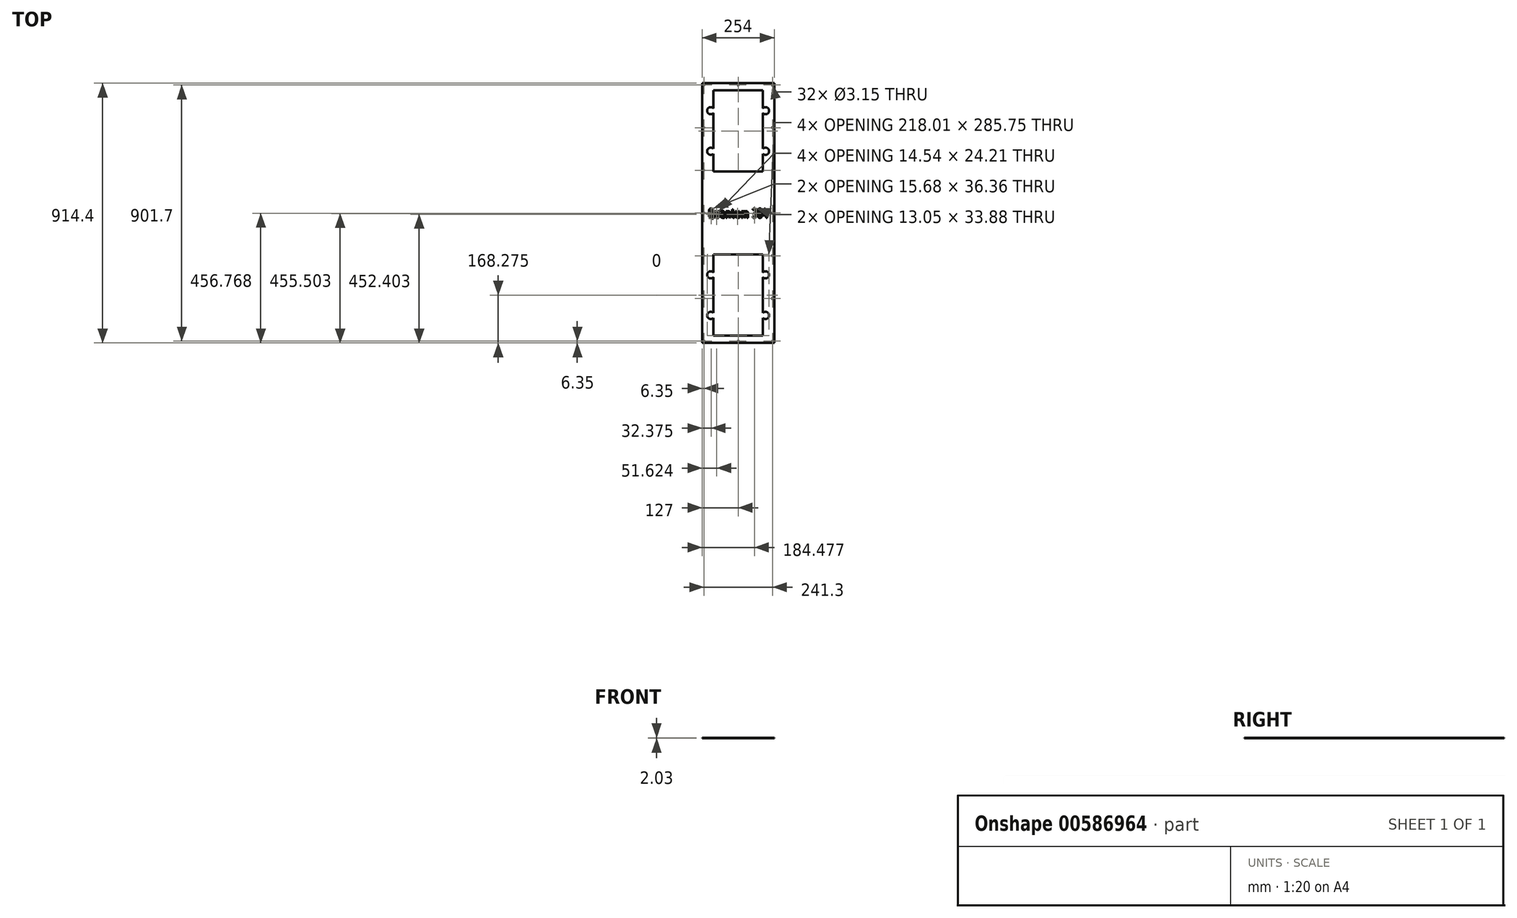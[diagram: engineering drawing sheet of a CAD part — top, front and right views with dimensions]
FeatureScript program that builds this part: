
annotation { "Feature Type Name" : "Feature", "Feature Type Description" : "" }
export const myFeature = defineFeature(function(context is Context, id is Id, definition is map)
    precondition{}
    {
        {
            var Q0;
            Q0=qCreatedBy(makeId("Top.planeOp"),FACE);
            var sketch = newSketch(context, id + "F0", { "sketchPlane" : qUnion([Q0])});
            skLineSegment(sketch, "E0", {"start": v(73.23, -10.8) * mm, "end": v(73.3, -11.12) * mm});
            skLineSegment(sketch, "E1", {"start": v(73.18, -10.45) * mm, "end": v(73.23, -10.8) * mm});
            skLineSegment(sketch, "E2", {"start": v(73.15, -10.1) * mm, "end": v(73.18, -10.45) * mm});
            skLineSegment(sketch, "E3", {"start": v(73.15, -3.36) * mm, "end": v(73.15, -10.1) * mm});
            skLineSegment(sketch, "E4", {"start": v(73.15, -3.18) * mm, "end": v(73.15, -3.36) * mm});
            skLineSegment(sketch, "E5", {"start": v(73.13, -2.99) * mm, "end": v(73.15, -3.18) * mm});
            skLineSegment(sketch, "E6", {"start": v(73.08, -2.81) * mm, "end": v(73.13, -2.99) * mm});
            skLineSegment(sketch, "E7", {"start": v(73.03, -2.64) * mm, "end": v(73.08, -2.81) * mm});
            skLineSegment(sketch, "E8", {"start": v(72.96, -2.47) * mm, "end": v(73.03, -2.64) * mm});
            skLineSegment(sketch, "E9", {"start": v(72.86, -2.3) * mm, "end": v(72.96, -2.47) * mm});
            skLineSegment(sketch, "E10", {"start": v(72.73, -2.14) * mm, "end": v(72.86, -2.3) * mm});
            skLineSegment(sketch, "E11", {"start": v(72.6, -2) * mm, "end": v(72.73, -2.14) * mm});
            skLineSegment(sketch, "E12", {"start": v(72.46, -1.87) * mm, "end": v(72.6, -2) * mm});
            skLineSegment(sketch, "E13", {"start": v(72.31, -1.75) * mm, "end": v(72.46, -1.87) * mm});
            skLineSegment(sketch, "E14", {"start": v(72.14, -1.65) * mm, "end": v(72.31, -1.75) * mm});
            skLineSegment(sketch, "E15", {"start": v(71.96, -1.57) * mm, "end": v(72.14, -1.65) * mm});
            skLineSegment(sketch, "E16", {"start": v(71.79, -1.52) * mm, "end": v(71.96, -1.57) * mm});
            skLineSegment(sketch, "E17", {"start": v(71.62, -1.47) * mm, "end": v(71.79, -1.52) * mm});
            skLineSegment(sketch, "E18", {"start": v(71.42, -1.45) * mm, "end": v(71.62, -1.47) * mm});
            skLineSegment(sketch, "E19", {"start": v(71.22, -1.42) * mm, "end": v(71.42, -1.45) * mm});
            skLineSegment(sketch, "E20", {"start": v(71.05, -1.45) * mm, "end": v(71.22, -1.42) * mm});
            skLineSegment(sketch, "E21", {"start": v(70.85, -1.47) * mm, "end": v(71.05, -1.45) * mm});
            skLineSegment(sketch, "E22", {"start": v(70.67, -1.52) * mm, "end": v(70.85, -1.47) * mm});
            skLineSegment(sketch, "E23", {"start": v(70.5, -1.57) * mm, "end": v(70.67, -1.52) * mm});
            skLineSegment(sketch, "E24", {"start": v(70.33, -1.65) * mm, "end": v(70.5, -1.57) * mm});
            skLineSegment(sketch, "E25", {"start": v(70.15, -1.75) * mm, "end": v(70.33, -1.65) * mm});
            skLineSegment(sketch, "E26", {"start": v(70, -1.87) * mm, "end": v(70.15, -1.75) * mm});
            skLineSegment(sketch, "E27", {"start": v(69.85, -2) * mm, "end": v(70, -1.87) * mm});
            skLineSegment(sketch, "E28", {"start": v(69.73, -2.14) * mm, "end": v(69.85, -2) * mm});
            skLineSegment(sketch, "E29", {"start": v(69.6, -2.3) * mm, "end": v(69.73, -2.14) * mm});
            skLineSegment(sketch, "E30", {"start": v(69.5, -2.47) * mm, "end": v(69.6, -2.3) * mm});
            skLineSegment(sketch, "E31", {"start": v(69.43, -2.64) * mm, "end": v(69.5, -2.47) * mm});
            skLineSegment(sketch, "E32", {"start": v(69.38, -2.81) * mm, "end": v(69.43, -2.64) * mm});
            skLineSegment(sketch, "E33", {"start": v(69.33, -2.99) * mm, "end": v(69.38, -2.81) * mm});
            skLineSegment(sketch, "E34", {"start": v(69.3, -3.18) * mm, "end": v(69.33, -2.99) * mm});
            skLineSegment(sketch, "E35", {"start": v(69.28, -3.36) * mm, "end": v(69.3, -3.18) * mm});
            skLineSegment(sketch, "E36", {"start": v(69.28, -10.1) * mm, "end": v(69.28, -3.36) * mm});
            skLineSegment(sketch, "E37", {"start": v(69.33, -10.85) * mm, "end": v(69.28, -10.1) * mm});
            skLineSegment(sketch, "E38", {"start": v(51, -14.17) * mm, "end": v(50.98, -13.97) * mm});
            skLineSegment(sketch, "E39", {"start": v(51.05, -14.35) * mm, "end": v(51, -14.17) * mm});
            skLineSegment(sketch, "E40", {"start": v(51.1, -14.52) * mm, "end": v(51.05, -14.35) * mm});
            skLineSegment(sketch, "E41", {"start": v(51.2, -14.7) * mm, "end": v(51.1, -14.52) * mm});
            skLineSegment(sketch, "E42", {"start": v(51.3, -14.84) * mm, "end": v(51.2, -14.7) * mm});
            skLineSegment(sketch, "E43", {"start": v(51.4, -15) * mm, "end": v(51.3, -14.84) * mm});
            skLineSegment(sketch, "E44", {"start": v(51.55, -15.14) * mm, "end": v(51.4, -15) * mm});
            skLineSegment(sketch, "E45", {"start": v(52.12, -15.66) * mm, "end": v(51.55, -15.14) * mm});
            skLineSegment(sketch, "E46", {"start": v(52.7, -16.13) * mm, "end": v(52.12, -15.66) * mm});
            skLineSegment(sketch, "E47", {"start": v(53.31, -16.5) * mm, "end": v(52.7, -16.13) * mm});
            skLineSegment(sketch, "E48", {"start": v(53.96, -16.83) * mm, "end": v(53.31, -16.5) * mm});
            skLineSegment(sketch, "E49", {"start": v(54.6, -17.05) * mm, "end": v(53.96, -16.83) * mm});
            skLineSegment(sketch, "E50", {"start": v(55.3, -17.22) * mm, "end": v(54.6, -17.05) * mm});
            skLineSegment(sketch, "E51", {"start": v(56.01, -17.35) * mm, "end": v(55.3, -17.22) * mm});
            skLineSegment(sketch, "E52", {"start": v(56.73, -17.37) * mm, "end": v(56.01, -17.35) * mm});
            skLineSegment(sketch, "E53", {"start": v(57.48, -17.35) * mm, "end": v(56.73, -17.37) * mm});
            skLineSegment(sketch, "E54", {"start": v(58.2, -17.25) * mm, "end": v(57.48, -17.35) * mm});
            skLineSegment(sketch, "E55", {"start": v(58.87, -17.08) * mm, "end": v(58.2, -17.25) * mm});
            skLineSegment(sketch, "E56", {"start": v(59.54, -16.85) * mm, "end": v(58.87, -17.08) * mm});
            skLineSegment(sketch, "E57", {"start": v(60.16, -16.53) * mm, "end": v(59.54, -16.85) * mm});
            skLineSegment(sketch, "E58", {"start": v(60.75, -16.18) * mm, "end": v(60.16, -16.53) * mm});
            skLineSegment(sketch, "E59", {"start": v(61.32, -15.74) * mm, "end": v(60.75, -16.18) * mm});
            skLineSegment(sketch, "E60", {"start": v(61.87, -15.24) * mm, "end": v(61.32, -15.74) * mm});
            skLineSegment(sketch, "E61", {"start": v(62.36, -14.7) * mm, "end": v(61.87, -15.24) * mm});
            skLineSegment(sketch, "E62", {"start": v(62.81, -14.12) * mm, "end": v(62.36, -14.7) * mm});
            skLineSegment(sketch, "E63", {"start": v(63.16, -13.53) * mm, "end": v(62.81, -14.12) * mm});
            skLineSegment(sketch, "E64", {"start": v(63.48, -12.9) * mm, "end": v(63.16, -13.53) * mm});
            skLineSegment(sketch, "E65", {"start": v(63.7, -12.24) * mm, "end": v(63.48, -12.9) * mm});
            skLineSegment(sketch, "E66", {"start": v(63.88, -11.57) * mm, "end": v(63.7, -12.24) * mm});
            skLineSegment(sketch, "E67", {"start": v(63.98, -10.85) * mm, "end": v(63.88, -11.57) * mm});
            skLineSegment(sketch, "E68", {"start": v(64, -10.1) * mm, "end": v(63.98, -10.85) * mm});
            skLineSegment(sketch, "E69", {"start": v(64, -4.77) * mm, "end": v(64, -10.1) * mm});
            skLineSegment(sketch, "E70", {"start": v(63.98, -4.13) * mm, "end": v(64, -4.77) * mm});
            skLineSegment(sketch, "E71", {"start": v(63.9, -3.53) * mm, "end": v(63.98, -4.13) * mm});
            skLineSegment(sketch, "E72", {"start": v(63.75, -2.94) * mm, "end": v(63.9, -3.53) * mm});
            skLineSegment(sketch, "E73", {"start": v(63.55, -2.4) * mm, "end": v(63.75, -2.94) * mm});
            skLineSegment(sketch, "E74", {"start": v(63.3, -1.87) * mm, "end": v(63.55, -2.4) * mm});
            skLineSegment(sketch, "E75", {"start": v(63, -1.35) * mm, "end": v(63.3, -1.87) * mm});
            skLineSegment(sketch, "E76", {"start": v(62.64, -0.88) * mm, "end": v(63, -1.35) * mm});
            skLineSegment(sketch, "E77", {"start": v(62.24, -0.43) * mm, "end": v(62.64, -0.88) * mm});
            skLineSegment(sketch, "E78", {"start": v(62.64, 0.04) * mm, "end": v(62.24, -0.43) * mm});
            skLineSegment(sketch, "E79", {"start": v(63, 0.51) * mm, "end": v(62.64, 0.04) * mm});
            skLineSegment(sketch, "E80", {"start": v(63.3, 1.03) * mm, "end": v(63, 0.51) * mm});
            skLineSegment(sketch, "E81", {"start": v(63.55, 1.55) * mm, "end": v(63.3, 1.03) * mm});
            skLineSegment(sketch, "E82", {"start": v(63.75, 2.1) * mm, "end": v(63.55, 1.55) * mm});
            skLineSegment(sketch, "E83", {"start": v(63.9, 2.7) * mm, "end": v(63.75, 2.1) * mm});
            skLineSegment(sketch, "E84", {"start": v(63.98, 3.29) * mm, "end": v(63.9, 2.7) * mm});
            skLineSegment(sketch, "E85", {"start": v(64, 3.93) * mm, "end": v(63.98, 3.29) * mm});
            skLineSegment(sketch, "E86", {"start": v(64, 9.24) * mm, "end": v(64, 3.93) * mm});
            skLineSegment(sketch, "E87", {"start": v(63.98, 9.99) * mm, "end": v(64, 9.24) * mm});
            skLineSegment(sketch, "E88", {"start": v(63.88, 10.7) * mm, "end": v(63.98, 9.99) * mm});
            skLineSegment(sketch, "E89", {"start": v(63.7, 11.38) * mm, "end": v(63.88, 10.7) * mm});
            skLineSegment(sketch, "E90", {"start": v(63.48, 12.05) * mm, "end": v(63.7, 11.38) * mm});
            skLineSegment(sketch, "E91", {"start": v(63.16, 12.67) * mm, "end": v(63.48, 12.05) * mm});
            skLineSegment(sketch, "E92", {"start": v(62.81, 13.26) * mm, "end": v(63.16, 12.67) * mm});
            skLineSegment(sketch, "E93", {"start": v(62.36, 13.83) * mm, "end": v(62.81, 13.26) * mm});
            skLineSegment(sketch, "E94", {"start": v(61.87, 14.38) * mm, "end": v(62.36, 13.83) * mm});
            skLineSegment(sketch, "E95", {"start": v(61.32, 14.87) * mm, "end": v(61.87, 14.38) * mm});
            skLineSegment(sketch, "E96", {"start": v(60.75, 15.32) * mm, "end": v(61.32, 14.87) * mm});
            skLineSegment(sketch, "E97", {"start": v(60.16, 15.67) * mm, "end": v(60.75, 15.32) * mm});
            skLineSegment(sketch, "E98", {"start": v(59.54, 15.99) * mm, "end": v(60.16, 15.67) * mm});
            skLineSegment(sketch, "E99", {"start": v(58.87, 16.21) * mm, "end": v(59.54, 15.99) * mm});
            skLineSegment(sketch, "E100", {"start": v(58.2, 16.39) * mm, "end": v(58.87, 16.21) * mm});
            skLineSegment(sketch, "E101", {"start": v(57.48, 16.49) * mm, "end": v(58.2, 16.39) * mm});
            skLineSegment(sketch, "E102", {"start": v(56.73, 16.51) * mm, "end": v(57.48, 16.49) * mm});
            skLineSegment(sketch, "E103", {"start": v(56.01, 16.49) * mm, "end": v(56.73, 16.51) * mm});
            skLineSegment(sketch, "E104", {"start": v(55.3, 16.36) * mm, "end": v(56.01, 16.49) * mm});
            skLineSegment(sketch, "E105", {"start": v(54.6, 16.19) * mm, "end": v(55.3, 16.36) * mm});
            skLineSegment(sketch, "E106", {"start": v(53.96, 15.96) * mm, "end": v(54.6, 16.19) * mm});
            skLineSegment(sketch, "E107", {"start": v(53.31, 15.64) * mm, "end": v(53.96, 15.96) * mm});
            skLineSegment(sketch, "E108", {"start": v(52.7, 15.27) * mm, "end": v(53.31, 15.64) * mm});
            skLineSegment(sketch, "E109", {"start": v(52.12, 14.8) * mm, "end": v(52.7, 15.27) * mm});
            skLineSegment(sketch, "E110", {"start": v(51.55, 14.28) * mm, "end": v(52.12, 14.8) * mm});
            skLineSegment(sketch, "E111", {"start": v(51.4, 14.13) * mm, "end": v(51.55, 14.28) * mm});
            skLineSegment(sketch, "E112", {"start": v(51.3, 13.98) * mm, "end": v(51.4, 14.13) * mm});
            skLineSegment(sketch, "E113", {"start": v(51.2, 13.83) * mm, "end": v(51.3, 13.98) * mm});
            skLineSegment(sketch, "E114", {"start": v(51.1, 13.66) * mm, "end": v(51.2, 13.83) * mm});
            skLineSegment(sketch, "E115", {"start": v(51.05, 13.48) * mm, "end": v(51.1, 13.66) * mm});
            skLineSegment(sketch, "E116", {"start": v(51, 13.31) * mm, "end": v(51.05, 13.48) * mm});
            skLineSegment(sketch, "E117", {"start": v(50.98, 13.11) * mm, "end": v(51, 13.31) * mm});
            skLineSegment(sketch, "E118", {"start": v(50.95, 12.94) * mm, "end": v(50.98, 13.11) * mm});
            skLineSegment(sketch, "E119", {"start": v(50.98, 12.74) * mm, "end": v(50.95, 12.94) * mm});
            skLineSegment(sketch, "E120", {"start": v(51, 12.54) * mm, "end": v(50.98, 12.74) * mm});
            skLineSegment(sketch, "E121", {"start": v(51.05, 12.37) * mm, "end": v(51, 12.54) * mm});
            skLineSegment(sketch, "E122", {"start": v(51.1, 12.2) * mm, "end": v(51.05, 12.37) * mm});
            skLineSegment(sketch, "E123", {"start": v(51.18, 12.02) * mm, "end": v(51.1, 12.2) * mm});
            skLineSegment(sketch, "E124", {"start": v(51.28, 11.87) * mm, "end": v(51.18, 12.02) * mm});
            skLineSegment(sketch, "E125", {"start": v(51.4, 11.7) * mm, "end": v(51.28, 11.87) * mm});
            skLineSegment(sketch, "E126", {"start": v(51.52, 11.57) * mm, "end": v(51.4, 11.7) * mm});
            skLineSegment(sketch, "E127", {"start": v(51.67, 11.43) * mm, "end": v(51.52, 11.57) * mm});
            skLineSegment(sketch, "E128", {"start": v(51.82, 11.33) * mm, "end": v(51.67, 11.43) * mm});
            skLineSegment(sketch, "E129", {"start": v(52, 11.23) * mm, "end": v(51.82, 11.33) * mm});
            skLineSegment(sketch, "E130", {"start": v(52.17, 11.13) * mm, "end": v(52, 11.23) * mm});
            skLineSegment(sketch, "E131", {"start": v(52.34, 11.08) * mm, "end": v(52.17, 11.13) * mm});
            skLineSegment(sketch, "E132", {"start": v(52.52, 11.03) * mm, "end": v(52.34, 11.08) * mm});
            skLineSegment(sketch, "E133", {"start": v(52.71, 11) * mm, "end": v(52.52, 11.03) * mm});
            skLineSegment(sketch, "E134", {"start": v(52.89, 11) * mm, "end": v(52.71, 11) * mm});
            skLineSegment(sketch, "E135", {"start": v(53.09, 11) * mm, "end": v(52.89, 11) * mm});
            skLineSegment(sketch, "E136", {"start": v(53.29, 11.03) * mm, "end": v(53.09, 11) * mm});
            skLineSegment(sketch, "E137", {"start": v(53.46, 11.08) * mm, "end": v(53.29, 11.03) * mm});
            skLineSegment(sketch, "E138", {"start": v(53.63, 11.15) * mm, "end": v(53.46, 11.08) * mm});
            skLineSegment(sketch, "E139", {"start": v(53.8, 11.23) * mm, "end": v(53.63, 11.15) * mm});
            skLineSegment(sketch, "E140", {"start": v(53.98, 11.33) * mm, "end": v(53.8, 11.23) * mm});
            skLineSegment(sketch, "E141", {"start": v(54.13, 11.45) * mm, "end": v(53.98, 11.33) * mm});
            skLineSegment(sketch, "E142", {"start": v(54.28, 11.57) * mm, "end": v(54.13, 11.45) * mm});
            skLineSegment(sketch, "E143", {"start": v(54.55, 11.82) * mm, "end": v(54.28, 11.57) * mm});
            skLineSegment(sketch, "E144", {"start": v(54.85, 12.02) * mm, "end": v(54.55, 11.82) * mm});
            skLineSegment(sketch, "E145", {"start": v(55.15, 12.22) * mm, "end": v(54.85, 12.02) * mm});
            skLineSegment(sketch, "E146", {"start": v(55.44, 12.37) * mm, "end": v(55.15, 12.22) * mm});
            skLineSegment(sketch, "E147", {"start": v(55.74, 12.47) * mm, "end": v(55.44, 12.37) * mm});
            skLineSegment(sketch, "E148", {"start": v(56.06, 12.54) * mm, "end": v(55.74, 12.47) * mm});
            skLineSegment(sketch, "E149", {"start": v(56.41, 12.6) * mm, "end": v(56.06, 12.54) * mm});
            skLineSegment(sketch, "E150", {"start": v(56.73, 12.62) * mm, "end": v(56.41, 12.6) * mm});
            skLineSegment(sketch, "E151", {"start": v(57.1, 12.6) * mm, "end": v(56.73, 12.62) * mm});
            skLineSegment(sketch, "E152", {"start": v(57.43, 12.57) * mm, "end": v(57.1, 12.6) * mm});
            skLineSegment(sketch, "E153", {"start": v(57.75, 12.47) * mm, "end": v(57.43, 12.57) * mm});
            skLineSegment(sketch, "E154", {"start": v(58.05, 12.37) * mm, "end": v(57.75, 12.47) * mm});
            skLineSegment(sketch, "E155", {"start": v(58.35, 12.22) * mm, "end": v(58.05, 12.37) * mm});
            skLineSegment(sketch, "E156", {"start": v(58.64, 12.07) * mm, "end": v(58.35, 12.22) * mm});
            skLineSegment(sketch, "E157", {"start": v(58.9, 11.85) * mm, "end": v(58.64, 12.07) * mm});
            skLineSegment(sketch, "E158", {"start": v(59.14, 11.62) * mm, "end": v(58.9, 11.85) * mm});
            skLineSegment(sketch, "E159", {"start": v(59.39, 11.38) * mm, "end": v(59.14, 11.62) * mm});
            skLineSegment(sketch, "E160", {"start": v(59.59, 11.1) * mm, "end": v(59.39, 11.38) * mm});
            skLineSegment(sketch, "E161", {"start": v(59.76, 10.83) * mm, "end": v(59.59, 11.1) * mm});
            skLineSegment(sketch, "E162", {"start": v(59.88, 10.53) * mm, "end": v(59.76, 10.83) * mm});
            skLineSegment(sketch, "E163", {"start": v(59.98, 10.23) * mm, "end": v(59.88, 10.53) * mm});
            skLineSegment(sketch, "E164", {"start": v(60.08, 9.91) * mm, "end": v(59.98, 10.23) * mm});
            skLineSegment(sketch, "E165", {"start": v(60.1, 9.59) * mm, "end": v(60.08, 9.91) * mm});
            skLineSegment(sketch, "E166", {"start": v(60.13, 9.24) * mm, "end": v(60.1, 9.59) * mm});
            skLineSegment(sketch, "E167", {"start": v(60.13, 3.93) * mm, "end": v(60.13, 9.24) * mm});
            skLineSegment(sketch, "E168", {"start": v(60.13, 3.69) * mm, "end": v(60.13, 3.93) * mm});
            skLineSegment(sketch, "E169", {"start": v(60.08, 3.44) * mm, "end": v(60.13, 3.69) * mm});
            skLineSegment(sketch, "E170", {"start": v(60.03, 3.21) * mm, "end": v(60.08, 3.44) * mm});
            skLineSegment(sketch, "E171", {"start": v(59.96, 3) * mm, "end": v(60.03, 3.21) * mm});
            skLineSegment(sketch, "E172", {"start": v(59.86, 2.8) * mm, "end": v(59.96, 3) * mm});
            skLineSegment(sketch, "E173", {"start": v(59.73, 2.6) * mm, "end": v(59.86, 2.8) * mm});
            skLineSegment(sketch, "E174", {"start": v(59.61, 2.4) * mm, "end": v(59.73, 2.6) * mm});
            skLineSegment(sketch, "E175", {"start": v(59.44, 2.22) * mm, "end": v(59.61, 2.4) * mm});
            skLineSegment(sketch, "E176", {"start": v(59.26, 2.05) * mm, "end": v(59.44, 2.22) * mm});
            skLineSegment(sketch, "E177", {"start": v(59.06, 1.9) * mm, "end": v(59.26, 2.05) * mm});
            skLineSegment(sketch, "E178", {"start": v(58.87, 1.8) * mm, "end": v(59.06, 1.9) * mm});
            skLineSegment(sketch, "E179", {"start": v(58.67, 1.7) * mm, "end": v(58.87, 1.8) * mm});
            skLineSegment(sketch, "E180", {"start": v(58.44, 1.6) * mm, "end": v(58.67, 1.7) * mm});
            skLineSegment(sketch, "E181", {"start": v(58.22, 1.55) * mm, "end": v(58.44, 1.6) * mm});
            skLineSegment(sketch, "E182", {"start": v(57.97, 1.53) * mm, "end": v(58.22, 1.55) * mm});
            skLineSegment(sketch, "E183", {"start": v(57.73, 1.5) * mm, "end": v(57.97, 1.53) * mm});
            skLineSegment(sketch, "E184", {"start": v(57.7, 1.5) * mm, "end": v(57.73, 1.5) * mm});
            skLineSegment(sketch, "E185", {"start": v(57.53, 1.5) * mm, "end": v(57.7, 1.5) * mm});
            skLineSegment(sketch, "E186", {"start": v(57.33, 1.48) * mm, "end": v(57.53, 1.5) * mm});
            skLineSegment(sketch, "E187", {"start": v(57.15, 1.43) * mm, "end": v(57.33, 1.48) * mm});
            skLineSegment(sketch, "E188", {"start": v(56.98, 1.38) * mm, "end": v(57.15, 1.43) * mm});
            skLineSegment(sketch, "E189", {"start": v(56.8, 1.3) * mm, "end": v(56.98, 1.38) * mm});
            skLineSegment(sketch, "E190", {"start": v(56.63, 1.2) * mm, "end": v(56.8, 1.3) * mm});
            skLineSegment(sketch, "E191", {"start": v(56.49, 1.08) * mm, "end": v(56.63, 1.2) * mm});
            skLineSegment(sketch, "E192", {"start": v(56.34, 0.96) * mm, "end": v(56.49, 1.08) * mm});
            skLineSegment(sketch, "E193", {"start": v(56.21, 0.8) * mm, "end": v(56.34, 0.96) * mm});
            skLineSegment(sketch, "E194", {"start": v(56.09, 0.66) * mm, "end": v(56.21, 0.8) * mm});
            skLineSegment(sketch, "E195", {"start": v(55.99, 0.49) * mm, "end": v(56.09, 0.66) * mm});
            skLineSegment(sketch, "E196", {"start": v(55.91, 0.31) * mm, "end": v(55.99, 0.49) * mm});
            skLineSegment(sketch, "E197", {"start": v(55.87, 0.14) * mm, "end": v(55.91, 0.31) * mm});
            skLineSegment(sketch, "E198", {"start": v(55.82, -0.03) * mm, "end": v(55.87, 0.14) * mm});
            skLineSegment(sketch, "E199", {"start": v(55.8, -0.23) * mm, "end": v(55.82, -0.03) * mm});
            skLineSegment(sketch, "E200", {"start": v(55.77, -0.43) * mm, "end": v(55.8, -0.23) * mm});
            skLineSegment(sketch, "E201", {"start": v(55.8, -0.6) * mm, "end": v(55.77, -0.43) * mm});
            skLineSegment(sketch, "E202", {"start": v(55.82, -0.8) * mm, "end": v(55.8, -0.6) * mm});
            skLineSegment(sketch, "E203", {"start": v(55.87, -0.98) * mm, "end": v(55.82, -0.8) * mm});
            skLineSegment(sketch, "E204", {"start": v(55.91, -1.15) * mm, "end": v(55.87, -0.98) * mm});
            skLineSegment(sketch, "E205", {"start": v(55.99, -1.3) * mm, "end": v(55.91, -1.15) * mm});
            skLineSegment(sketch, "E206", {"start": v(56.09, -1.47) * mm, "end": v(55.99, -1.3) * mm});
            skLineSegment(sketch, "E207", {"start": v(56.21, -1.62) * mm, "end": v(56.09, -1.47) * mm});
            skLineSegment(sketch, "E208", {"start": v(56.34, -1.77) * mm, "end": v(56.21, -1.62) * mm});
            skLineSegment(sketch, "E209", {"start": v(56.49, -1.92) * mm, "end": v(56.34, -1.77) * mm});
            skLineSegment(sketch, "E210", {"start": v(56.63, -2.02) * mm, "end": v(56.49, -1.92) * mm});
            skLineSegment(sketch, "E211", {"start": v(56.8, -2.12) * mm, "end": v(56.63, -2.02) * mm});
            skLineSegment(sketch, "E212", {"start": v(56.98, -2.22) * mm, "end": v(56.8, -2.12) * mm});
            skLineSegment(sketch, "E213", {"start": v(57.15, -2.27) * mm, "end": v(56.98, -2.22) * mm});
            skLineSegment(sketch, "E214", {"start": v(57.33, -2.32) * mm, "end": v(57.15, -2.27) * mm});
            skLineSegment(sketch, "E215", {"start": v(57.53, -2.34) * mm, "end": v(57.33, -2.32) * mm});
            skLineSegment(sketch, "E216", {"start": v(57.7, -2.37) * mm, "end": v(57.53, -2.34) * mm});
            skLineSegment(sketch, "E217", {"start": v(57.73, -2.37) * mm, "end": v(57.7, -2.37) * mm});
            skLineSegment(sketch, "E218", {"start": v(57.97, -2.37) * mm, "end": v(57.73, -2.37) * mm});
            skLineSegment(sketch, "E219", {"start": v(58.22, -2.4) * mm, "end": v(57.97, -2.37) * mm});
            skLineSegment(sketch, "E220", {"start": v(58.44, -2.47) * mm, "end": v(58.22, -2.4) * mm});
            skLineSegment(sketch, "E221", {"start": v(58.67, -2.54) * mm, "end": v(58.44, -2.47) * mm});
            skLineSegment(sketch, "E222", {"start": v(58.87, -2.64) * mm, "end": v(58.67, -2.54) * mm});
            skLineSegment(sketch, "E223", {"start": v(59.06, -2.74) * mm, "end": v(58.87, -2.64) * mm});
            skLineSegment(sketch, "E224", {"start": v(59.26, -2.89) * mm, "end": v(59.06, -2.74) * mm});
            skLineSegment(sketch, "E225", {"start": v(59.44, -3.06) * mm, "end": v(59.26, -2.89) * mm});
            skLineSegment(sketch, "E226", {"start": v(59.61, -3.23) * mm, "end": v(59.44, -3.06) * mm});
            skLineSegment(sketch, "E227", {"start": v(59.73, -3.43) * mm, "end": v(59.61, -3.23) * mm});
            skLineSegment(sketch, "E228", {"start": v(59.86, -3.63) * mm, "end": v(59.73, -3.43) * mm});
            skLineSegment(sketch, "E229", {"start": v(59.96, -3.83) * mm, "end": v(59.86, -3.63) * mm});
            skLineSegment(sketch, "E230", {"start": v(60.03, -4.05) * mm, "end": v(59.96, -3.83) * mm});
            skLineSegment(sketch, "E231", {"start": v(60.08, -4.28) * mm, "end": v(60.03, -4.05) * mm});
            skLineSegment(sketch, "E232", {"start": v(60.13, -4.52) * mm, "end": v(60.08, -4.28) * mm});
            skLineSegment(sketch, "E233", {"start": v(60.13, -4.77) * mm, "end": v(60.13, -4.52) * mm});
            skLineSegment(sketch, "E234", {"start": v(60.13, -10.1) * mm, "end": v(60.13, -4.77) * mm});
            skLineSegment(sketch, "E235", {"start": v(60.1, -10.45) * mm, "end": v(60.13, -10.1) * mm});
            skLineSegment(sketch, "E236", {"start": v(60.08, -10.78) * mm, "end": v(60.1, -10.45) * mm});
            skLineSegment(sketch, "E237", {"start": v(59.98, -11.1) * mm, "end": v(60.08, -10.78) * mm});
            skLineSegment(sketch, "E238", {"start": v(59.88, -11.4) * mm, "end": v(59.98, -11.1) * mm});
            skLineSegment(sketch, "E239", {"start": v(59.76, -11.7) * mm, "end": v(59.88, -11.4) * mm});
            skLineSegment(sketch, "E240", {"start": v(59.59, -11.97) * mm, "end": v(59.76, -11.7) * mm});
            skLineSegment(sketch, "E241", {"start": v(59.39, -12.24) * mm, "end": v(59.59, -11.97) * mm});
            skLineSegment(sketch, "E242", {"start": v(59.14, -12.49) * mm, "end": v(59.39, -12.24) * mm});
            skLineSegment(sketch, "E243", {"start": v(58.9, -12.7) * mm, "end": v(59.14, -12.49) * mm});
            skLineSegment(sketch, "E244", {"start": v(58.64, -12.93) * mm, "end": v(58.9, -12.7) * mm});
            skLineSegment(sketch, "E245", {"start": v(58.35, -13.08) * mm, "end": v(58.64, -12.93) * mm});
            skLineSegment(sketch, "E246", {"start": v(58.05, -13.23) * mm, "end": v(58.35, -13.08) * mm});
            skLineSegment(sketch, "E247", {"start": v(57.75, -13.33) * mm, "end": v(58.05, -13.23) * mm});
            skLineSegment(sketch, "E248", {"start": v(57.43, -13.43) * mm, "end": v(57.75, -13.33) * mm});
            skLineSegment(sketch, "E249", {"start": v(57.1, -13.45) * mm, "end": v(57.43, -13.43) * mm});
            skLineSegment(sketch, "E250", {"start": v(56.73, -13.48) * mm, "end": v(57.1, -13.45) * mm});
            skLineSegment(sketch, "E251", {"start": v(56.41, -13.45) * mm, "end": v(56.73, -13.48) * mm});
            skLineSegment(sketch, "E252", {"start": v(56.06, -13.4) * mm, "end": v(56.41, -13.45) * mm});
            skLineSegment(sketch, "E253", {"start": v(55.74, -13.33) * mm, "end": v(56.06, -13.4) * mm});
            skLineSegment(sketch, "E254", {"start": v(55.42, -13.2) * mm, "end": v(55.74, -13.33) * mm});
            skLineSegment(sketch, "E255", {"start": v(55.12, -13.06) * mm, "end": v(55.42, -13.2) * mm});
            skLineSegment(sketch, "E256", {"start": v(54.82, -12.88) * mm, "end": v(55.12, -13.06) * mm});
            skLineSegment(sketch, "E257", {"start": v(54.55, -12.66) * mm, "end": v(54.82, -12.88) * mm});
            skLineSegment(sketch, "E258", {"start": v(54.28, -12.41) * mm, "end": v(54.55, -12.66) * mm});
            skLineSegment(sketch, "E259", {"start": v(54.13, -12.29) * mm, "end": v(54.28, -12.41) * mm});
            skLineSegment(sketch, "E260", {"start": v(53.98, -12.16) * mm, "end": v(54.13, -12.29) * mm});
            skLineSegment(sketch, "E261", {"start": v(53.8, -12.07) * mm, "end": v(53.98, -12.16) * mm});
            skLineSegment(sketch, "E262", {"start": v(53.63, -12) * mm, "end": v(53.8, -12.07) * mm});
            skLineSegment(sketch, "E263", {"start": v(53.46, -11.94) * mm, "end": v(53.63, -12) * mm});
            skLineSegment(sketch, "E264", {"start": v(53.29, -11.9) * mm, "end": v(53.46, -11.94) * mm});
            skLineSegment(sketch, "E265", {"start": v(53.09, -11.87) * mm, "end": v(53.29, -11.9) * mm});
            skLineSegment(sketch, "E266", {"start": v(52.89, -11.87) * mm, "end": v(53.09, -11.87) * mm});
            skLineSegment(sketch, "E267", {"start": v(52.71, -11.87) * mm, "end": v(52.89, -11.87) * mm});
            skLineSegment(sketch, "E268", {"start": v(52.52, -11.9) * mm, "end": v(52.71, -11.87) * mm});
            skLineSegment(sketch, "E269", {"start": v(52.34, -11.94) * mm, "end": v(52.52, -11.9) * mm});
            skLineSegment(sketch, "E270", {"start": v(52.17, -12) * mm, "end": v(52.34, -11.94) * mm});
            skLineSegment(sketch, "E271", {"start": v(52, -12.09) * mm, "end": v(52.17, -12) * mm});
            skLineSegment(sketch, "E272", {"start": v(51.82, -12.19) * mm, "end": v(52, -12.09) * mm});
            skLineSegment(sketch, "E273", {"start": v(51.67, -12.29) * mm, "end": v(51.82, -12.19) * mm});
            skLineSegment(sketch, "E274", {"start": v(51.52, -12.44) * mm, "end": v(51.67, -12.29) * mm});
            skLineSegment(sketch, "E275", {"start": v(51.4, -12.56) * mm, "end": v(51.52, -12.44) * mm});
            skLineSegment(sketch, "E276", {"start": v(51.28, -12.73) * mm, "end": v(51.4, -12.56) * mm});
            skLineSegment(sketch, "E277", {"start": v(51.18, -12.88) * mm, "end": v(51.28, -12.73) * mm});
            skLineSegment(sketch, "E278", {"start": v(51.1, -13.06) * mm, "end": v(51.18, -12.88) * mm});
            skLineSegment(sketch, "E279", {"start": v(51.05, -13.23) * mm, "end": v(51.1, -13.06) * mm});
            skLineSegment(sketch, "E280", {"start": v(51, -13.4) * mm, "end": v(51.05, -13.23) * mm});
            skLineSegment(sketch, "E281", {"start": v(50.98, -13.6) * mm, "end": v(51, -13.4) * mm});
            skLineSegment(sketch, "E282", {"start": v(50.95, -13.8) * mm, "end": v(50.98, -13.6) * mm});
            skLineSegment(sketch, "E283", {"start": v(50.98, -13.97) * mm, "end": v(50.95, -13.8) * mm});
            skLineSegment(sketch, "E284", {"start": v(11.81, -15.51) * mm, "end": v(11.76, -15.34) * mm});
            skLineSegment(sketch, "E285", {"start": v(11.89, -15.69) * mm, "end": v(11.81, -15.51) * mm});
            skLineSegment(sketch, "E286", {"start": v(11.96, -15.86) * mm, "end": v(11.89, -15.69) * mm});
            skLineSegment(sketch, "E287", {"start": v(12.06, -16.03) * mm, "end": v(11.96, -15.86) * mm});
            skLineSegment(sketch, "E288", {"start": v(12.18, -16.18) * mm, "end": v(12.06, -16.03) * mm});
            skLineSegment(sketch, "E289", {"start": v(12.3, -16.33) * mm, "end": v(12.18, -16.18) * mm});
            skLineSegment(sketch, "E290", {"start": v(12.46, -16.46) * mm, "end": v(12.3, -16.33) * mm});
            skLineSegment(sketch, "E291", {"start": v(12.6, -16.58) * mm, "end": v(12.46, -16.46) * mm});
            skLineSegment(sketch, "E292", {"start": v(12.75, -16.68) * mm, "end": v(12.6, -16.58) * mm});
            skLineSegment(sketch, "E293", {"start": v(12.93, -16.75) * mm, "end": v(12.75, -16.68) * mm});
            skLineSegment(sketch, "E294", {"start": v(13.1, -16.8) * mm, "end": v(12.93, -16.75) * mm});
            skLineSegment(sketch, "E295", {"start": v(13.28, -16.85) * mm, "end": v(13.1, -16.8) * mm});
            skLineSegment(sketch, "E296", {"start": v(13.47, -16.88) * mm, "end": v(13.28, -16.85) * mm});
            skLineSegment(sketch, "E297", {"start": v(13.67, -16.9) * mm, "end": v(13.47, -16.88) * mm});
            skLineSegment(sketch, "E298", {"start": v(13.87, -16.88) * mm, "end": v(13.67, -16.9) * mm});
            skLineSegment(sketch, "E299", {"start": v(14.07, -16.85) * mm, "end": v(13.87, -16.88) * mm});
            skLineSegment(sketch, "E300", {"start": v(14.24, -16.8) * mm, "end": v(14.07, -16.85) * mm});
            skLineSegment(sketch, "E301", {"start": v(14.42, -16.75) * mm, "end": v(14.24, -16.8) * mm});
            skLineSegment(sketch, "E302", {"start": v(14.6, -16.68) * mm, "end": v(14.42, -16.75) * mm});
            skLineSegment(sketch, "E303", {"start": v(14.74, -16.58) * mm, "end": v(14.6, -16.68) * mm});
            skLineSegment(sketch, "E304", {"start": v(14.89, -16.46) * mm, "end": v(14.74, -16.58) * mm});
            skLineSegment(sketch, "E305", {"start": v(15.04, -16.33) * mm, "end": v(14.89, -16.46) * mm});
            skLineSegment(sketch, "E306", {"start": v(15.16, -16.18) * mm, "end": v(15.04, -16.33) * mm});
            skLineSegment(sketch, "E307", {"start": v(15.28, -16.03) * mm, "end": v(15.16, -16.18) * mm});
            skLineSegment(sketch, "E308", {"start": v(15.38, -15.86) * mm, "end": v(15.28, -16.03) * mm});
            skLineSegment(sketch, "E309", {"start": v(15.46, -15.69) * mm, "end": v(15.38, -15.86) * mm});
            skLineSegment(sketch, "E310", {"start": v(15.53, -15.51) * mm, "end": v(15.46, -15.69) * mm});
            skLineSegment(sketch, "E311", {"start": v(15.58, -15.34) * mm, "end": v(15.53, -15.51) * mm});
            skLineSegment(sketch, "E312", {"start": v(15.6, -15.14) * mm, "end": v(15.58, -15.34) * mm});
            skLineSegment(sketch, "E313", {"start": v(15.6, -14.97) * mm, "end": v(15.6, -15.14) * mm});
            skLineSegment(sketch, "E314", {"start": v(15.6, 3.44) * mm, "end": v(15.6, -14.97) * mm});
            skLineSegment(sketch, "E315", {"start": v(21.41, 3.44) * mm, "end": v(15.6, 3.44) * mm});
            skLineSegment(sketch, "E316", {"start": v(21.41, -14.97) * mm, "end": v(21.41, 3.44) * mm});
            skLineSegment(sketch, "E317", {"start": v(21.41, -15.14) * mm, "end": v(21.41, -14.97) * mm});
            skLineSegment(sketch, "E318", {"start": v(21.44, -15.34) * mm, "end": v(21.41, -15.14) * mm});
            skLineSegment(sketch, "E319", {"start": v(21.49, -15.51) * mm, "end": v(21.44, -15.34) * mm});
            skLineSegment(sketch, "E320", {"start": v(21.56, -15.69) * mm, "end": v(21.49, -15.51) * mm});
            skLineSegment(sketch, "E321", {"start": v(21.63, -15.86) * mm, "end": v(21.56, -15.69) * mm});
            skLineSegment(sketch, "E322", {"start": v(21.73, -16.03) * mm, "end": v(21.63, -15.86) * mm});
            skLineSegment(sketch, "E323", {"start": v(21.86, -16.18) * mm, "end": v(21.73, -16.03) * mm});
            skLineSegment(sketch, "E324", {"start": v(21.98, -16.33) * mm, "end": v(21.86, -16.18) * mm});
            skLineSegment(sketch, "E325", {"start": v(22.13, -16.46) * mm, "end": v(21.98, -16.33) * mm});
            skLineSegment(sketch, "E326", {"start": v(22.28, -16.58) * mm, "end": v(22.13, -16.46) * mm});
            skLineSegment(sketch, "E327", {"start": v(22.43, -16.68) * mm, "end": v(22.28, -16.58) * mm});
            skLineSegment(sketch, "E328", {"start": v(22.6, -16.75) * mm, "end": v(22.43, -16.68) * mm});
            skLineSegment(sketch, "E329", {"start": v(22.78, -16.8) * mm, "end": v(22.6, -16.75) * mm});
            skLineSegment(sketch, "E330", {"start": v(22.95, -16.85) * mm, "end": v(22.78, -16.8) * mm});
            skLineSegment(sketch, "E331", {"start": v(23.15, -16.88) * mm, "end": v(22.95, -16.85) * mm});
            skLineSegment(sketch, "E332", {"start": v(23.35, -16.9) * mm, "end": v(23.15, -16.88) * mm});
            skLineSegment(sketch, "E333", {"start": v(23.54, -16.88) * mm, "end": v(23.35, -16.9) * mm});
            skLineSegment(sketch, "E334", {"start": v(23.74, -16.85) * mm, "end": v(23.54, -16.88) * mm});
            skLineSegment(sketch, "E335", {"start": v(23.92, -16.8) * mm, "end": v(23.74, -16.85) * mm});
            skLineSegment(sketch, "E336", {"start": v(24.1, -16.75) * mm, "end": v(23.92, -16.8) * mm});
            skLineSegment(sketch, "E337", {"start": v(24.26, -16.68) * mm, "end": v(24.1, -16.75) * mm});
            skLineSegment(sketch, "E338", {"start": v(24.41, -16.58) * mm, "end": v(24.26, -16.68) * mm});
            skLineSegment(sketch, "E339", {"start": v(24.56, -16.46) * mm, "end": v(24.41, -16.58) * mm});
            skLineSegment(sketch, "E340", {"start": v(24.71, -16.33) * mm, "end": v(24.56, -16.46) * mm});
            skLineSegment(sketch, "E341", {"start": v(24.83, -16.18) * mm, "end": v(24.71, -16.33) * mm});
            skLineSegment(sketch, "E342", {"start": v(24.96, -16.03) * mm, "end": v(24.83, -16.18) * mm});
            skLineSegment(sketch, "E343", {"start": v(25.06, -15.86) * mm, "end": v(24.96, -16.03) * mm});
            skLineSegment(sketch, "E344", {"start": v(25.13, -15.69) * mm, "end": v(25.06, -15.86) * mm});
            skLineSegment(sketch, "E345", {"start": v(25.2, -15.51) * mm, "end": v(25.13, -15.69) * mm});
            skLineSegment(sketch, "E346", {"start": v(25.26, -15.34) * mm, "end": v(25.2, -15.51) * mm});
            skLineSegment(sketch, "E347", {"start": v(25.28, -15.14) * mm, "end": v(25.26, -15.34) * mm});
            skLineSegment(sketch, "E348", {"start": v(25.28, -14.97) * mm, "end": v(25.28, -15.14) * mm});
            skLineSegment(sketch, "E349", {"start": v(25.28, 3.44) * mm, "end": v(25.28, -14.97) * mm});
            skLineSegment(sketch, "E350", {"start": v(27.71, 3.44) * mm, "end": v(25.28, 3.44) * mm});
            skLineSegment(sketch, "E351", {"start": v(28.03, 3.41) * mm, "end": v(27.71, 3.44) * mm});
            skLineSegment(sketch, "E352", {"start": v(28.38, 3.36) * mm, "end": v(28.03, 3.41) * mm});
            skLineSegment(sketch, "E353", {"start": v(28.7, 3.29) * mm, "end": v(28.38, 3.36) * mm});
            skLineSegment(sketch, "E354", {"start": v(29, 3.19) * mm, "end": v(28.7, 3.29) * mm});
            skLineSegment(sketch, "E355", {"start": v(29.3, 3.04) * mm, "end": v(29, 3.19) * mm});
            skLineSegment(sketch, "E356", {"start": v(29.57, 2.87) * mm, "end": v(29.3, 3.04) * mm});
            skLineSegment(sketch, "E357", {"start": v(29.84, 2.67) * mm, "end": v(29.57, 2.87) * mm});
            skLineSegment(sketch, "E358", {"start": v(30.1, 2.45) * mm, "end": v(29.84, 2.67) * mm});
            skLineSegment(sketch, "E359", {"start": v(30.32, 2.17) * mm, "end": v(30.1, 2.45) * mm});
            skLineSegment(sketch, "E360", {"start": v(30.54, 1.9) * mm, "end": v(30.32, 2.17) * mm});
            skLineSegment(sketch, "E361", {"start": v(30.69, 1.63) * mm, "end": v(30.54, 1.9) * mm});
            skLineSegment(sketch, "E362", {"start": v(30.84, 1.33) * mm, "end": v(30.69, 1.63) * mm});
            skLineSegment(sketch, "E363", {"start": v(30.94, 1.03) * mm, "end": v(30.84, 1.33) * mm});
            skLineSegment(sketch, "E364", {"start": v(31.04, 0.7) * mm, "end": v(30.94, 1.03) * mm});
            skLineSegment(sketch, "E365", {"start": v(31.06, 0.39) * mm, "end": v(31.04, 0.7) * mm});
            skLineSegment(sketch, "E366", {"start": v(31.09, 0.04) * mm, "end": v(31.06, 0.39) * mm});
            skLineSegment(sketch, "E367", {"start": v(31.09, -14.97) * mm, "end": v(31.09, 0.04) * mm});
            skLineSegment(sketch, "E368", {"start": v(31.09, -15.14) * mm, "end": v(31.09, -14.97) * mm});
            skLineSegment(sketch, "E369", {"start": v(31.11, -15.34) * mm, "end": v(31.09, -15.14) * mm});
            skLineSegment(sketch, "E370", {"start": v(31.16, -15.51) * mm, "end": v(31.11, -15.34) * mm});
            skLineSegment(sketch, "E371", {"start": v(31.23, -15.69) * mm, "end": v(31.16, -15.51) * mm});
            skLineSegment(sketch, "E372", {"start": v(31.3, -15.86) * mm, "end": v(31.23, -15.69) * mm});
            skLineSegment(sketch, "E373", {"start": v(31.4, -16.03) * mm, "end": v(31.3, -15.86) * mm});
            skLineSegment(sketch, "E374", {"start": v(31.53, -16.18) * mm, "end": v(31.4, -16.03) * mm});
            skLineSegment(sketch, "E375", {"start": v(31.66, -16.33) * mm, "end": v(31.53, -16.18) * mm});
            skLineSegment(sketch, "E376", {"start": v(31.8, -16.46) * mm, "end": v(31.66, -16.33) * mm});
            skLineSegment(sketch, "E377", {"start": v(31.95, -16.58) * mm, "end": v(31.8, -16.46) * mm});
            skLineSegment(sketch, "E378", {"start": v(32.1, -16.68) * mm, "end": v(31.95, -16.58) * mm});
            skLineSegment(sketch, "E379", {"start": v(32.28, -16.75) * mm, "end": v(32.1, -16.68) * mm});
            skLineSegment(sketch, "E380", {"start": v(32.45, -16.8) * mm, "end": v(32.28, -16.75) * mm});
            skLineSegment(sketch, "E381", {"start": v(32.62, -16.85) * mm, "end": v(32.45, -16.8) * mm});
            skLineSegment(sketch, "E382", {"start": v(32.82, -16.88) * mm, "end": v(32.62, -16.85) * mm});
            skLineSegment(sketch, "E383", {"start": v(33.02, -16.9) * mm, "end": v(32.82, -16.88) * mm});
            skLineSegment(sketch, "E384", {"start": v(33.22, -16.88) * mm, "end": v(33.02, -16.9) * mm});
            skLineSegment(sketch, "E385", {"start": v(33.42, -16.85) * mm, "end": v(33.22, -16.88) * mm});
            skLineSegment(sketch, "E386", {"start": v(33.6, -16.8) * mm, "end": v(33.42, -16.85) * mm});
            skLineSegment(sketch, "E387", {"start": v(33.76, -16.75) * mm, "end": v(33.6, -16.8) * mm});
            skLineSegment(sketch, "E388", {"start": v(33.94, -16.68) * mm, "end": v(33.76, -16.75) * mm});
            skLineSegment(sketch, "E389", {"start": v(34.09, -16.58) * mm, "end": v(33.94, -16.68) * mm});
            skLineSegment(sketch, "E390", {"start": v(34.24, -16.46) * mm, "end": v(34.09, -16.58) * mm});
            skLineSegment(sketch, "E391", {"start": v(34.38, -16.33) * mm, "end": v(34.24, -16.46) * mm});
            skLineSegment(sketch, "E392", {"start": v(34.5, -16.18) * mm, "end": v(34.38, -16.33) * mm});
            skLineSegment(sketch, "E393", {"start": v(34.63, -16.03) * mm, "end": v(34.5, -16.18) * mm});
            skLineSegment(sketch, "E394", {"start": v(34.73, -15.86) * mm, "end": v(34.63, -16.03) * mm});
            skLineSegment(sketch, "E395", {"start": v(34.8, -15.69) * mm, "end": v(34.73, -15.86) * mm});
            skLineSegment(sketch, "E396", {"start": v(34.88, -15.51) * mm, "end": v(34.8, -15.69) * mm});
            skLineSegment(sketch, "E397", {"start": v(34.93, -15.34) * mm, "end": v(34.88, -15.51) * mm});
            skLineSegment(sketch, "E398", {"start": v(34.95, -15.14) * mm, "end": v(34.93, -15.34) * mm});
            skLineSegment(sketch, "E399", {"start": v(34.95, -14.97) * mm, "end": v(34.95, -15.14) * mm});
            skLineSegment(sketch, "E400", {"start": v(34.95, 0.04) * mm, "end": v(34.95, -14.97) * mm});
            skLineSegment(sketch, "E401", {"start": v(34.93, 0.78) * mm, "end": v(34.95, 0.04) * mm});
            skLineSegment(sketch, "E402", {"start": v(34.83, 1.48) * mm, "end": v(34.93, 0.78) * mm});
            skLineSegment(sketch, "E403", {"start": v(34.66, 2.17) * mm, "end": v(34.83, 1.48) * mm});
            skLineSegment(sketch, "E404", {"start": v(34.43, 2.82) * mm, "end": v(34.66, 2.17) * mm});
            skLineSegment(sketch, "E405", {"start": v(34.11, 3.44) * mm, "end": v(34.43, 2.82) * mm});
            skLineSegment(sketch, "E406", {"start": v(33.76, 4.06) * mm, "end": v(34.11, 3.44) * mm});
            skLineSegment(sketch, "E407", {"start": v(33.32, 4.63) * mm, "end": v(33.76, 4.06) * mm});
            skLineSegment(sketch, "E408", {"start": v(32.82, 5.17) * mm, "end": v(33.32, 4.63) * mm});
            skLineSegment(sketch, "E409", {"start": v(32.28, 5.67) * mm, "end": v(32.82, 5.17) * mm});
            skLineSegment(sketch, "E410", {"start": v(31.7, 6.1) * mm, "end": v(32.28, 5.67) * mm});
            skLineSegment(sketch, "E411", {"start": v(31.11, 6.46) * mm, "end": v(31.7, 6.1) * mm});
            skLineSegment(sketch, "E412", {"start": v(30.49, 6.76) * mm, "end": v(31.11, 6.46) * mm});
            skLineSegment(sketch, "E413", {"start": v(29.82, 6.99) * mm, "end": v(30.49, 6.76) * mm});
            skLineSegment(sketch, "E414", {"start": v(-22.44, 3.9) * mm, "end": v(-22.54, 4) * mm});
            skLineSegment(sketch, "E415", {"start": v(-22.54, 4) * mm, "end": v(-22.7, 4.16) * mm});
            skLineSegment(sketch, "E416", {"start": v(-22.7, 4.16) * mm, "end": v(-22.8, 4.3) * mm});
            skLineSegment(sketch, "E417", {"start": v(-22.8, 4.3) * mm, "end": v(-22.89, 4.48) * mm});
            skLineSegment(sketch, "E418", {"start": v(-22.89, 4.48) * mm, "end": v(-22.99, 4.63) * mm});
            skLineSegment(sketch, "E419", {"start": v(-22.99, 4.63) * mm, "end": v(-23.04, 4.8) * mm});
            skLineSegment(sketch, "E420", {"start": v(-23.04, 4.8) * mm, "end": v(-23.09, 4.98) * mm});
            skLineSegment(sketch, "E421", {"start": v(-9.52, -10.38) * mm, "end": v(-9.57, -9.63) * mm});
            skLineSegment(sketch, "E422", {"start": v(-9.57, -9.63) * mm, "end": v(-9.57, 5.37) * mm});
            skLineSegment(sketch, "E423", {"start": v(-9.57, 5.37) * mm, "end": v(-9.54, 5.55) * mm});
            skLineSegment(sketch, "E424", {"start": v(-9.54, 5.55) * mm, "end": v(-9.52, 5.74) * mm});
            skLineSegment(sketch, "E425", {"start": v(-9.52, 5.74) * mm, "end": v(-9.47, 5.92) * mm});
            skLineSegment(sketch, "E426", {"start": v(-9.47, 5.92) * mm, "end": v(-9.42, 6.1) * mm});
            skLineSegment(sketch, "E427", {"start": v(-9.42, 6.1) * mm, "end": v(-9.35, 6.27) * mm});
            skLineSegment(sketch, "E428", {"start": v(-9.35, 6.27) * mm, "end": v(-9.25, 6.44) * mm});
            skLineSegment(sketch, "E429", {"start": v(-9.25, 6.44) * mm, "end": v(-9.12, 6.59) * mm});
            skLineSegment(sketch, "E430", {"start": v(-9.12, 6.59) * mm, "end": v(-9, 6.74) * mm});
            skLineSegment(sketch, "E431", {"start": v(-9, 6.74) * mm, "end": v(-8.85, 6.86) * mm});
            skLineSegment(sketch, "E432", {"start": v(-8.85, 6.86) * mm, "end": v(-8.7, 6.99) * mm});
            skLineSegment(sketch, "E433", {"start": v(-8.7, 6.99) * mm, "end": v(-8.53, 7.08) * mm});
            skLineSegment(sketch, "E434", {"start": v(-8.53, 7.08) * mm, "end": v(-8.35, 7.16) * mm});
            skLineSegment(sketch, "E435", {"start": v(-8.35, 7.16) * mm, "end": v(-8.18, 7.2) * mm});
            skLineSegment(sketch, "E436", {"start": v(-8.18, 7.2) * mm, "end": v(-8, 7.26) * mm});
            skLineSegment(sketch, "E437", {"start": v(-8, 7.26) * mm, "end": v(-7.8, 7.28) * mm});
            skLineSegment(sketch, "E438", {"start": v(-7.8, 7.28) * mm, "end": v(-7.63, 7.3) * mm});
            skLineSegment(sketch, "E439", {"start": v(-7.63, 7.3) * mm, "end": v(-7.44, 7.28) * mm});
            skLineSegment(sketch, "E440", {"start": v(-7.44, 7.28) * mm, "end": v(-7.24, 7.26) * mm});
            skLineSegment(sketch, "E441", {"start": v(-7.24, 7.26) * mm, "end": v(-7.06, 7.2) * mm});
            skLineSegment(sketch, "E442", {"start": v(-7.06, 7.2) * mm, "end": v(-6.9, 7.16) * mm});
            skLineSegment(sketch, "E443", {"start": v(-6.9, 7.16) * mm, "end": v(-6.72, 7.08) * mm});
            skLineSegment(sketch, "E444", {"start": v(-6.72, 7.08) * mm, "end": v(-6.54, 6.99) * mm});
            skLineSegment(sketch, "E445", {"start": v(-6.54, 6.99) * mm, "end": v(-6.4, 6.86) * mm});
            skLineSegment(sketch, "E446", {"start": v(-6.4, 6.86) * mm, "end": v(-6.25, 6.74) * mm});
            skLineSegment(sketch, "E447", {"start": v(-6.25, 6.74) * mm, "end": v(-6.12, 6.59) * mm});
            skLineSegment(sketch, "E448", {"start": v(-6.12, 6.59) * mm, "end": v(-6, 6.44) * mm});
            skLineSegment(sketch, "E449", {"start": v(-6, 6.44) * mm, "end": v(-5.9, 6.27) * mm});
            skLineSegment(sketch, "E450", {"start": v(-5.9, 6.27) * mm, "end": v(-5.82, 6.1) * mm});
            skLineSegment(sketch, "E451", {"start": v(-5.82, 6.1) * mm, "end": v(-5.77, 5.92) * mm});
            skLineSegment(sketch, "E452", {"start": v(-5.77, 5.92) * mm, "end": v(-5.72, 5.74) * mm});
            skLineSegment(sketch, "E453", {"start": v(-5.72, 5.74) * mm, "end": v(-5.7, 5.55) * mm});
            skLineSegment(sketch, "E454", {"start": v(-5.7, 5.55) * mm, "end": v(-5.7, 5.37) * mm});
            skLineSegment(sketch, "E455", {"start": v(-5.7, 5.37) * mm, "end": v(-5.7, -9.63) * mm});
            skLineSegment(sketch, "E456", {"start": v(-5.7, -9.63) * mm, "end": v(-5.68, -9.98) * mm});
            skLineSegment(sketch, "E457", {"start": v(-5.68, -9.98) * mm, "end": v(-5.63, -10.3) * mm});
            skLineSegment(sketch, "E458", {"start": v(-5.63, -10.3) * mm, "end": v(-5.55, -10.63) * mm});
            skLineSegment(sketch, "E459", {"start": v(-5.55, -10.63) * mm, "end": v(-5.45, -10.92) * mm});
            skLineSegment(sketch, "E460", {"start": v(-5.45, -10.92) * mm, "end": v(-5.3, -11.22) * mm});
            skLineSegment(sketch, "E461", {"start": v(-5.3, -11.22) * mm, "end": v(-5.13, -11.5) * mm});
            skLineSegment(sketch, "E462", {"start": v(-5.13, -11.5) * mm, "end": v(-4.93, -11.77) * mm});
            skLineSegment(sketch, "E463", {"start": v(-4.93, -11.77) * mm, "end": v(-4.7, -12.04) * mm});
            skLineSegment(sketch, "E464", {"start": v(-4.7, -12.04) * mm, "end": v(-4.44, -12.26) * mm});
            skLineSegment(sketch, "E465", {"start": v(-4.44, -12.26) * mm, "end": v(-4.16, -12.46) * mm});
            skLineSegment(sketch, "E466", {"start": v(-4.16, -12.46) * mm, "end": v(-3.89, -12.64) * mm});
            skLineSegment(sketch, "E467", {"start": v(-3.89, -12.64) * mm, "end": v(-3.6, -12.78) * mm});
            skLineSegment(sketch, "E468", {"start": v(-3.6, -12.78) * mm, "end": v(-3.3, -12.88) * mm});
            skLineSegment(sketch, "E469", {"start": v(-3.3, -12.88) * mm, "end": v(-2.97, -12.96) * mm});
            skLineSegment(sketch, "E470", {"start": v(-2.97, -12.96) * mm, "end": v(-2.65, -13) * mm});
            skLineSegment(sketch, "E471", {"start": v(-2.65, -13) * mm, "end": v(-2.3, -13.03) * mm});
            skLineSegment(sketch, "E472", {"start": v(-2.3, -13.03) * mm, "end": v(1.1, -13.03) * mm});
            skLineSegment(sketch, "E473", {"start": v(1.1, -13.03) * mm, "end": v(1.1, 5.37) * mm});
            skLineSegment(sketch, "E474", {"start": v(1.1, 5.37) * mm, "end": v(1.1, 5.55) * mm});
            skLineSegment(sketch, "E475", {"start": v(1.1, 5.55) * mm, "end": v(1.12, 5.74) * mm});
            skLineSegment(sketch, "E476", {"start": v(1.12, 5.74) * mm, "end": v(1.17, 5.92) * mm});
            skLineSegment(sketch, "E477", {"start": v(1.17, 5.92) * mm, "end": v(1.22, 6.1) * mm});
            skLineSegment(sketch, "E478", {"start": v(1.22, 6.1) * mm, "end": v(1.3, 6.27) * mm});
            skLineSegment(sketch, "E479", {"start": v(1.3, 6.27) * mm, "end": v(1.4, 6.44) * mm});
            skLineSegment(sketch, "E480", {"start": v(1.4, 6.44) * mm, "end": v(1.52, 6.59) * mm});
            skLineSegment(sketch, "E481", {"start": v(1.52, 6.59) * mm, "end": v(1.64, 6.74) * mm});
            skLineSegment(sketch, "E482", {"start": v(1.64, 6.74) * mm, "end": v(1.8, 6.86) * mm});
            skLineSegment(sketch, "E483", {"start": v(1.8, 6.86) * mm, "end": v(1.94, 6.99) * mm});
            skLineSegment(sketch, "E484", {"start": v(1.94, 6.99) * mm, "end": v(2.11, 7.08) * mm});
            skLineSegment(sketch, "E485", {"start": v(2.11, 7.08) * mm, "end": v(2.29, 7.16) * mm});
            skLineSegment(sketch, "E486", {"start": v(2.29, 7.16) * mm, "end": v(2.46, 7.2) * mm});
            skLineSegment(sketch, "E487", {"start": v(2.46, 7.2) * mm, "end": v(2.63, 7.26) * mm});
            skLineSegment(sketch, "E488", {"start": v(2.63, 7.26) * mm, "end": v(2.83, 7.28) * mm});
            skLineSegment(sketch, "E489", {"start": v(2.83, 7.28) * mm, "end": v(3.03, 7.3) * mm});
            skLineSegment(sketch, "E490", {"start": v(3.03, 7.3) * mm, "end": v(3.2, 7.28) * mm});
            skLineSegment(sketch, "E491", {"start": v(3.2, 7.28) * mm, "end": v(3.4, 7.26) * mm});
            skLineSegment(sketch, "E492", {"start": v(3.4, 7.26) * mm, "end": v(3.58, 7.2) * mm});
            skLineSegment(sketch, "E493", {"start": v(3.58, 7.2) * mm, "end": v(3.75, 7.16) * mm});
            skLineSegment(sketch, "E494", {"start": v(3.75, 7.16) * mm, "end": v(3.92, 7.08) * mm});
            skLineSegment(sketch, "E495", {"start": v(3.92, 7.08) * mm, "end": v(4.1, 6.99) * mm});
            skLineSegment(sketch, "E496", {"start": v(4.1, 6.99) * mm, "end": v(4.25, 6.86) * mm});
            skLineSegment(sketch, "E497", {"start": v(4.25, 6.86) * mm, "end": v(4.4, 6.74) * mm});
            skLineSegment(sketch, "E498", {"start": v(4.4, 6.74) * mm, "end": v(4.52, 6.59) * mm});
            skLineSegment(sketch, "E499", {"start": v(4.52, 6.59) * mm, "end": v(4.64, 6.44) * mm});
            skLineSegment(sketch, "E500", {"start": v(4.64, 6.44) * mm, "end": v(4.74, 6.27) * mm});
            skLineSegment(sketch, "E501", {"start": v(4.74, 6.27) * mm, "end": v(4.82, 6.1) * mm});
            skLineSegment(sketch, "E502", {"start": v(4.82, 6.1) * mm, "end": v(4.87, 5.92) * mm});
            skLineSegment(sketch, "E503", {"start": v(4.87, 5.92) * mm, "end": v(4.92, 5.74) * mm});
            skLineSegment(sketch, "E504", {"start": v(4.92, 5.74) * mm, "end": v(4.94, 5.55) * mm});
            skLineSegment(sketch, "E505", {"start": v(4.94, 5.55) * mm, "end": v(4.97, 5.37) * mm});
            skLineSegment(sketch, "E506", {"start": v(4.97, 5.37) * mm, "end": v(4.97, -14.97) * mm});
            skLineSegment(sketch, "E507", {"start": v(4.97, -14.97) * mm, "end": v(4.94, -15.14) * mm});
            skLineSegment(sketch, "E508", {"start": v(4.94, -15.14) * mm, "end": v(4.92, -15.34) * mm});
            skLineSegment(sketch, "E509", {"start": v(4.92, -15.34) * mm, "end": v(4.87, -15.51) * mm});
            skLineSegment(sketch, "E510", {"start": v(4.87, -15.51) * mm, "end": v(4.82, -15.69) * mm});
            skLineSegment(sketch, "E511", {"start": v(4.82, -15.69) * mm, "end": v(4.74, -15.86) * mm});
            skLineSegment(sketch, "E512", {"start": v(4.74, -15.86) * mm, "end": v(4.64, -16.03) * mm});
            skLineSegment(sketch, "E513", {"start": v(4.64, -16.03) * mm, "end": v(4.52, -16.18) * mm});
            skLineSegment(sketch, "E514", {"start": v(4.52, -16.18) * mm, "end": v(4.4, -16.33) * mm});
            skLineSegment(sketch, "E515", {"start": v(4.4, -16.33) * mm, "end": v(4.25, -16.46) * mm});
            skLineSegment(sketch, "E516", {"start": v(4.25, -16.46) * mm, "end": v(4.1, -16.58) * mm});
            skLineSegment(sketch, "E517", {"start": v(4.1, -16.58) * mm, "end": v(3.92, -16.68) * mm});
            skLineSegment(sketch, "E518", {"start": v(3.92, -16.68) * mm, "end": v(3.75, -16.75) * mm});
            skLineSegment(sketch, "E519", {"start": v(3.75, -16.75) * mm, "end": v(3.58, -16.8) * mm});
            skLineSegment(sketch, "E520", {"start": v(3.58, -16.8) * mm, "end": v(3.4, -16.85) * mm});
            skLineSegment(sketch, "E521", {"start": v(3.4, -16.85) * mm, "end": v(3.2, -16.88) * mm});
            skLineSegment(sketch, "E522", {"start": v(3.2, -16.88) * mm, "end": v(3.03, -16.9) * mm});
            skLineSegment(sketch, "E523", {"start": v(3.03, -16.9) * mm, "end": v(-2.3, -16.9) * mm});
            skLineSegment(sketch, "E524", {"start": v(-2.3, -16.9) * mm, "end": v(-3.05, -16.85) * mm});
            skLineSegment(sketch, "E525", {"start": v(-3.05, -16.85) * mm, "end": v(-3.74, -16.75) * mm});
            skLineSegment(sketch, "E526", {"start": v(-3.74, -16.75) * mm, "end": v(-4.44, -16.58) * mm});
            skLineSegment(sketch, "E527", {"start": v(-4.44, -16.58) * mm, "end": v(-5.08, -16.36) * mm});
            skLineSegment(sketch, "E528", {"start": v(-5.08, -16.36) * mm, "end": v(-5.7, -16.06) * mm});
            skLineSegment(sketch, "E529", {"start": v(-5.7, -16.06) * mm, "end": v(-6.32, -15.69) * mm});
            skLineSegment(sketch, "E530", {"start": v(-6.32, -15.69) * mm, "end": v(-6.9, -15.26) * mm});
            skLineSegment(sketch, "E531", {"start": v(-6.9, -15.26) * mm, "end": v(-7.44, -14.77) * mm});
            skLineSegment(sketch, "E532", {"start": v(-7.44, -14.77) * mm, "end": v(-7.93, -14.22) * mm});
            skLineSegment(sketch, "E533", {"start": v(-7.93, -14.22) * mm, "end": v(-8.35, -13.65) * mm});
            skLineSegment(sketch, "E534", {"start": v(-8.35, -13.65) * mm, "end": v(-8.73, -13.03) * mm});
            skLineSegment(sketch, "E535", {"start": v(-8.73, -13.03) * mm, "end": v(-9.02, -12.41) * mm});
            skLineSegment(sketch, "E536", {"start": v(-9.02, -12.41) * mm, "end": v(-9.25, -11.77) * mm});
            skLineSegment(sketch, "E537", {"start": v(-9.25, -11.77) * mm, "end": v(-9.42, -11.07) * mm});
            skLineSegment(sketch, "E538", {"start": v(-9.42, -11.07) * mm, "end": v(-9.52, -10.38) * mm});
            skLineSegment(sketch, "E539", {"start": v(11.76, -15.34) * mm, "end": v(11.74, -15.14) * mm});
            skLineSegment(sketch, "E540", {"start": v(11.74, -15.14) * mm, "end": v(11.74, -14.97) * mm});
            skLineSegment(sketch, "E541", {"start": v(11.74, -14.97) * mm, "end": v(11.74, 5.37) * mm});
            skLineSegment(sketch, "E542", {"start": v(11.74, 5.37) * mm, "end": v(11.74, 5.55) * mm});
            skLineSegment(sketch, "E543", {"start": v(11.74, 5.55) * mm, "end": v(11.76, 5.74) * mm});
            skLineSegment(sketch, "E544", {"start": v(11.76, 5.74) * mm, "end": v(11.81, 5.92) * mm});
            skLineSegment(sketch, "E545", {"start": v(11.81, 5.92) * mm, "end": v(11.89, 6.1) * mm});
            skLineSegment(sketch, "E546", {"start": v(11.89, 6.1) * mm, "end": v(11.96, 6.27) * mm});
            skLineSegment(sketch, "E547", {"start": v(11.96, 6.27) * mm, "end": v(12.06, 6.44) * mm});
            skLineSegment(sketch, "E548", {"start": v(12.06, 6.44) * mm, "end": v(12.18, 6.59) * mm});
            skLineSegment(sketch, "E549", {"start": v(12.18, 6.59) * mm, "end": v(12.3, 6.74) * mm});
            skLineSegment(sketch, "E550", {"start": v(12.3, 6.74) * mm, "end": v(12.46, 6.86) * mm});
            skLineSegment(sketch, "E551", {"start": v(12.46, 6.86) * mm, "end": v(12.6, 6.99) * mm});
            skLineSegment(sketch, "E552", {"start": v(12.6, 6.99) * mm, "end": v(12.75, 7.08) * mm});
            skLineSegment(sketch, "E553", {"start": v(12.75, 7.08) * mm, "end": v(12.93, 7.16) * mm});
            skLineSegment(sketch, "E554", {"start": v(12.93, 7.16) * mm, "end": v(13.1, 7.2) * mm});
            skLineSegment(sketch, "E555", {"start": v(13.1, 7.2) * mm, "end": v(13.28, 7.26) * mm});
            skLineSegment(sketch, "E556", {"start": v(13.28, 7.26) * mm, "end": v(13.47, 7.28) * mm});
            skLineSegment(sketch, "E557", {"start": v(13.47, 7.28) * mm, "end": v(13.67, 7.3) * mm});
            skLineSegment(sketch, "E558", {"start": v(13.67, 7.3) * mm, "end": v(27.71, 7.3) * mm});
            skLineSegment(sketch, "E559", {"start": v(27.71, 7.3) * mm, "end": v(28.43, 7.26) * mm});
            skLineSegment(sketch, "E560", {"start": v(28.43, 7.26) * mm, "end": v(29.15, 7.16) * mm});
            skLineSegment(sketch, "E561", {"start": v(29.15, 7.16) * mm, "end": v(29.82, 6.99) * mm});
            skLineSegment(sketch, "E562", {"start": v(73.3, -11.12) * mm, "end": v(73.4, -11.42) * mm});
            skLineSegment(sketch, "E563", {"start": v(73.4, -11.42) * mm, "end": v(73.55, -11.72) * mm});
            skLineSegment(sketch, "E564", {"start": v(73.55, -11.72) * mm, "end": v(73.72, -12) * mm});
            skLineSegment(sketch, "E565", {"start": v(73.72, -12) * mm, "end": v(73.92, -12.26) * mm});
            skLineSegment(sketch, "E566", {"start": v(73.92, -12.26) * mm, "end": v(74.15, -12.51) * mm});
            skLineSegment(sketch, "E567", {"start": v(74.15, -12.51) * mm, "end": v(74.42, -12.73) * mm});
            skLineSegment(sketch, "E568", {"start": v(74.42, -12.73) * mm, "end": v(74.7, -12.96) * mm});
            skLineSegment(sketch, "E569", {"start": v(74.7, -12.96) * mm, "end": v(74.96, -13.1) * mm});
            skLineSegment(sketch, "E570", {"start": v(74.96, -13.1) * mm, "end": v(75.26, -13.26) * mm});
            skLineSegment(sketch, "E571", {"start": v(75.26, -13.26) * mm, "end": v(75.56, -13.35) * mm});
            skLineSegment(sketch, "E572", {"start": v(75.56, -13.35) * mm, "end": v(75.88, -13.45) * mm});
            skLineSegment(sketch, "E573", {"start": v(75.88, -13.45) * mm, "end": v(76.2, -13.48) * mm});
            skLineSegment(sketch, "E574", {"start": v(76.2, -13.48) * mm, "end": v(76.55, -13.5) * mm});
            skLineSegment(sketch, "E575", {"start": v(76.55, -13.5) * mm, "end": v(76.9, -13.48) * mm});
            skLineSegment(sketch, "E576", {"start": v(76.9, -13.48) * mm, "end": v(77.22, -13.45) * mm});
            skLineSegment(sketch, "E577", {"start": v(77.22, -13.45) * mm, "end": v(77.54, -13.35) * mm});
            skLineSegment(sketch, "E578", {"start": v(77.54, -13.35) * mm, "end": v(77.84, -13.26) * mm});
            skLineSegment(sketch, "E579", {"start": v(77.84, -13.26) * mm, "end": v(78.14, -13.1) * mm});
            skLineSegment(sketch, "E580", {"start": v(78.14, -13.1) * mm, "end": v(78.41, -12.96) * mm});
            skLineSegment(sketch, "E581", {"start": v(78.41, -12.96) * mm, "end": v(78.69, -12.73) * mm});
            skLineSegment(sketch, "E582", {"start": v(78.69, -12.73) * mm, "end": v(78.96, -12.51) * mm});
            skLineSegment(sketch, "E583", {"start": v(78.96, -12.51) * mm, "end": v(79.18, -12.26) * mm});
            skLineSegment(sketch, "E584", {"start": v(79.18, -12.26) * mm, "end": v(79.38, -12) * mm});
            skLineSegment(sketch, "E585", {"start": v(79.38, -12) * mm, "end": v(79.55, -11.72) * mm});
            skLineSegment(sketch, "E586", {"start": v(79.55, -11.72) * mm, "end": v(79.7, -11.42) * mm});
            skLineSegment(sketch, "E587", {"start": v(79.7, -11.42) * mm, "end": v(79.8, -11.12) * mm});
            skLineSegment(sketch, "E588", {"start": v(79.8, -11.12) * mm, "end": v(79.88, -10.8) * mm});
            skLineSegment(sketch, "E589", {"start": v(79.88, -10.8) * mm, "end": v(79.93, -10.45) * mm});
            skLineSegment(sketch, "E590", {"start": v(79.93, -10.45) * mm, "end": v(79.95, -10.1) * mm});
            skLineSegment(sketch, "E591", {"start": v(79.95, -10.1) * mm, "end": v(79.95, -3.36) * mm});
            skLineSegment(sketch, "E592", {"start": v(79.95, -3.36) * mm, "end": v(79.95, -3.18) * mm});
            skLineSegment(sketch, "E593", {"start": v(79.95, -3.18) * mm, "end": v(79.98, -2.99) * mm});
            skLineSegment(sketch, "E594", {"start": v(79.98, -2.99) * mm, "end": v(80.02, -2.81) * mm});
            skLineSegment(sketch, "E595", {"start": v(80.02, -2.81) * mm, "end": v(80.07, -2.64) * mm});
            skLineSegment(sketch, "E596", {"start": v(80.07, -2.64) * mm, "end": v(80.15, -2.47) * mm});
            skLineSegment(sketch, "E597", {"start": v(80.15, -2.47) * mm, "end": v(80.25, -2.3) * mm});
            skLineSegment(sketch, "E598", {"start": v(80.25, -2.3) * mm, "end": v(80.37, -2.14) * mm});
            skLineSegment(sketch, "E599", {"start": v(80.37, -2.14) * mm, "end": v(80.5, -2) * mm});
            skLineSegment(sketch, "E600", {"start": v(80.5, -2) * mm, "end": v(80.64, -1.87) * mm});
            skLineSegment(sketch, "E601", {"start": v(80.64, -1.87) * mm, "end": v(80.8, -1.75) * mm});
            skLineSegment(sketch, "E602", {"start": v(80.8, -1.75) * mm, "end": v(80.97, -1.65) * mm});
            skLineSegment(sketch, "E603", {"start": v(80.97, -1.65) * mm, "end": v(81.14, -1.57) * mm});
            skLineSegment(sketch, "E604", {"start": v(81.14, -1.57) * mm, "end": v(81.31, -1.52) * mm});
            skLineSegment(sketch, "E605", {"start": v(81.31, -1.52) * mm, "end": v(81.49, -1.47) * mm});
            skLineSegment(sketch, "E606", {"start": v(81.49, -1.47) * mm, "end": v(81.69, -1.45) * mm});
            skLineSegment(sketch, "E607", {"start": v(81.69, -1.45) * mm, "end": v(81.89, -1.42) * mm});
            skLineSegment(sketch, "E608", {"start": v(81.89, -1.42) * mm, "end": v(82.06, -1.45) * mm});
            skLineSegment(sketch, "E609", {"start": v(82.06, -1.45) * mm, "end": v(82.26, -1.47) * mm});
            skLineSegment(sketch, "E610", {"start": v(82.26, -1.47) * mm, "end": v(82.43, -1.52) * mm});
            skLineSegment(sketch, "E611", {"start": v(82.43, -1.52) * mm, "end": v(82.6, -1.57) * mm});
            skLineSegment(sketch, "E612", {"start": v(82.6, -1.57) * mm, "end": v(82.78, -1.65) * mm});
            skLineSegment(sketch, "E613", {"start": v(82.78, -1.65) * mm, "end": v(82.95, -1.75) * mm});
            skLineSegment(sketch, "E614", {"start": v(82.95, -1.75) * mm, "end": v(83.1, -1.87) * mm});
            skLineSegment(sketch, "E615", {"start": v(83.1, -1.87) * mm, "end": v(83.25, -2) * mm});
            skLineSegment(sketch, "E616", {"start": v(83.25, -2) * mm, "end": v(83.37, -2.14) * mm});
            skLineSegment(sketch, "E617", {"start": v(83.37, -2.14) * mm, "end": v(83.5, -2.3) * mm});
            skLineSegment(sketch, "E618", {"start": v(83.5, -2.3) * mm, "end": v(83.6, -2.47) * mm});
            skLineSegment(sketch, "E619", {"start": v(83.6, -2.47) * mm, "end": v(83.67, -2.64) * mm});
            skLineSegment(sketch, "E620", {"start": v(83.67, -2.64) * mm, "end": v(83.72, -2.81) * mm});
            skLineSegment(sketch, "E621", {"start": v(83.72, -2.81) * mm, "end": v(83.77, -2.99) * mm});
            skLineSegment(sketch, "E622", {"start": v(83.77, -2.99) * mm, "end": v(83.8, -3.18) * mm});
            skLineSegment(sketch, "E623", {"start": v(83.8, -3.18) * mm, "end": v(83.82, -3.36) * mm});
            skLineSegment(sketch, "E624", {"start": v(83.82, -3.36) * mm, "end": v(83.82, -10.1) * mm});
            skLineSegment(sketch, "E625", {"start": v(83.82, -10.1) * mm, "end": v(83.77, -10.85) * mm});
            skLineSegment(sketch, "E626", {"start": v(83.77, -10.85) * mm, "end": v(83.67, -11.57) * mm});
            skLineSegment(sketch, "E627", {"start": v(83.67, -11.57) * mm, "end": v(83.5, -12.24) * mm});
            skLineSegment(sketch, "E628", {"start": v(83.5, -12.24) * mm, "end": v(83.27, -12.9) * mm});
            skLineSegment(sketch, "E629", {"start": v(83.27, -12.9) * mm, "end": v(82.98, -13.53) * mm});
            skLineSegment(sketch, "E630", {"start": v(82.98, -13.53) * mm, "end": v(82.6, -14.12) * mm});
            skLineSegment(sketch, "E631", {"start": v(82.6, -14.12) * mm, "end": v(82.18, -14.7) * mm});
            skLineSegment(sketch, "E632", {"start": v(82.18, -14.7) * mm, "end": v(81.69, -15.24) * mm});
            skLineSegment(sketch, "E633", {"start": v(81.69, -15.24) * mm, "end": v(81.14, -15.74) * mm});
            skLineSegment(sketch, "E634", {"start": v(81.14, -15.74) * mm, "end": v(80.57, -16.18) * mm});
            skLineSegment(sketch, "E635", {"start": v(80.57, -16.18) * mm, "end": v(79.95, -16.53) * mm});
            skLineSegment(sketch, "E636", {"start": v(79.95, -16.53) * mm, "end": v(79.33, -16.85) * mm});
            skLineSegment(sketch, "E637", {"start": v(79.33, -16.85) * mm, "end": v(78.69, -17.08) * mm});
            skLineSegment(sketch, "E638", {"start": v(78.69, -17.08) * mm, "end": v(78, -17.25) * mm});
            skLineSegment(sketch, "E639", {"start": v(78, -17.25) * mm, "end": v(77.3, -17.35) * mm});
            skLineSegment(sketch, "E640", {"start": v(77.3, -17.35) * mm, "end": v(76.55, -17.37) * mm});
            skLineSegment(sketch, "E641", {"start": v(76.55, -17.37) * mm, "end": v(75.8, -17.35) * mm});
            skLineSegment(sketch, "E642", {"start": v(75.8, -17.35) * mm, "end": v(75.11, -17.25) * mm});
            skLineSegment(sketch, "E643", {"start": v(75.11, -17.25) * mm, "end": v(74.42, -17.08) * mm});
            skLineSegment(sketch, "E644", {"start": v(74.42, -17.08) * mm, "end": v(73.77, -16.85) * mm});
            skLineSegment(sketch, "E645", {"start": v(73.77, -16.85) * mm, "end": v(73.15, -16.53) * mm});
            skLineSegment(sketch, "E646", {"start": v(73.15, -16.53) * mm, "end": v(72.53, -16.18) * mm});
            skLineSegment(sketch, "E647", {"start": v(72.53, -16.18) * mm, "end": v(71.96, -15.74) * mm});
            skLineSegment(sketch, "E648", {"start": v(71.96, -15.74) * mm, "end": v(71.42, -15.24) * mm});
            skLineSegment(sketch, "E649", {"start": v(71.42, -15.24) * mm, "end": v(70.92, -14.7) * mm});
            skLineSegment(sketch, "E650", {"start": v(70.92, -14.7) * mm, "end": v(70.5, -14.12) * mm});
            skLineSegment(sketch, "E651", {"start": v(70.5, -14.12) * mm, "end": v(70.13, -13.53) * mm});
            skLineSegment(sketch, "E652", {"start": v(70.13, -13.53) * mm, "end": v(69.83, -12.9) * mm});
            skLineSegment(sketch, "E653", {"start": v(69.83, -12.9) * mm, "end": v(69.6, -12.24) * mm});
            skLineSegment(sketch, "E654", {"start": v(69.6, -12.24) * mm, "end": v(69.43, -11.57) * mm});
            skLineSegment(sketch, "E655", {"start": v(69.43, -11.57) * mm, "end": v(69.33, -10.85) * mm});
            skLineSegment(sketch, "E656", {"start": v(69.33, 9.99) * mm, "end": v(69.43, 10.7) * mm});
            skLineSegment(sketch, "E657", {"start": v(69.43, 10.7) * mm, "end": v(69.6, 11.38) * mm});
            skLineSegment(sketch, "E658", {"start": v(69.6, 11.38) * mm, "end": v(69.83, 12.05) * mm});
            skLineSegment(sketch, "E659", {"start": v(69.83, 12.05) * mm, "end": v(70.13, 12.67) * mm});
            skLineSegment(sketch, "E660", {"start": v(70.13, 12.67) * mm, "end": v(70.5, 13.26) * mm});
            skLineSegment(sketch, "E661", {"start": v(70.5, 13.26) * mm, "end": v(70.92, 13.83) * mm});
            skLineSegment(sketch, "E662", {"start": v(70.92, 13.83) * mm, "end": v(71.42, 14.38) * mm});
            skLineSegment(sketch, "E663", {"start": v(71.42, 14.38) * mm, "end": v(71.96, 14.87) * mm});
            skLineSegment(sketch, "E664", {"start": v(71.96, 14.87) * mm, "end": v(72.53, 15.32) * mm});
            skLineSegment(sketch, "E665", {"start": v(72.53, 15.32) * mm, "end": v(73.15, 15.67) * mm});
            skLineSegment(sketch, "E666", {"start": v(73.15, 15.67) * mm, "end": v(73.77, 15.99) * mm});
            skLineSegment(sketch, "E667", {"start": v(73.77, 15.99) * mm, "end": v(74.42, 16.21) * mm});
            skLineSegment(sketch, "E668", {"start": v(74.42, 16.21) * mm, "end": v(75.11, 16.39) * mm});
            skLineSegment(sketch, "E669", {"start": v(75.11, 16.39) * mm, "end": v(75.8, 16.49) * mm});
            skLineSegment(sketch, "E670", {"start": v(75.8, 16.49) * mm, "end": v(76.55, 16.51) * mm});
            skLineSegment(sketch, "E671", {"start": v(76.55, 16.51) * mm, "end": v(77.3, 16.49) * mm});
            skLineSegment(sketch, "E672", {"start": v(77.3, 16.49) * mm, "end": v(78, 16.39) * mm});
            skLineSegment(sketch, "E673", {"start": v(78, 16.39) * mm, "end": v(78.69, 16.21) * mm});
            skLineSegment(sketch, "E674", {"start": v(78.69, 16.21) * mm, "end": v(79.33, 15.99) * mm});
            skLineSegment(sketch, "E675", {"start": v(79.33, 15.99) * mm, "end": v(79.95, 15.67) * mm});
            skLineSegment(sketch, "E676", {"start": v(79.95, 15.67) * mm, "end": v(80.57, 15.32) * mm});
            skLineSegment(sketch, "E677", {"start": v(80.57, 15.32) * mm, "end": v(81.14, 14.87) * mm});
            skLineSegment(sketch, "E678", {"start": v(81.14, 14.87) * mm, "end": v(81.69, 14.38) * mm});
            skLineSegment(sketch, "E679", {"start": v(81.69, 14.38) * mm, "end": v(82.18, 13.83) * mm});
            skLineSegment(sketch, "E680", {"start": v(82.18, 13.83) * mm, "end": v(82.6, 13.26) * mm});
            skLineSegment(sketch, "E681", {"start": v(82.6, 13.26) * mm, "end": v(82.98, 12.67) * mm});
            skLineSegment(sketch, "E682", {"start": v(82.98, 12.67) * mm, "end": v(83.27, 12.05) * mm});
            skLineSegment(sketch, "E683", {"start": v(83.27, 12.05) * mm, "end": v(83.5, 11.38) * mm});
            skLineSegment(sketch, "E684", {"start": v(83.5, 11.38) * mm, "end": v(83.67, 10.7) * mm});
            skLineSegment(sketch, "E685", {"start": v(83.67, 10.7) * mm, "end": v(83.77, 9.99) * mm});
            skLineSegment(sketch, "E686", {"start": v(83.77, 9.99) * mm, "end": v(83.82, 9.24) * mm});
            skLineSegment(sketch, "E687", {"start": v(83.82, 9.24) * mm, "end": v(83.82, 2.5) * mm});
            skLineSegment(sketch, "E688", {"start": v(83.82, 2.5) * mm, "end": v(83.8, 2.32) * mm});
            skLineSegment(sketch, "E689", {"start": v(83.8, 2.32) * mm, "end": v(83.77, 2.12) * mm});
            skLineSegment(sketch, "E690", {"start": v(83.77, 2.12) * mm, "end": v(83.72, 1.95) * mm});
            skLineSegment(sketch, "E691", {"start": v(83.72, 1.95) * mm, "end": v(83.67, 1.78) * mm});
            skLineSegment(sketch, "E692", {"start": v(83.67, 1.78) * mm, "end": v(83.6, 1.6) * mm});
            skLineSegment(sketch, "E693", {"start": v(83.6, 1.6) * mm, "end": v(83.5, 1.43) * mm});
            skLineSegment(sketch, "E694", {"start": v(83.5, 1.43) * mm, "end": v(83.37, 1.28) * mm});
            skLineSegment(sketch, "E695", {"start": v(83.37, 1.28) * mm, "end": v(83.25, 1.13) * mm});
            skLineSegment(sketch, "E696", {"start": v(83.25, 1.13) * mm, "end": v(83.1, 1) * mm});
            skLineSegment(sketch, "E697", {"start": v(83.1, 1) * mm, "end": v(82.95, 0.88) * mm});
            skLineSegment(sketch, "E698", {"start": v(82.95, 0.88) * mm, "end": v(82.78, 0.78) * mm});
            skLineSegment(sketch, "E699", {"start": v(82.78, 0.78) * mm, "end": v(82.6, 0.7) * mm});
            skLineSegment(sketch, "E700", {"start": v(82.6, 0.7) * mm, "end": v(82.43, 0.66) * mm});
            skLineSegment(sketch, "E701", {"start": v(82.43, 0.66) * mm, "end": v(82.26, 0.61) * mm});
            skLineSegment(sketch, "E702", {"start": v(82.26, 0.61) * mm, "end": v(82.06, 0.59) * mm});
            skLineSegment(sketch, "E703", {"start": v(82.06, 0.59) * mm, "end": v(81.89, 0.56) * mm});
            skLineSegment(sketch, "E704", {"start": v(81.89, 0.56) * mm, "end": v(81.69, 0.59) * mm});
            skLineSegment(sketch, "E705", {"start": v(81.69, 0.59) * mm, "end": v(81.49, 0.61) * mm});
            skLineSegment(sketch, "E706", {"start": v(81.49, 0.61) * mm, "end": v(81.31, 0.66) * mm});
            skLineSegment(sketch, "E707", {"start": v(81.31, 0.66) * mm, "end": v(81.14, 0.7) * mm});
            skLineSegment(sketch, "E708", {"start": v(81.14, 0.7) * mm, "end": v(80.97, 0.78) * mm});
            skLineSegment(sketch, "E709", {"start": v(80.97, 0.78) * mm, "end": v(80.8, 0.88) * mm});
            skLineSegment(sketch, "E710", {"start": v(80.8, 0.88) * mm, "end": v(80.64, 1) * mm});
            skLineSegment(sketch, "E711", {"start": v(80.64, 1) * mm, "end": v(80.5, 1.13) * mm});
            skLineSegment(sketch, "E712", {"start": v(80.5, 1.13) * mm, "end": v(80.37, 1.28) * mm});
            skLineSegment(sketch, "E713", {"start": v(80.37, 1.28) * mm, "end": v(80.25, 1.43) * mm});
            skLineSegment(sketch, "E714", {"start": v(80.25, 1.43) * mm, "end": v(80.15, 1.6) * mm});
            skLineSegment(sketch, "E715", {"start": v(80.15, 1.6) * mm, "end": v(80.07, 1.78) * mm});
            skLineSegment(sketch, "E716", {"start": v(80.07, 1.78) * mm, "end": v(80.02, 1.95) * mm});
            skLineSegment(sketch, "E717", {"start": v(80.02, 1.95) * mm, "end": v(79.98, 2.12) * mm});
            skLineSegment(sketch, "E718", {"start": v(79.98, 2.12) * mm, "end": v(79.95, 2.32) * mm});
            skLineSegment(sketch, "E719", {"start": v(79.95, 2.32) * mm, "end": v(79.95, 2.5) * mm});
            skLineSegment(sketch, "E720", {"start": v(79.95, 2.5) * mm, "end": v(79.95, 9.24) * mm});
            skLineSegment(sketch, "E721", {"start": v(79.95, 9.24) * mm, "end": v(79.93, 9.59) * mm});
            skLineSegment(sketch, "E722", {"start": v(79.93, 9.59) * mm, "end": v(79.88, 9.94) * mm});
            skLineSegment(sketch, "E723", {"start": v(79.88, 9.94) * mm, "end": v(79.8, 10.26) * mm});
            skLineSegment(sketch, "E724", {"start": v(79.8, 10.26) * mm, "end": v(79.7, 10.56) * mm});
            skLineSegment(sketch, "E725", {"start": v(79.7, 10.56) * mm, "end": v(79.55, 10.85) * mm});
            skLineSegment(sketch, "E726", {"start": v(79.55, 10.85) * mm, "end": v(79.38, 11.13) * mm});
            skLineSegment(sketch, "E727", {"start": v(79.38, 11.13) * mm, "end": v(79.18, 11.4) * mm});
            skLineSegment(sketch, "E728", {"start": v(79.18, 11.4) * mm, "end": v(78.96, 11.65) * mm});
            skLineSegment(sketch, "E729", {"start": v(78.96, 11.65) * mm, "end": v(78.69, 11.87) * mm});
            skLineSegment(sketch, "E730", {"start": v(78.69, 11.87) * mm, "end": v(78.41, 12.07) * mm});
            skLineSegment(sketch, "E731", {"start": v(78.41, 12.07) * mm, "end": v(78.14, 12.24) * mm});
            skLineSegment(sketch, "E732", {"start": v(78.14, 12.24) * mm, "end": v(77.84, 12.4) * mm});
            skLineSegment(sketch, "E733", {"start": v(77.84, 12.4) * mm, "end": v(77.54, 12.5) * mm});
            skLineSegment(sketch, "E734", {"start": v(77.54, 12.5) * mm, "end": v(77.22, 12.57) * mm});
            skLineSegment(sketch, "E735", {"start": v(77.22, 12.57) * mm, "end": v(76.9, 12.62) * mm});
            skLineSegment(sketch, "E736", {"start": v(76.9, 12.62) * mm, "end": v(76.55, 12.64) * mm});
            skLineSegment(sketch, "E737", {"start": v(76.55, 12.64) * mm, "end": v(76.2, 12.62) * mm});
            skLineSegment(sketch, "E738", {"start": v(76.2, 12.62) * mm, "end": v(75.88, 12.57) * mm});
            skLineSegment(sketch, "E739", {"start": v(75.88, 12.57) * mm, "end": v(75.56, 12.5) * mm});
            skLineSegment(sketch, "E740", {"start": v(75.56, 12.5) * mm, "end": v(75.26, 12.4) * mm});
            skLineSegment(sketch, "E741", {"start": v(75.26, 12.4) * mm, "end": v(74.96, 12.24) * mm});
            skLineSegment(sketch, "E742", {"start": v(74.96, 12.24) * mm, "end": v(74.7, 12.07) * mm});
            skLineSegment(sketch, "E743", {"start": v(74.7, 12.07) * mm, "end": v(74.42, 11.87) * mm});
            skLineSegment(sketch, "E744", {"start": v(74.42, 11.87) * mm, "end": v(74.15, 11.65) * mm});
            skLineSegment(sketch, "E745", {"start": v(74.15, 11.65) * mm, "end": v(73.92, 11.4) * mm});
            skLineSegment(sketch, "E746", {"start": v(73.92, 11.4) * mm, "end": v(73.72, 11.13) * mm});
            skLineSegment(sketch, "E747", {"start": v(73.72, 11.13) * mm, "end": v(73.55, 10.85) * mm});
            skLineSegment(sketch, "E748", {"start": v(73.55, 10.85) * mm, "end": v(73.4, 10.56) * mm});
            skLineSegment(sketch, "E749", {"start": v(73.4, 10.56) * mm, "end": v(73.3, 10.26) * mm});
            skLineSegment(sketch, "E750", {"start": v(73.3, 10.26) * mm, "end": v(73.23, 9.94) * mm});
            skLineSegment(sketch, "E751", {"start": v(73.23, 9.94) * mm, "end": v(73.18, 9.59) * mm});
            skLineSegment(sketch, "E752", {"start": v(73.18, 9.59) * mm, "end": v(73.15, 9.24) * mm});
            skLineSegment(sketch, "E753", {"start": v(73.15, 9.24) * mm, "end": v(73.15, 2.5) * mm});
            skLineSegment(sketch, "E754", {"start": v(73.15, 2.5) * mm, "end": v(73.15, 2.32) * mm});
            skLineSegment(sketch, "E755", {"start": v(73.15, 2.32) * mm, "end": v(73.13, 2.12) * mm});
            skLineSegment(sketch, "E756", {"start": v(73.13, 2.12) * mm, "end": v(73.08, 1.95) * mm});
            skLineSegment(sketch, "E757", {"start": v(73.08, 1.95) * mm, "end": v(73.03, 1.78) * mm});
            skLineSegment(sketch, "E758", {"start": v(73.03, 1.78) * mm, "end": v(72.96, 1.6) * mm});
            skLineSegment(sketch, "E759", {"start": v(72.96, 1.6) * mm, "end": v(72.86, 1.43) * mm});
            skLineSegment(sketch, "E760", {"start": v(72.86, 1.43) * mm, "end": v(72.73, 1.28) * mm});
            skLineSegment(sketch, "E761", {"start": v(72.73, 1.28) * mm, "end": v(72.6, 1.13) * mm});
            skLineSegment(sketch, "E762", {"start": v(72.6, 1.13) * mm, "end": v(72.46, 1) * mm});
            skLineSegment(sketch, "E763", {"start": v(72.46, 1) * mm, "end": v(72.31, 0.88) * mm});
            skLineSegment(sketch, "E764", {"start": v(72.31, 0.88) * mm, "end": v(72.14, 0.78) * mm});
            skLineSegment(sketch, "E765", {"start": v(72.14, 0.78) * mm, "end": v(71.96, 0.7) * mm});
            skLineSegment(sketch, "E766", {"start": v(71.96, 0.7) * mm, "end": v(71.79, 0.66) * mm});
            skLineSegment(sketch, "E767", {"start": v(71.79, 0.66) * mm, "end": v(71.62, 0.61) * mm});
            skLineSegment(sketch, "E768", {"start": v(71.62, 0.61) * mm, "end": v(71.42, 0.59) * mm});
            skLineSegment(sketch, "E769", {"start": v(71.42, 0.59) * mm, "end": v(71.22, 0.56) * mm});
            skLineSegment(sketch, "E770", {"start": v(71.22, 0.56) * mm, "end": v(71.05, 0.59) * mm});
            skLineSegment(sketch, "E771", {"start": v(71.05, 0.59) * mm, "end": v(70.85, 0.61) * mm});
            skLineSegment(sketch, "E772", {"start": v(70.85, 0.61) * mm, "end": v(70.67, 0.66) * mm});
            skLineSegment(sketch, "E773", {"start": v(70.67, 0.66) * mm, "end": v(70.5, 0.7) * mm});
            skLineSegment(sketch, "E774", {"start": v(70.5, 0.7) * mm, "end": v(70.33, 0.78) * mm});
            skLineSegment(sketch, "E775", {"start": v(70.33, 0.78) * mm, "end": v(70.15, 0.88) * mm});
            skLineSegment(sketch, "E776", {"start": v(70.15, 0.88) * mm, "end": v(70, 1) * mm});
            skLineSegment(sketch, "E777", {"start": v(70, 1) * mm, "end": v(69.85, 1.13) * mm});
            skLineSegment(sketch, "E778", {"start": v(69.85, 1.13) * mm, "end": v(69.73, 1.28) * mm});
            skLineSegment(sketch, "E779", {"start": v(69.73, 1.28) * mm, "end": v(69.6, 1.43) * mm});
            skLineSegment(sketch, "E780", {"start": v(69.6, 1.43) * mm, "end": v(69.5, 1.6) * mm});
            skLineSegment(sketch, "E781", {"start": v(69.5, 1.6) * mm, "end": v(69.43, 1.78) * mm});
            skLineSegment(sketch, "E782", {"start": v(69.43, 1.78) * mm, "end": v(69.38, 1.95) * mm});
            skLineSegment(sketch, "E783", {"start": v(69.38, 1.95) * mm, "end": v(69.33, 2.12) * mm});
            skLineSegment(sketch, "E784", {"start": v(69.33, 2.12) * mm, "end": v(69.3, 2.32) * mm});
            skLineSegment(sketch, "E785", {"start": v(69.3, 2.32) * mm, "end": v(69.28, 2.5) * mm});
            skLineSegment(sketch, "E786", {"start": v(69.28, 2.5) * mm, "end": v(69.28, 9.24) * mm});
            skLineSegment(sketch, "E787", {"start": v(69.28, 9.24) * mm, "end": v(69.33, 9.99) * mm});
            skLineSegment(sketch, "E788", {"start": v(87.71, -6.66) * mm, "end": v(87.69, -6.46) * mm});
            skLineSegment(sketch, "E789", {"start": v(87.69, -6.46) * mm, "end": v(87.69, -6.26) * mm});
            skLineSegment(sketch, "E790", {"start": v(87.69, -6.26) * mm, "end": v(87.69, -6.19) * mm});
            skLineSegment(sketch, "E791", {"start": v(87.69, -6.19) * mm, "end": v(87.69, -6.11) * mm});
            skLineSegment(sketch, "E792", {"start": v(87.69, -6.11) * mm, "end": v(87.69, -6.04) * mm});
            skLineSegment(sketch, "E793", {"start": v(87.69, -6.04) * mm, "end": v(87.69, -5.96) * mm});
            skLineSegment(sketch, "E794", {"start": v(87.69, -5.96) * mm, "end": v(87.71, -5.89) * mm});
            skLineSegment(sketch, "E795", {"start": v(87.71, -5.89) * mm, "end": v(87.74, -5.84) * mm});
            skLineSegment(sketch, "E796", {"start": v(87.74, -5.84) * mm, "end": v(87.74, -5.76) * mm});
            skLineSegment(sketch, "E797", {"start": v(87.74, -5.76) * mm, "end": v(87.76, -5.71) * mm});
            skLineSegment(sketch, "E798", {"start": v(87.76, -5.71) * mm, "end": v(91.56, 14.08) * mm});
            skLineSegment(sketch, "E799", {"start": v(91.56, 14.08) * mm, "end": v(91.58, 14.28) * mm});
            skLineSegment(sketch, "E800", {"start": v(91.58, 14.28) * mm, "end": v(91.63, 14.48) * mm});
            skLineSegment(sketch, "E801", {"start": v(91.63, 14.48) * mm, "end": v(91.68, 14.65) * mm});
            skLineSegment(sketch, "E802", {"start": v(91.68, 14.65) * mm, "end": v(91.76, 14.82) * mm});
            skLineSegment(sketch, "E803", {"start": v(91.76, 14.82) * mm, "end": v(91.83, 15) * mm});
            skLineSegment(sketch, "E804", {"start": v(91.83, 15) * mm, "end": v(91.93, 15.15) * mm});
            skLineSegment(sketch, "E805", {"start": v(91.93, 15.15) * mm, "end": v(92.03, 15.3) * mm});
            skLineSegment(sketch, "E806", {"start": v(92.03, 15.3) * mm, "end": v(92.15, 15.44) * mm});
            skLineSegment(sketch, "E807", {"start": v(92.15, 15.44) * mm, "end": v(92.3, 15.57) * mm});
            skLineSegment(sketch, "E808", {"start": v(92.3, 15.57) * mm, "end": v(92.45, 15.7) * mm});
            skLineSegment(sketch, "E809", {"start": v(92.45, 15.7) * mm, "end": v(92.6, 15.8) * mm});
            skLineSegment(sketch, "E810", {"start": v(92.6, 15.8) * mm, "end": v(92.75, 15.87) * mm});
            skLineSegment(sketch, "E811", {"start": v(92.75, 15.87) * mm, "end": v(92.92, 15.91) * mm});
            skLineSegment(sketch, "E812", {"start": v(92.92, 15.91) * mm, "end": v(93.1, 15.96) * mm});
            skLineSegment(sketch, "E813", {"start": v(93.1, 15.96) * mm, "end": v(93.3, 15.99) * mm});
            skLineSegment(sketch, "E814", {"start": v(93.3, 15.99) * mm, "end": v(93.5, 15.99) * mm});
            skLineSegment(sketch, "E815", {"start": v(93.5, 15.99) * mm, "end": v(93.67, 15.99) * mm});
            skLineSegment(sketch, "E816", {"start": v(93.67, 15.99) * mm, "end": v(93.87, 15.96) * mm});
            skLineSegment(sketch, "E817", {"start": v(93.87, 15.96) * mm, "end": v(94.04, 15.91) * mm});
            skLineSegment(sketch, "E818", {"start": v(94.04, 15.91) * mm, "end": v(94.21, 15.87) * mm});
            skLineSegment(sketch, "E819", {"start": v(94.21, 15.87) * mm, "end": v(94.39, 15.8) * mm});
            skLineSegment(sketch, "E820", {"start": v(94.39, 15.8) * mm, "end": v(94.56, 15.7) * mm});
            skLineSegment(sketch, "E821", {"start": v(94.56, 15.7) * mm, "end": v(94.7, 15.57) * mm});
            skLineSegment(sketch, "E822", {"start": v(94.7, 15.57) * mm, "end": v(94.86, 15.44) * mm});
            skLineSegment(sketch, "E823", {"start": v(94.86, 15.44) * mm, "end": v(94.98, 15.3) * mm});
            skLineSegment(sketch, "E824", {"start": v(94.98, 15.3) * mm, "end": v(95.1, 15.15) * mm});
            skLineSegment(sketch, "E825", {"start": v(95.1, 15.15) * mm, "end": v(95.2, 14.97) * mm});
            skLineSegment(sketch, "E826", {"start": v(95.2, 14.97) * mm, "end": v(95.28, 14.8) * mm});
            skLineSegment(sketch, "E827", {"start": v(95.28, 14.8) * mm, "end": v(95.33, 14.62) * mm});
            skLineSegment(sketch, "E828", {"start": v(95.33, 14.62) * mm, "end": v(95.38, 14.45) * mm});
            skLineSegment(sketch, "E829", {"start": v(95.38, 14.45) * mm, "end": v(95.4, 14.25) * mm});
            skLineSegment(sketch, "E830", {"start": v(95.4, 14.25) * mm, "end": v(95.43, 14.05) * mm});
            skLineSegment(sketch, "E831", {"start": v(95.43, 14.05) * mm, "end": v(95.4, 14) * mm});
            skLineSegment(sketch, "E832", {"start": v(95.4, 14) * mm, "end": v(95.4, 13.93) * mm});
            skLineSegment(sketch, "E833", {"start": v(95.4, 13.93) * mm, "end": v(95.4, 13.86) * mm});
            skLineSegment(sketch, "E834", {"start": v(95.4, 13.86) * mm, "end": v(95.4, 13.78) * mm});
            skLineSegment(sketch, "E835", {"start": v(95.4, 13.78) * mm, "end": v(95.4, 13.7) * mm});
            skLineSegment(sketch, "E836", {"start": v(95.4, 13.7) * mm, "end": v(95.38, 13.63) * mm});
            skLineSegment(sketch, "E837", {"start": v(95.38, 13.63) * mm, "end": v(95.38, 13.58) * mm});
            skLineSegment(sketch, "E838", {"start": v(95.38, 13.58) * mm, "end": v(95.38, 13.5) * mm});
            skLineSegment(sketch, "E839", {"start": v(95.38, 13.5) * mm, "end": v(91.96, -4.33) * mm});
            skLineSegment(sketch, "E840", {"start": v(91.96, -4.33) * mm, "end": v(98.8, -4.33) * mm});
            skLineSegment(sketch, "E841", {"start": v(98.8, -4.33) * mm, "end": v(98.8, 8.25) * mm});
            skLineSegment(sketch, "E842", {"start": v(98.8, 8.25) * mm, "end": v(98.8, 8.42) * mm});
            skLineSegment(sketch, "E843", {"start": v(98.8, 8.42) * mm, "end": v(98.83, 8.62) * mm});
            skLineSegment(sketch, "E844", {"start": v(98.83, 8.62) * mm, "end": v(98.88, 8.8) * mm});
            skLineSegment(sketch, "E845", {"start": v(98.88, 8.8) * mm, "end": v(98.95, 8.97) * mm});
            skLineSegment(sketch, "E846", {"start": v(98.95, 8.97) * mm, "end": v(99.03, 9.14) * mm});
            skLineSegment(sketch, "E847", {"start": v(99.03, 9.14) * mm, "end": v(99.12, 9.32) * mm});
            skLineSegment(sketch, "E848", {"start": v(99.12, 9.32) * mm, "end": v(99.25, 9.47) * mm});
            skLineSegment(sketch, "E849", {"start": v(99.25, 9.47) * mm, "end": v(99.37, 9.61) * mm});
            skLineSegment(sketch, "E850", {"start": v(99.37, 9.61) * mm, "end": v(99.52, 9.74) * mm});
            skLineSegment(sketch, "E851", {"start": v(99.52, 9.74) * mm, "end": v(99.67, 9.86) * mm});
            skLineSegment(sketch, "E852", {"start": v(99.67, 9.86) * mm, "end": v(99.82, 9.96) * mm});
            skLineSegment(sketch, "E853", {"start": v(99.82, 9.96) * mm, "end": v(100, 10.04) * mm});
            skLineSegment(sketch, "E854", {"start": v(100, 10.04) * mm, "end": v(100.17, 10.09) * mm});
            skLineSegment(sketch, "E855", {"start": v(100.17, 10.09) * mm, "end": v(100.34, 10.14) * mm});
            skLineSegment(sketch, "E856", {"start": v(100.34, 10.14) * mm, "end": v(100.54, 10.16) * mm});
            skLineSegment(sketch, "E857", {"start": v(100.54, 10.16) * mm, "end": v(100.74, 10.18) * mm});
            skLineSegment(sketch, "E858", {"start": v(100.74, 10.18) * mm, "end": v(100.94, 10.16) * mm});
            skLineSegment(sketch, "E859", {"start": v(100.94, 10.16) * mm, "end": v(101.13, 10.14) * mm});
            skLineSegment(sketch, "E860", {"start": v(101.13, 10.14) * mm, "end": v(101.3, 10.09) * mm});
            skLineSegment(sketch, "E861", {"start": v(101.3, 10.09) * mm, "end": v(101.48, 10.04) * mm});
            skLineSegment(sketch, "E862", {"start": v(101.48, 10.04) * mm, "end": v(101.65, 9.96) * mm});
            skLineSegment(sketch, "E863", {"start": v(101.65, 9.96) * mm, "end": v(101.8, 9.86) * mm});
            skLineSegment(sketch, "E864", {"start": v(101.8, 9.86) * mm, "end": v(101.95, 9.74) * mm});
            skLineSegment(sketch, "E865", {"start": v(101.95, 9.74) * mm, "end": v(102.1, 9.61) * mm});
            skLineSegment(sketch, "E866", {"start": v(102.1, 9.61) * mm, "end": v(102.23, 9.47) * mm});
            skLineSegment(sketch, "E867", {"start": v(102.23, 9.47) * mm, "end": v(102.35, 9.32) * mm});
            skLineSegment(sketch, "E868", {"start": v(102.35, 9.32) * mm, "end": v(102.45, 9.14) * mm});
            skLineSegment(sketch, "E869", {"start": v(102.45, 9.14) * mm, "end": v(102.52, 8.97) * mm});
            skLineSegment(sketch, "E870", {"start": v(102.52, 8.97) * mm, "end": v(102.6, 8.8) * mm});
            skLineSegment(sketch, "E871", {"start": v(102.6, 8.8) * mm, "end": v(102.65, 8.62) * mm});
            skLineSegment(sketch, "E872", {"start": v(102.65, 8.62) * mm, "end": v(102.67, 8.42) * mm});
            skLineSegment(sketch, "E873", {"start": v(102.67, 8.42) * mm, "end": v(102.67, 8.25) * mm});
            skLineSegment(sketch, "E874", {"start": v(102.67, 8.25) * mm, "end": v(102.67, -14.97) * mm});
            skLineSegment(sketch, "E875", {"start": v(102.67, -14.97) * mm, "end": v(102.67, -15.17) * mm});
            skLineSegment(sketch, "E876", {"start": v(102.67, -15.17) * mm, "end": v(102.65, -15.36) * mm});
            skLineSegment(sketch, "E877", {"start": v(102.65, -15.36) * mm, "end": v(102.6, -15.54) * mm});
            skLineSegment(sketch, "E878", {"start": v(102.6, -15.54) * mm, "end": v(102.52, -15.71) * mm});
            skLineSegment(sketch, "E879", {"start": v(102.52, -15.71) * mm, "end": v(102.45, -15.88) * mm});
            skLineSegment(sketch, "E880", {"start": v(102.45, -15.88) * mm, "end": v(102.35, -16.06) * mm});
            skLineSegment(sketch, "E881", {"start": v(102.35, -16.06) * mm, "end": v(102.23, -16.2) * mm});
            skLineSegment(sketch, "E882", {"start": v(102.23, -16.2) * mm, "end": v(102.1, -16.36) * mm});
            skLineSegment(sketch, "E883", {"start": v(102.1, -16.36) * mm, "end": v(101.95, -16.48) * mm});
            skLineSegment(sketch, "E884", {"start": v(101.95, -16.48) * mm, "end": v(101.8, -16.6) * mm});
            skLineSegment(sketch, "E885", {"start": v(101.8, -16.6) * mm, "end": v(101.65, -16.7) * mm});
            skLineSegment(sketch, "E886", {"start": v(101.65, -16.7) * mm, "end": v(101.48, -16.78) * mm});
            skLineSegment(sketch, "E887", {"start": v(101.48, -16.78) * mm, "end": v(101.3, -16.83) * mm});
            skLineSegment(sketch, "E888", {"start": v(101.3, -16.83) * mm, "end": v(101.13, -16.88) * mm});
            skLineSegment(sketch, "E889", {"start": v(101.13, -16.88) * mm, "end": v(100.94, -16.9) * mm});
            skLineSegment(sketch, "E890", {"start": v(100.94, -16.9) * mm, "end": v(100.74, -16.9) * mm});
            skLineSegment(sketch, "E891", {"start": v(100.74, -16.9) * mm, "end": v(100.54, -16.9) * mm});
            skLineSegment(sketch, "E892", {"start": v(100.54, -16.9) * mm, "end": v(100.34, -16.88) * mm});
            skLineSegment(sketch, "E893", {"start": v(100.34, -16.88) * mm, "end": v(100.17, -16.83) * mm});
            skLineSegment(sketch, "E894", {"start": v(100.17, -16.83) * mm, "end": v(100, -16.78) * mm});
            skLineSegment(sketch, "E895", {"start": v(100, -16.78) * mm, "end": v(99.82, -16.7) * mm});
            skLineSegment(sketch, "E896", {"start": v(99.82, -16.7) * mm, "end": v(99.67, -16.6) * mm});
            skLineSegment(sketch, "E897", {"start": v(99.67, -16.6) * mm, "end": v(99.52, -16.48) * mm});
            skLineSegment(sketch, "E898", {"start": v(99.52, -16.48) * mm, "end": v(99.37, -16.36) * mm});
            skLineSegment(sketch, "E899", {"start": v(99.37, -16.36) * mm, "end": v(99.25, -16.2) * mm});
            skLineSegment(sketch, "E900", {"start": v(99.25, -16.2) * mm, "end": v(99.12, -16.06) * mm});
            skLineSegment(sketch, "E901", {"start": v(99.12, -16.06) * mm, "end": v(99.03, -15.88) * mm});
            skLineSegment(sketch, "E902", {"start": v(99.03, -15.88) * mm, "end": v(98.95, -15.71) * mm});
            skLineSegment(sketch, "E903", {"start": v(98.95, -15.71) * mm, "end": v(98.88, -15.54) * mm});
            skLineSegment(sketch, "E904", {"start": v(98.88, -15.54) * mm, "end": v(98.83, -15.36) * mm});
            skLineSegment(sketch, "E905", {"start": v(98.83, -15.36) * mm, "end": v(98.8, -15.17) * mm});
            skLineSegment(sketch, "E906", {"start": v(98.8, -15.17) * mm, "end": v(98.8, -14.97) * mm});
            skLineSegment(sketch, "E907", {"start": v(98.8, -14.97) * mm, "end": v(98.8, -8.2) * mm});
            skLineSegment(sketch, "E908", {"start": v(98.8, -8.2) * mm, "end": v(89.62, -8.2) * mm});
            skLineSegment(sketch, "E909", {"start": v(89.62, -8.2) * mm, "end": v(89.43, -8.2) * mm});
            skLineSegment(sketch, "E910", {"start": v(89.43, -8.2) * mm, "end": v(89.23, -8.17) * mm});
            skLineSegment(sketch, "E911", {"start": v(89.23, -8.17) * mm, "end": v(89.05, -8.12) * mm});
            skLineSegment(sketch, "E912", {"start": v(89.05, -8.12) * mm, "end": v(88.88, -8.07) * mm});
            skLineSegment(sketch, "E913", {"start": v(88.88, -8.07) * mm, "end": v(88.7, -7.97) * mm});
            skLineSegment(sketch, "E914", {"start": v(88.7, -7.97) * mm, "end": v(88.53, -7.87) * mm});
            skLineSegment(sketch, "E915", {"start": v(88.53, -7.87) * mm, "end": v(88.38, -7.77) * mm});
            skLineSegment(sketch, "E916", {"start": v(88.38, -7.77) * mm, "end": v(88.24, -7.62) * mm});
            skLineSegment(sketch, "E917", {"start": v(88.24, -7.62) * mm, "end": v(88.11, -7.48) * mm});
            skLineSegment(sketch, "E918", {"start": v(88.11, -7.48) * mm, "end": v(87.99, -7.33) * mm});
            skLineSegment(sketch, "E919", {"start": v(87.99, -7.33) * mm, "end": v(87.89, -7.15) * mm});
            skLineSegment(sketch, "E920", {"start": v(87.89, -7.15) * mm, "end": v(87.81, -7) * mm});
            skLineSegment(sketch, "E921", {"start": v(87.81, -7) * mm, "end": v(87.76, -6.83) * mm});
            skLineSegment(sketch, "E922", {"start": v(87.76, -6.83) * mm, "end": v(87.71, -6.66) * mm});
            skLineSegment(sketch, "E923", {"start": v(-88.3, -19.83) * mm, "end": v(-88.42, -19.85) * mm});
            skLineSegment(sketch, "E924", {"start": v(-88.42, -19.85) * mm, "end": v(-88.52, -19.88) * mm});
            skLineSegment(sketch, "E925", {"start": v(-88.52, -19.88) * mm, "end": v(-88.62, -19.88) * mm});
            skLineSegment(sketch, "E926", {"start": v(-88.62, -19.88) * mm, "end": v(-88.72, -19.88) * mm});
            skLineSegment(sketch, "E927", {"start": v(-88.72, -19.88) * mm, "end": v(-88.8, -19.88) * mm});
            skLineSegment(sketch, "E928", {"start": v(-88.8, -19.88) * mm, "end": v(-88.9, -19.88) * mm});
            skLineSegment(sketch, "E929", {"start": v(-88.9, -19.88) * mm, "end": v(-88.97, -19.88) * mm});
            skLineSegment(sketch, "E930", {"start": v(-88.97, -19.88) * mm, "end": v(-89.04, -19.85) * mm});
            skLineSegment(sketch, "E931", {"start": v(-89.04, -19.85) * mm, "end": v(-89.12, -19.85) * mm});
            skLineSegment(sketch, "E932", {"start": v(-89.12, -19.85) * mm, "end": v(-89.2, -19.83) * mm});
            skLineSegment(sketch, "E933", {"start": v(-89.2, -19.83) * mm, "end": v(-89.27, -19.8) * mm});
            skLineSegment(sketch, "E934", {"start": v(-89.27, -19.8) * mm, "end": v(-89.37, -19.78) * mm});
            skLineSegment(sketch, "E935", {"start": v(-89.37, -19.78) * mm, "end": v(-97.13, -17.13) * mm});
            skLineSegment(sketch, "E936", {"start": v(-97.13, -17.13) * mm, "end": v(-97.63, -16.95) * mm});
            skLineSegment(sketch, "E937", {"start": v(-97.63, -16.95) * mm, "end": v(-98.07, -16.75) * mm});
            skLineSegment(sketch, "E938", {"start": v(-98.07, -16.75) * mm, "end": v(-98.52, -16.53) * mm});
            skLineSegment(sketch, "E939", {"start": v(-98.52, -16.53) * mm, "end": v(-98.92, -16.3) * mm});
            skLineSegment(sketch, "E940", {"start": v(-98.92, -16.3) * mm, "end": v(-99.31, -16.06) * mm});
            skLineSegment(sketch, "E941", {"start": v(-99.31, -16.06) * mm, "end": v(-99.69, -15.81) * mm});
            skLineSegment(sketch, "E942", {"start": v(-99.69, -15.81) * mm, "end": v(-100, -15.54) * mm});
            skLineSegment(sketch, "E943", {"start": v(-100, -15.54) * mm, "end": v(-100.33, -15.24) * mm});
            skLineSegment(sketch, "E944", {"start": v(-100.33, -15.24) * mm, "end": v(-100.83, -14.7) * mm});
            skLineSegment(sketch, "E945", {"start": v(-100.83, -14.7) * mm, "end": v(-101.27, -14.12) * mm});
            skLineSegment(sketch, "E946", {"start": v(-101.27, -14.12) * mm, "end": v(-101.62, -13.53) * mm});
            skLineSegment(sketch, "E947", {"start": v(-101.62, -13.53) * mm, "end": v(-101.94, -12.9) * mm});
            skLineSegment(sketch, "E948", {"start": v(-101.94, -12.9) * mm, "end": v(-102.17, -12.24) * mm});
            skLineSegment(sketch, "E949", {"start": v(-102.17, -12.24) * mm, "end": v(-102.34, -11.57) * mm});
            skLineSegment(sketch, "E950", {"start": v(-102.34, -11.57) * mm, "end": v(-102.44, -10.85) * mm});
            skLineSegment(sketch, "E951", {"start": v(-102.44, -10.85) * mm, "end": v(-102.46, -10.1) * mm});
            skLineSegment(sketch, "E952", {"start": v(-102.46, -10.1) * mm, "end": v(-102.46, 9.24) * mm});
            skLineSegment(sketch, "E953", {"start": v(-102.46, 9.24) * mm, "end": v(-102.44, 9.96) * mm});
            skLineSegment(sketch, "E954", {"start": v(-82.6, -10.38) * mm, "end": v(-82.64, -9.63) * mm});
            skLineSegment(sketch, "E955", {"start": v(-82.64, -9.63) * mm, "end": v(-82.64, 5.37) * mm});
            skLineSegment(sketch, "E956", {"start": v(-82.64, 5.37) * mm, "end": v(-82.62, 5.55) * mm});
            skLineSegment(sketch, "E957", {"start": v(-82.62, 5.55) * mm, "end": v(-82.6, 5.74) * mm});
            skLineSegment(sketch, "E958", {"start": v(-82.6, 5.74) * mm, "end": v(-82.55, 5.92) * mm});
            skLineSegment(sketch, "E959", {"start": v(-82.55, 5.92) * mm, "end": v(-82.5, 6.1) * mm});
            skLineSegment(sketch, "E960", {"start": v(-82.5, 6.1) * mm, "end": v(-82.42, 6.27) * mm});
            skLineSegment(sketch, "E961", {"start": v(-82.42, 6.27) * mm, "end": v(-82.32, 6.44) * mm});
            skLineSegment(sketch, "E962", {"start": v(-82.32, 6.44) * mm, "end": v(-82.2, 6.59) * mm});
            skLineSegment(sketch, "E963", {"start": v(-82.2, 6.59) * mm, "end": v(-82.07, 6.74) * mm});
            skLineSegment(sketch, "E964", {"start": v(-82.07, 6.74) * mm, "end": v(-81.92, 6.86) * mm});
            skLineSegment(sketch, "E965", {"start": v(-81.92, 6.86) * mm, "end": v(-81.78, 6.99) * mm});
            skLineSegment(sketch, "E966", {"start": v(-81.78, 6.99) * mm, "end": v(-81.6, 7.08) * mm});
            skLineSegment(sketch, "E967", {"start": v(-81.6, 7.08) * mm, "end": v(-81.43, 7.16) * mm});
            skLineSegment(sketch, "E968", {"start": v(-81.43, 7.16) * mm, "end": v(-81.26, 7.2) * mm});
            skLineSegment(sketch, "E969", {"start": v(-81.26, 7.2) * mm, "end": v(-81.08, 7.26) * mm});
            skLineSegment(sketch, "E970", {"start": v(-81.08, 7.26) * mm, "end": v(-80.88, 7.28) * mm});
            skLineSegment(sketch, "E971", {"start": v(-80.88, 7.28) * mm, "end": v(-80.7, 7.3) * mm});
            skLineSegment(sketch, "E972", {"start": v(-80.7, 7.3) * mm, "end": v(-80.51, 7.28) * mm});
            skLineSegment(sketch, "E973", {"start": v(-80.51, 7.28) * mm, "end": v(-80.31, 7.26) * mm});
            skLineSegment(sketch, "E974", {"start": v(-80.31, 7.26) * mm, "end": v(-80.14, 7.2) * mm});
            skLineSegment(sketch, "E975", {"start": v(-80.14, 7.2) * mm, "end": v(-79.97, 7.16) * mm});
            skLineSegment(sketch, "E976", {"start": v(-79.97, 7.16) * mm, "end": v(-79.8, 7.08) * mm});
            skLineSegment(sketch, "E977", {"start": v(-79.8, 7.08) * mm, "end": v(-79.62, 6.99) * mm});
            skLineSegment(sketch, "E978", {"start": v(-79.62, 6.99) * mm, "end": v(-79.47, 6.86) * mm});
            skLineSegment(sketch, "E979", {"start": v(-79.47, 6.86) * mm, "end": v(-79.32, 6.74) * mm});
            skLineSegment(sketch, "E980", {"start": v(-79.32, 6.74) * mm, "end": v(-79.2, 6.59) * mm});
            skLineSegment(sketch, "E981", {"start": v(-79.2, 6.59) * mm, "end": v(-79.07, 6.44) * mm});
            skLineSegment(sketch, "E982", {"start": v(-79.07, 6.44) * mm, "end": v(-78.97, 6.27) * mm});
            skLineSegment(sketch, "E983", {"start": v(-78.97, 6.27) * mm, "end": v(-78.9, 6.1) * mm});
            skLineSegment(sketch, "E984", {"start": v(-78.9, 6.1) * mm, "end": v(-78.85, 5.92) * mm});
            skLineSegment(sketch, "E985", {"start": v(-78.85, 5.92) * mm, "end": v(-78.8, 5.74) * mm});
            skLineSegment(sketch, "E986", {"start": v(-78.8, 5.74) * mm, "end": v(-78.77, 5.55) * mm});
            skLineSegment(sketch, "E987", {"start": v(-78.77, 5.55) * mm, "end": v(-78.77, 5.37) * mm});
            skLineSegment(sketch, "E988", {"start": v(-78.77, 5.37) * mm, "end": v(-78.77, -9.63) * mm});
            skLineSegment(sketch, "E989", {"start": v(-78.77, -9.63) * mm, "end": v(-78.75, -9.98) * mm});
            skLineSegment(sketch, "E990", {"start": v(-78.75, -9.98) * mm, "end": v(-78.7, -10.3) * mm});
            skLineSegment(sketch, "E991", {"start": v(-78.7, -10.3) * mm, "end": v(-78.63, -10.63) * mm});
            skLineSegment(sketch, "E992", {"start": v(-78.63, -10.63) * mm, "end": v(-78.53, -10.92) * mm});
            skLineSegment(sketch, "E993", {"start": v(-78.53, -10.92) * mm, "end": v(-78.38, -11.22) * mm});
            skLineSegment(sketch, "E994", {"start": v(-78.38, -11.22) * mm, "end": v(-78.2, -11.5) * mm});
            skLineSegment(sketch, "E995", {"start": v(-78.2, -11.5) * mm, "end": v(-78, -11.77) * mm});
            skLineSegment(sketch, "E996", {"start": v(-78, -11.77) * mm, "end": v(-77.78, -12.04) * mm});
            skLineSegment(sketch, "E997", {"start": v(-77.78, -12.04) * mm, "end": v(-77.5, -12.26) * mm});
            skLineSegment(sketch, "E998", {"start": v(-77.5, -12.26) * mm, "end": v(-77.24, -12.46) * mm});
            skLineSegment(sketch, "E999", {"start": v(-77.24, -12.46) * mm, "end": v(-76.96, -12.64) * mm});
            skLineSegment(sketch, "E1000", {"start": v(-76.96, -12.64) * mm, "end": v(-76.67, -12.78) * mm});
            skLineSegment(sketch, "E1001", {"start": v(-76.67, -12.78) * mm, "end": v(-76.37, -12.88) * mm});
            skLineSegment(sketch, "E1002", {"start": v(-76.37, -12.88) * mm, "end": v(-76.05, -12.96) * mm});
            skLineSegment(sketch, "E1003", {"start": v(-76.05, -12.96) * mm, "end": v(-75.72, -13) * mm});
            skLineSegment(sketch, "E1004", {"start": v(-75.72, -13) * mm, "end": v(-75.38, -13.03) * mm});
            skLineSegment(sketch, "E1005", {"start": v(-75.38, -13.03) * mm, "end": v(-71.98, -13.03) * mm});
            skLineSegment(sketch, "E1006", {"start": v(-71.98, -13.03) * mm, "end": v(-71.98, 5.37) * mm});
            skLineSegment(sketch, "E1007", {"start": v(-71.98, 5.37) * mm, "end": v(-71.98, 5.55) * mm});
            skLineSegment(sketch, "E1008", {"start": v(-71.98, 5.55) * mm, "end": v(-71.95, 5.74) * mm});
            skLineSegment(sketch, "E1009", {"start": v(-71.95, 5.74) * mm, "end": v(-71.9, 5.92) * mm});
            skLineSegment(sketch, "E1010", {"start": v(-71.9, 5.92) * mm, "end": v(-71.85, 6.1) * mm});
            skLineSegment(sketch, "E1011", {"start": v(-71.85, 6.1) * mm, "end": v(-71.78, 6.27) * mm});
            skLineSegment(sketch, "E1012", {"start": v(-71.78, 6.27) * mm, "end": v(-71.68, 6.44) * mm});
            skLineSegment(sketch, "E1013", {"start": v(-71.68, 6.44) * mm, "end": v(-71.56, 6.59) * mm});
            skLineSegment(sketch, "E1014", {"start": v(-71.56, 6.59) * mm, "end": v(-71.43, 6.74) * mm});
            skLineSegment(sketch, "E1015", {"start": v(-71.43, 6.74) * mm, "end": v(-71.28, 6.86) * mm});
            skLineSegment(sketch, "E1016", {"start": v(-71.28, 6.86) * mm, "end": v(-71.13, 6.99) * mm});
            skLineSegment(sketch, "E1017", {"start": v(-71.13, 6.99) * mm, "end": v(-70.96, 7.08) * mm});
            skLineSegment(sketch, "E1018", {"start": v(-70.96, 7.08) * mm, "end": v(-70.79, 7.16) * mm});
            skLineSegment(sketch, "E1019", {"start": v(-70.79, 7.16) * mm, "end": v(-70.61, 7.2) * mm});
            skLineSegment(sketch, "E1020", {"start": v(-70.61, 7.2) * mm, "end": v(-70.44, 7.26) * mm});
            skLineSegment(sketch, "E1021", {"start": v(-70.44, 7.26) * mm, "end": v(-70.24, 7.28) * mm});
            skLineSegment(sketch, "E1022", {"start": v(-70.24, 7.28) * mm, "end": v(-70.04, 7.3) * mm});
            skLineSegment(sketch, "E1023", {"start": v(-70.04, 7.3) * mm, "end": v(-69.87, 7.28) * mm});
            skLineSegment(sketch, "E1024", {"start": v(-69.87, 7.28) * mm, "end": v(-69.67, 7.26) * mm});
            skLineSegment(sketch, "E1025", {"start": v(-69.67, 7.26) * mm, "end": v(-69.5, 7.2) * mm});
            skLineSegment(sketch, "E1026", {"start": v(-69.5, 7.2) * mm, "end": v(-69.32, 7.16) * mm});
            skLineSegment(sketch, "E1027", {"start": v(-69.32, 7.16) * mm, "end": v(-69.15, 7.08) * mm});
            skLineSegment(sketch, "E1028", {"start": v(-69.15, 7.08) * mm, "end": v(-68.98, 6.99) * mm});
            skLineSegment(sketch, "E1029", {"start": v(-68.98, 6.99) * mm, "end": v(-68.83, 6.86) * mm});
            skLineSegment(sketch, "E1030", {"start": v(-68.83, 6.86) * mm, "end": v(-68.68, 6.74) * mm});
            skLineSegment(sketch, "E1031", {"start": v(-68.68, 6.74) * mm, "end": v(-68.56, 6.59) * mm});
            skLineSegment(sketch, "E1032", {"start": v(-68.56, 6.59) * mm, "end": v(-68.43, 6.44) * mm});
            skLineSegment(sketch, "E1033", {"start": v(-68.43, 6.44) * mm, "end": v(-68.33, 6.27) * mm});
            skLineSegment(sketch, "E1034", {"start": v(-68.33, 6.27) * mm, "end": v(-68.26, 6.1) * mm});
            skLineSegment(sketch, "E1035", {"start": v(-68.26, 6.1) * mm, "end": v(-68.2, 5.92) * mm});
            skLineSegment(sketch, "E1036", {"start": v(-68.2, 5.92) * mm, "end": v(-68.16, 5.74) * mm});
            skLineSegment(sketch, "E1037", {"start": v(-68.16, 5.74) * mm, "end": v(-68.13, 5.55) * mm});
            skLineSegment(sketch, "E1038", {"start": v(-68.13, 5.55) * mm, "end": v(-68.1, 5.37) * mm});
            skLineSegment(sketch, "E1039", {"start": v(-68.1, 5.37) * mm, "end": v(-68.1, -14.97) * mm});
            skLineSegment(sketch, "E1040", {"start": v(-68.1, -14.97) * mm, "end": v(-68.13, -15.14) * mm});
            skLineSegment(sketch, "E1041", {"start": v(-68.13, -15.14) * mm, "end": v(-68.16, -15.34) * mm});
            skLineSegment(sketch, "E1042", {"start": v(-68.16, -15.34) * mm, "end": v(-68.2, -15.51) * mm});
            skLineSegment(sketch, "E1043", {"start": v(-68.2, -15.51) * mm, "end": v(-68.26, -15.69) * mm});
            skLineSegment(sketch, "E1044", {"start": v(-68.26, -15.69) * mm, "end": v(-68.33, -15.86) * mm});
            skLineSegment(sketch, "E1045", {"start": v(-68.33, -15.86) * mm, "end": v(-68.43, -16.03) * mm});
            skLineSegment(sketch, "E1046", {"start": v(-68.43, -16.03) * mm, "end": v(-68.56, -16.18) * mm});
            skLineSegment(sketch, "E1047", {"start": v(-68.56, -16.18) * mm, "end": v(-68.68, -16.33) * mm});
            skLineSegment(sketch, "E1048", {"start": v(-68.68, -16.33) * mm, "end": v(-68.83, -16.46) * mm});
            skLineSegment(sketch, "E1049", {"start": v(-68.83, -16.46) * mm, "end": v(-68.98, -16.58) * mm});
            skLineSegment(sketch, "E1050", {"start": v(-68.98, -16.58) * mm, "end": v(-69.15, -16.68) * mm});
            skLineSegment(sketch, "E1051", {"start": v(-69.15, -16.68) * mm, "end": v(-69.32, -16.75) * mm});
            skLineSegment(sketch, "E1052", {"start": v(-69.32, -16.75) * mm, "end": v(-69.5, -16.8) * mm});
            skLineSegment(sketch, "E1053", {"start": v(-69.5, -16.8) * mm, "end": v(-69.67, -16.85) * mm});
            skLineSegment(sketch, "E1054", {"start": v(-69.67, -16.85) * mm, "end": v(-69.87, -16.88) * mm});
            skLineSegment(sketch, "E1055", {"start": v(-69.87, -16.88) * mm, "end": v(-70.04, -16.9) * mm});
            skLineSegment(sketch, "E1056", {"start": v(-70.04, -16.9) * mm, "end": v(-75.38, -16.9) * mm});
            skLineSegment(sketch, "E1057", {"start": v(-75.38, -16.9) * mm, "end": v(-76.12, -16.85) * mm});
            skLineSegment(sketch, "E1058", {"start": v(-76.12, -16.85) * mm, "end": v(-76.82, -16.75) * mm});
            skLineSegment(sketch, "E1059", {"start": v(-76.82, -16.75) * mm, "end": v(-77.5, -16.58) * mm});
            skLineSegment(sketch, "E1060", {"start": v(-77.5, -16.58) * mm, "end": v(-78.15, -16.36) * mm});
            skLineSegment(sketch, "E1061", {"start": v(-78.15, -16.36) * mm, "end": v(-78.77, -16.06) * mm});
            skLineSegment(sketch, "E1062", {"start": v(-78.77, -16.06) * mm, "end": v(-79.4, -15.69) * mm});
            skLineSegment(sketch, "E1063", {"start": v(-79.4, -15.69) * mm, "end": v(-79.97, -15.26) * mm});
            skLineSegment(sketch, "E1064", {"start": v(-79.97, -15.26) * mm, "end": v(-80.51, -14.77) * mm});
            skLineSegment(sketch, "E1065", {"start": v(-80.51, -14.77) * mm, "end": v(-81, -14.22) * mm});
            skLineSegment(sketch, "E1066", {"start": v(-81, -14.22) * mm, "end": v(-81.43, -13.65) * mm});
            skLineSegment(sketch, "E1067", {"start": v(-81.43, -13.65) * mm, "end": v(-81.8, -13.03) * mm});
            skLineSegment(sketch, "E1068", {"start": v(-81.8, -13.03) * mm, "end": v(-82.1, -12.41) * mm});
            skLineSegment(sketch, "E1069", {"start": v(-82.1, -12.41) * mm, "end": v(-82.32, -11.77) * mm});
            skLineSegment(sketch, "E1070", {"start": v(-82.32, -11.77) * mm, "end": v(-82.5, -11.07) * mm});
            skLineSegment(sketch, "E1071", {"start": v(-82.5, -11.07) * mm, "end": v(-82.6, -10.38) * mm});
            skLineSegment(sketch, "E1072", {"start": v(-62.28, -6.93) * mm, "end": v(-62.18, -6.24) * mm});
            skLineSegment(sketch, "E1073", {"start": v(-62.18, -6.24) * mm, "end": v(-62, -5.54) * mm});
            skLineSegment(sketch, "E1074", {"start": v(-62, -5.54) * mm, "end": v(-61.78, -4.9) * mm});
            skLineSegment(sketch, "E1075", {"start": v(-61.78, -4.9) * mm, "end": v(-61.46, -4.28) * mm});
            skLineSegment(sketch, "E1076", {"start": v(-61.46, -4.28) * mm, "end": v(-61.11, -3.66) * mm});
            skLineSegment(sketch, "E1077", {"start": v(-61.11, -3.66) * mm, "end": v(-60.67, -3.09) * mm});
            skLineSegment(sketch, "E1078", {"start": v(-60.67, -3.09) * mm, "end": v(-60.17, -2.54) * mm});
            skLineSegment(sketch, "E1079", {"start": v(-60.17, -2.54) * mm, "end": v(-59.7, -2.1) * mm});
            skLineSegment(sketch, "E1080", {"start": v(-59.7, -2.1) * mm, "end": v(-59.18, -1.72) * mm});
            skLineSegment(sketch, "E1081", {"start": v(-59.18, -1.72) * mm, "end": v(-58.66, -1.37) * mm});
            skLineSegment(sketch, "E1082", {"start": v(-58.66, -1.37) * mm, "end": v(-58.11, -1.08) * mm});
            skLineSegment(sketch, "E1083", {"start": v(-58.11, -1.08) * mm, "end": v(-57.54, -0.85) * mm});
            skLineSegment(sketch, "E1084", {"start": v(-57.54, -0.85) * mm, "end": v(-56.95, -0.65) * mm});
            skLineSegment(sketch, "E1085", {"start": v(-56.95, -0.65) * mm, "end": v(-56.33, -0.53) * mm});
            skLineSegment(sketch, "E1086", {"start": v(-56.33, -0.53) * mm, "end": v(-55.7, -0.43) * mm});
            skLineSegment(sketch, "E1087", {"start": v(-55.7, -0.43) * mm, "end": v(-55.46, -0.46) * mm});
            skLineSegment(sketch, "E1088", {"start": v(-55.46, -0.46) * mm, "end": v(-55.24, -0.48) * mm});
            skLineSegment(sketch, "E1089", {"start": v(-55.24, -0.48) * mm, "end": v(-55.04, -0.53) * mm});
            skLineSegment(sketch, "E1090", {"start": v(-55.04, -0.53) * mm, "end": v(-54.84, -0.58) * mm});
            skLineSegment(sketch, "E1091", {"start": v(-54.84, -0.58) * mm, "end": v(-54.64, -0.68) * mm});
            skLineSegment(sketch, "E1092", {"start": v(-54.64, -0.68) * mm, "end": v(-54.47, -0.78) * mm});
            skLineSegment(sketch, "E1093", {"start": v(-54.47, -0.78) * mm, "end": v(-54.32, -0.88) * mm});
            skLineSegment(sketch, "E1094", {"start": v(-54.32, -0.88) * mm, "end": v(-54.17, -1.03) * mm});
            skLineSegment(sketch, "E1095", {"start": v(-54.17, -1.03) * mm, "end": v(-54.04, -1.18) * mm});
            skLineSegment(sketch, "E1096", {"start": v(-54.04, -1.18) * mm, "end": v(-53.92, -1.32) * mm});
            skLineSegment(sketch, "E1097", {"start": v(-53.92, -1.32) * mm, "end": v(-53.82, -1.5) * mm});
            skLineSegment(sketch, "E1098", {"start": v(-53.82, -1.5) * mm, "end": v(-53.75, -1.65) * mm});
            skLineSegment(sketch, "E1099", {"start": v(-53.75, -1.65) * mm, "end": v(-53.67, -1.82) * mm});
            skLineSegment(sketch, "E1100", {"start": v(-53.67, -1.82) * mm, "end": v(-53.62, -2) * mm});
            skLineSegment(sketch, "E1101", {"start": v(-53.62, -2) * mm, "end": v(-53.6, -2.2) * mm});
            skLineSegment(sketch, "E1102", {"start": v(-53.6, -2.2) * mm, "end": v(-53.6, -2.37) * mm});
            skLineSegment(sketch, "E1103", {"start": v(-53.6, -2.37) * mm, "end": v(-53.6, -2.56) * mm});
            skLineSegment(sketch, "E1104", {"start": v(-53.6, -2.56) * mm, "end": v(-53.62, -2.76) * mm});
            skLineSegment(sketch, "E1105", {"start": v(-53.62, -2.76) * mm, "end": v(-53.67, -2.94) * mm});
            skLineSegment(sketch, "E1106", {"start": v(-53.67, -2.94) * mm, "end": v(-53.75, -3.11) * mm});
            skLineSegment(sketch, "E1107", {"start": v(-53.75, -3.11) * mm, "end": v(-53.82, -3.28) * mm});
            skLineSegment(sketch, "E1108", {"start": v(-53.82, -3.28) * mm, "end": v(-53.92, -3.43) * mm});
            skLineSegment(sketch, "E1109", {"start": v(-53.92, -3.43) * mm, "end": v(-54.02, -3.58) * mm});
            skLineSegment(sketch, "E1110", {"start": v(-54.02, -3.58) * mm, "end": v(-54.14, -3.73) * mm});
            skLineSegment(sketch, "E1111", {"start": v(-54.14, -3.73) * mm, "end": v(-54.3, -3.85) * mm});
            skLineSegment(sketch, "E1112", {"start": v(-54.3, -3.85) * mm, "end": v(-54.42, -3.95) * mm});
            skLineSegment(sketch, "E1113", {"start": v(-54.42, -3.95) * mm, "end": v(-54.57, -4.05) * mm});
            skLineSegment(sketch, "E1114", {"start": v(-54.57, -4.05) * mm, "end": v(-54.71, -4.13) * mm});
            skLineSegment(sketch, "E1115", {"start": v(-54.71, -4.13) * mm, "end": v(-54.86, -4.2) * mm});
            skLineSegment(sketch, "E1116", {"start": v(-54.86, -4.2) * mm, "end": v(-55.01, -4.25) * mm});
            skLineSegment(sketch, "E1117", {"start": v(-55.01, -4.25) * mm, "end": v(-55.16, -4.28) * mm});
            skLineSegment(sketch, "E1118", {"start": v(-55.16, -4.28) * mm, "end": v(-55.33, -4.3) * mm});
            skLineSegment(sketch, "E1119", {"start": v(-55.33, -4.3) * mm, "end": v(-55.63, -4.35) * mm});
            skLineSegment(sketch, "E1120", {"start": v(-55.63, -4.35) * mm, "end": v(-55.93, -4.4) * mm});
            skLineSegment(sketch, "E1121", {"start": v(-55.93, -4.4) * mm, "end": v(-56.2, -4.47) * mm});
            skLineSegment(sketch, "E1122", {"start": v(-56.2, -4.47) * mm, "end": v(-56.48, -4.6) * mm});
            skLineSegment(sketch, "E1123", {"start": v(-56.48, -4.6) * mm, "end": v(-56.72, -4.72) * mm});
            skLineSegment(sketch, "E1124", {"start": v(-56.72, -4.72) * mm, "end": v(-56.97, -4.9) * mm});
            skLineSegment(sketch, "E1125", {"start": v(-56.97, -4.9) * mm, "end": v(-57.22, -5.07) * mm});
            skLineSegment(sketch, "E1126", {"start": v(-57.22, -5.07) * mm, "end": v(-57.44, -5.3) * mm});
            skLineSegment(sketch, "E1127", {"start": v(-57.44, -5.3) * mm, "end": v(-57.67, -5.54) * mm});
            skLineSegment(sketch, "E1128", {"start": v(-57.67, -5.54) * mm, "end": v(-57.89, -5.81) * mm});
            skLineSegment(sketch, "E1129", {"start": v(-57.89, -5.81) * mm, "end": v(-58.04, -6.09) * mm});
            skLineSegment(sketch, "E1130", {"start": v(-58.04, -6.09) * mm, "end": v(-58.19, -6.38) * mm});
            skLineSegment(sketch, "E1131", {"start": v(-58.19, -6.38) * mm, "end": v(-58.29, -6.68) * mm});
            skLineSegment(sketch, "E1132", {"start": v(-58.29, -6.68) * mm, "end": v(-58.39, -7) * mm});
            skLineSegment(sketch, "E1133", {"start": v(-58.39, -7) * mm, "end": v(-58.41, -7.33) * mm});
            skLineSegment(sketch, "E1134", {"start": v(-58.41, -7.33) * mm, "end": v(-58.43, -7.67) * mm});
            skLineSegment(sketch, "E1135", {"start": v(-58.43, -7.67) * mm, "end": v(-58.43, -9.63) * mm});
            skLineSegment(sketch, "E1136", {"start": v(-58.43, -9.63) * mm, "end": v(-58.41, -9.98) * mm});
            skLineSegment(sketch, "E1137", {"start": v(-42.31, 6.1) * mm, "end": v(-42.24, 6.27) * mm});
            skLineSegment(sketch, "E1138", {"start": v(-42.24, 6.27) * mm, "end": v(-42.14, 6.44) * mm});
            skLineSegment(sketch, "E1139", {"start": v(-42.14, 6.44) * mm, "end": v(-42.01, 6.59) * mm});
            skLineSegment(sketch, "E1140", {"start": v(-42.01, 6.59) * mm, "end": v(-41.9, 6.74) * mm});
            skLineSegment(sketch, "E1141", {"start": v(-41.9, 6.74) * mm, "end": v(-41.74, 6.86) * mm});
            skLineSegment(sketch, "E1142", {"start": v(-41.74, 6.86) * mm, "end": v(-41.6, 6.99) * mm});
            skLineSegment(sketch, "E1143", {"start": v(-41.6, 6.99) * mm, "end": v(-41.44, 7.08) * mm});
            skLineSegment(sketch, "E1144", {"start": v(-41.44, 7.08) * mm, "end": v(-41.27, 7.16) * mm});
            skLineSegment(sketch, "E1145", {"start": v(-41.27, 7.16) * mm, "end": v(-41.1, 7.2) * mm});
            skLineSegment(sketch, "E1146", {"start": v(-41.1, 7.2) * mm, "end": v(-40.92, 7.26) * mm});
            skLineSegment(sketch, "E1147", {"start": v(-40.92, 7.26) * mm, "end": v(-40.72, 7.28) * mm});
            skLineSegment(sketch, "E1148", {"start": v(-40.72, 7.28) * mm, "end": v(-40.53, 7.3) * mm});
            skLineSegment(sketch, "E1149", {"start": v(-40.53, 7.3) * mm, "end": v(-35.22, 7.3) * mm});
            skLineSegment(sketch, "E1150", {"start": v(-35.22, 7.3) * mm, "end": v(-34.47, 7.26) * mm});
            skLineSegment(sketch, "E1151", {"start": v(-34.47, 7.26) * mm, "end": v(-33.75, 7.16) * mm});
            skLineSegment(sketch, "E1152", {"start": v(-33.75, 7.16) * mm, "end": v(-33.08, 6.99) * mm});
            skLineSegment(sketch, "E1153", {"start": v(-33.08, 6.99) * mm, "end": v(-32.41, 6.76) * mm});
            skLineSegment(sketch, "E1154", {"start": v(-32.41, 6.76) * mm, "end": v(-31.8, 6.46) * mm});
            skLineSegment(sketch, "E1155", {"start": v(-31.8, 6.46) * mm, "end": v(-31.2, 6.1) * mm});
            skLineSegment(sketch, "E1156", {"start": v(-31.2, 6.1) * mm, "end": v(-30.63, 5.67) * mm});
            skLineSegment(sketch, "E1157", {"start": v(-30.63, 5.67) * mm, "end": v(-30.08, 5.17) * mm});
            skLineSegment(sketch, "E1158", {"start": v(-30.08, 5.17) * mm, "end": v(-29.59, 4.63) * mm});
            skLineSegment(sketch, "E1159", {"start": v(-29.59, 4.63) * mm, "end": v(-29.14, 4.06) * mm});
            skLineSegment(sketch, "E1160", {"start": v(-29.14, 4.06) * mm, "end": v(-28.8, 3.44) * mm});
            skLineSegment(sketch, "E1161", {"start": v(-28.8, 3.44) * mm, "end": v(-28.47, 2.82) * mm});
            skLineSegment(sketch, "E1162", {"start": v(-28.47, 2.82) * mm, "end": v(-28.25, 2.17) * mm});
            skLineSegment(sketch, "E1163", {"start": v(-28.25, 2.17) * mm, "end": v(-28.07, 1.48) * mm});
            skLineSegment(sketch, "E1164", {"start": v(-28.07, 1.48) * mm, "end": v(-27.97, 0.78) * mm});
            skLineSegment(sketch, "E1165", {"start": v(-27.97, 0.78) * mm, "end": v(-27.95, 0.04) * mm});
            skLineSegment(sketch, "E1166", {"start": v(-27.95, 0.04) * mm, "end": v(-27.95, -14.97) * mm});
            skLineSegment(sketch, "E1167", {"start": v(-27.95, -14.97) * mm, "end": v(-27.95, -15.14) * mm});
            skLineSegment(sketch, "E1168", {"start": v(-27.95, -15.14) * mm, "end": v(-27.97, -15.34) * mm});
            skLineSegment(sketch, "E1169", {"start": v(-27.97, -15.34) * mm, "end": v(-28.02, -15.51) * mm});
            skLineSegment(sketch, "E1170", {"start": v(-28.02, -15.51) * mm, "end": v(-28.1, -15.69) * mm});
            skLineSegment(sketch, "E1171", {"start": v(-28.1, -15.69) * mm, "end": v(-28.17, -15.86) * mm});
            skLineSegment(sketch, "E1172", {"start": v(-28.17, -15.86) * mm, "end": v(-28.27, -16.03) * mm});
            skLineSegment(sketch, "E1173", {"start": v(-28.27, -16.03) * mm, "end": v(-28.4, -16.18) * mm});
            skLineSegment(sketch, "E1174", {"start": v(-28.4, -16.18) * mm, "end": v(-28.52, -16.33) * mm});
            skLineSegment(sketch, "E1175", {"start": v(-28.52, -16.33) * mm, "end": v(-28.67, -16.46) * mm});
            skLineSegment(sketch, "E1176", {"start": v(-28.67, -16.46) * mm, "end": v(-28.82, -16.58) * mm});
            skLineSegment(sketch, "E1177", {"start": v(-28.82, -16.58) * mm, "end": v(-28.97, -16.68) * mm});
            skLineSegment(sketch, "E1178", {"start": v(-28.97, -16.68) * mm, "end": v(-29.14, -16.75) * mm});
            skLineSegment(sketch, "E1179", {"start": v(-29.14, -16.75) * mm, "end": v(-29.31, -16.8) * mm});
            skLineSegment(sketch, "E1180", {"start": v(-29.31, -16.8) * mm, "end": v(-29.49, -16.85) * mm});
            skLineSegment(sketch, "E1181", {"start": v(-29.49, -16.85) * mm, "end": v(-29.69, -16.88) * mm});
            skLineSegment(sketch, "E1182", {"start": v(-29.69, -16.88) * mm, "end": v(-29.88, -16.9) * mm});
            skLineSegment(sketch, "E1183", {"start": v(-29.88, -16.9) * mm, "end": v(-30.08, -16.88) * mm});
            skLineSegment(sketch, "E1184", {"start": v(-30.08, -16.88) * mm, "end": v(-30.28, -16.85) * mm});
            skLineSegment(sketch, "E1185", {"start": v(-30.28, -16.85) * mm, "end": v(-30.46, -16.8) * mm});
            skLineSegment(sketch, "E1186", {"start": v(-30.46, -16.8) * mm, "end": v(-30.63, -16.75) * mm});
            skLineSegment(sketch, "E1187", {"start": v(-30.63, -16.75) * mm, "end": v(-30.8, -16.68) * mm});
            skLineSegment(sketch, "E1188", {"start": v(-30.8, -16.68) * mm, "end": v(-30.95, -16.58) * mm});
            skLineSegment(sketch, "E1189", {"start": v(-30.95, -16.58) * mm, "end": v(-31.1, -16.46) * mm});
            skLineSegment(sketch, "E1190", {"start": v(-31.1, -16.46) * mm, "end": v(-31.25, -16.33) * mm});
            skLineSegment(sketch, "E1191", {"start": v(-31.25, -16.33) * mm, "end": v(-31.37, -16.18) * mm});
            skLineSegment(sketch, "E1192", {"start": v(-31.37, -16.18) * mm, "end": v(-31.5, -16.03) * mm});
            skLineSegment(sketch, "E1193", {"start": v(-31.5, -16.03) * mm, "end": v(-31.6, -15.86) * mm});
            skLineSegment(sketch, "E1194", {"start": v(-31.6, -15.86) * mm, "end": v(-31.67, -15.69) * mm});
            skLineSegment(sketch, "E1195", {"start": v(-31.67, -15.69) * mm, "end": v(-31.75, -15.51) * mm});
            skLineSegment(sketch, "E1196", {"start": v(-31.75, -15.51) * mm, "end": v(-31.8, -15.34) * mm});
            skLineSegment(sketch, "E1197", {"start": v(-31.8, -15.34) * mm, "end": v(-31.82, -15.14) * mm});
            skLineSegment(sketch, "E1198", {"start": v(-31.82, -15.14) * mm, "end": v(-31.82, -14.97) * mm});
            skLineSegment(sketch, "E1199", {"start": v(-31.82, -14.97) * mm, "end": v(-31.82, 0.04) * mm});
            skLineSegment(sketch, "E1200", {"start": v(-31.82, 0.04) * mm, "end": v(-31.84, 0.39) * mm});
            skLineSegment(sketch, "E1201", {"start": v(-31.84, 0.39) * mm, "end": v(-31.87, 0.7) * mm});
            skLineSegment(sketch, "E1202", {"start": v(-31.87, 0.7) * mm, "end": v(-31.97, 1.03) * mm});
            skLineSegment(sketch, "E1203", {"start": v(-31.97, 1.03) * mm, "end": v(-32.07, 1.33) * mm});
            skLineSegment(sketch, "E1204", {"start": v(-32.07, 1.33) * mm, "end": v(-32.22, 1.63) * mm});
            skLineSegment(sketch, "E1205", {"start": v(-32.22, 1.63) * mm, "end": v(-32.37, 1.9) * mm});
            skLineSegment(sketch, "E1206", {"start": v(-32.37, 1.9) * mm, "end": v(-32.59, 2.17) * mm});
            skLineSegment(sketch, "E1207", {"start": v(-32.59, 2.17) * mm, "end": v(-32.81, 2.45) * mm});
            skLineSegment(sketch, "E1208", {"start": v(-32.81, 2.45) * mm, "end": v(-33.06, 2.67) * mm});
            skLineSegment(sketch, "E1209", {"start": v(-33.06, 2.67) * mm, "end": v(-33.33, 2.87) * mm});
            skLineSegment(sketch, "E1210", {"start": v(-33.33, 2.87) * mm, "end": v(-33.6, 3.04) * mm});
            skLineSegment(sketch, "E1211", {"start": v(-33.6, 3.04) * mm, "end": v(-33.9, 3.19) * mm});
            skLineSegment(sketch, "E1212", {"start": v(-33.9, 3.19) * mm, "end": v(-34.2, 3.29) * mm});
            skLineSegment(sketch, "E1213", {"start": v(-34.2, 3.29) * mm, "end": v(-34.52, 3.36) * mm});
            skLineSegment(sketch, "E1214", {"start": v(-34.52, 3.36) * mm, "end": v(-34.87, 3.41) * mm});
            skLineSegment(sketch, "E1215", {"start": v(-34.87, 3.41) * mm, "end": v(-35.22, 3.44) * mm});
            skLineSegment(sketch, "E1216", {"start": v(-35.22, 3.44) * mm, "end": v(-38.6, 3.44) * mm});
            skLineSegment(sketch, "E1217", {"start": v(-38.6, 3.44) * mm, "end": v(-38.6, -14.97) * mm});
            skLineSegment(sketch, "E1218", {"start": v(-38.6, -14.97) * mm, "end": v(-38.6, -15.14) * mm});
            skLineSegment(sketch, "E1219", {"start": v(-38.6, -15.14) * mm, "end": v(-38.62, -15.34) * mm});
            skLineSegment(sketch, "E1220", {"start": v(-38.62, -15.34) * mm, "end": v(-38.67, -15.51) * mm});
            skLineSegment(sketch, "E1221", {"start": v(-38.67, -15.51) * mm, "end": v(-38.74, -15.69) * mm});
            skLineSegment(sketch, "E1222", {"start": v(-38.74, -15.69) * mm, "end": v(-38.81, -15.86) * mm});
            skLineSegment(sketch, "E1223", {"start": v(-38.81, -15.86) * mm, "end": v(-38.91, -16.03) * mm});
            skLineSegment(sketch, "E1224", {"start": v(-38.91, -16.03) * mm, "end": v(-39.04, -16.18) * mm});
            skLineSegment(sketch, "E1225", {"start": v(-39.04, -16.18) * mm, "end": v(-39.16, -16.33) * mm});
            skLineSegment(sketch, "E1226", {"start": v(-39.16, -16.33) * mm, "end": v(-39.31, -16.46) * mm});
            skLineSegment(sketch, "E1227", {"start": v(-39.31, -16.46) * mm, "end": v(-39.46, -16.58) * mm});
            skLineSegment(sketch, "E1228", {"start": v(-39.46, -16.58) * mm, "end": v(-39.6, -16.68) * mm});
            skLineSegment(sketch, "E1229", {"start": v(-39.6, -16.68) * mm, "end": v(-39.78, -16.75) * mm});
            skLineSegment(sketch, "E1230", {"start": v(-39.78, -16.75) * mm, "end": v(-39.96, -16.8) * mm});
            skLineSegment(sketch, "E1231", {"start": v(-39.96, -16.8) * mm, "end": v(-40.13, -16.85) * mm});
            skLineSegment(sketch, "E1232", {"start": v(-40.13, -16.85) * mm, "end": v(-40.33, -16.88) * mm});
            skLineSegment(sketch, "E1233", {"start": v(-40.33, -16.88) * mm, "end": v(-40.53, -16.9) * mm});
            skLineSegment(sketch, "E1234", {"start": v(-40.53, -16.9) * mm, "end": v(-40.72, -16.88) * mm});
            skLineSegment(sketch, "E1235", {"start": v(-40.72, -16.88) * mm, "end": v(-40.92, -16.85) * mm});
            skLineSegment(sketch, "E1236", {"start": v(-40.92, -16.85) * mm, "end": v(-41.1, -16.8) * mm});
            skLineSegment(sketch, "E1237", {"start": v(-41.1, -16.8) * mm, "end": v(-41.27, -16.75) * mm});
            skLineSegment(sketch, "E1238", {"start": v(-41.27, -16.75) * mm, "end": v(-41.44, -16.68) * mm});
            skLineSegment(sketch, "E1239", {"start": v(-41.44, -16.68) * mm, "end": v(-41.6, -16.58) * mm});
            skLineSegment(sketch, "E1240", {"start": v(-41.6, -16.58) * mm, "end": v(-41.74, -16.46) * mm});
            skLineSegment(sketch, "E1241", {"start": v(-41.74, -16.46) * mm, "end": v(-41.9, -16.33) * mm});
            skLineSegment(sketch, "E1242", {"start": v(-41.9, -16.33) * mm, "end": v(-42.01, -16.18) * mm});
            skLineSegment(sketch, "E1243", {"start": v(-42.01, -16.18) * mm, "end": v(-42.14, -16.03) * mm});
            skLineSegment(sketch, "E1244", {"start": v(-42.14, -16.03) * mm, "end": v(-42.24, -15.86) * mm});
            skLineSegment(sketch, "E1245", {"start": v(-42.24, -15.86) * mm, "end": v(-42.31, -15.69) * mm});
            skLineSegment(sketch, "E1246", {"start": v(-42.31, -15.69) * mm, "end": v(-42.39, -15.51) * mm});
            skLineSegment(sketch, "E1247", {"start": v(-42.39, -15.51) * mm, "end": v(-42.44, -15.34) * mm});
            skLineSegment(sketch, "E1248", {"start": v(-23.09, 4.98) * mm, "end": v(-23.11, 5.17) * mm});
            skLineSegment(sketch, "E1249", {"start": v(-23.11, 5.17) * mm, "end": v(-23.11, 5.37) * mm});
            skLineSegment(sketch, "E1250", {"start": v(-23.11, 5.37) * mm, "end": v(-23.11, 5.55) * mm});
            skLineSegment(sketch, "E1251", {"start": v(-23.11, 5.55) * mm, "end": v(-23.09, 5.74) * mm});
            skLineSegment(sketch, "E1252", {"start": v(-23.09, 5.74) * mm, "end": v(-23.04, 5.92) * mm});
            skLineSegment(sketch, "E1253", {"start": v(-23.04, 5.92) * mm, "end": v(-22.99, 6.1) * mm});
            skLineSegment(sketch, "E1254", {"start": v(-22.99, 6.1) * mm, "end": v(-22.89, 6.27) * mm});
            skLineSegment(sketch, "E1255", {"start": v(-22.89, 6.27) * mm, "end": v(-22.8, 6.44) * mm});
            skLineSegment(sketch, "E1256", {"start": v(-22.8, 6.44) * mm, "end": v(-22.7, 6.59) * mm});
            skLineSegment(sketch, "E1257", {"start": v(-22.7, 6.59) * mm, "end": v(-22.54, 6.74) * mm});
            skLineSegment(sketch, "E1258", {"start": v(-22.54, 6.74) * mm, "end": v(-22.44, 6.84) * mm});
            skLineSegment(sketch, "E1259", {"start": v(-22.44, 6.84) * mm, "end": v(-22.34, 6.91) * mm});
            skLineSegment(sketch, "E1260", {"start": v(-22.34, 6.91) * mm, "end": v(-22.24, 6.99) * mm});
            skLineSegment(sketch, "E1261", {"start": v(-22.24, 6.99) * mm, "end": v(-22.12, 7.06) * mm});
            skLineSegment(sketch, "E1262", {"start": v(-22.12, 7.06) * mm, "end": v(-22.02, 7.1) * mm});
            skLineSegment(sketch, "E1263", {"start": v(-22.02, 7.1) * mm, "end": v(-21.9, 7.16) * mm});
            skLineSegment(sketch, "E1264", {"start": v(-21.9, 7.16) * mm, "end": v(-21.77, 7.2) * mm});
            skLineSegment(sketch, "E1265", {"start": v(-21.77, 7.2) * mm, "end": v(-21.65, 7.26) * mm});
            skLineSegment(sketch, "E1266", {"start": v(-21.65, 7.26) * mm, "end": v(-21.65, 11.15) * mm});
            skLineSegment(sketch, "E1267", {"start": v(-21.65, 11.15) * mm, "end": v(-21.65, 11.33) * mm});
            skLineSegment(sketch, "E1268", {"start": v(-21.65, 11.33) * mm, "end": v(-21.62, 11.52) * mm});
            skLineSegment(sketch, "E1269", {"start": v(-21.62, 11.52) * mm, "end": v(-21.58, 11.7) * mm});
            skLineSegment(sketch, "E1270", {"start": v(-21.58, 11.7) * mm, "end": v(-21.5, 11.87) * mm});
            skLineSegment(sketch, "E1271", {"start": v(-21.5, 11.87) * mm, "end": v(-21.43, 12.05) * mm});
            skLineSegment(sketch, "E1272", {"start": v(-21.43, 12.05) * mm, "end": v(-21.33, 12.22) * mm});
            skLineSegment(sketch, "E1273", {"start": v(-21.33, 12.22) * mm, "end": v(-21.2, 12.37) * mm});
            skLineSegment(sketch, "E1274", {"start": v(-21.2, 12.37) * mm, "end": v(-21.08, 12.52) * mm});
            skLineSegment(sketch, "E1275", {"start": v(-21.08, 12.52) * mm, "end": v(-20.93, 12.64) * mm});
            skLineSegment(sketch, "E1276", {"start": v(-20.93, 12.64) * mm, "end": v(-20.76, 12.76) * mm});
            skLineSegment(sketch, "E1277", {"start": v(-20.76, 12.76) * mm, "end": v(-20.6, 12.86) * mm});
            skLineSegment(sketch, "E1278", {"start": v(-20.6, 12.86) * mm, "end": v(-20.43, 12.94) * mm});
            skLineSegment(sketch, "E1279", {"start": v(-20.43, 12.94) * mm, "end": v(-20.26, 12.99) * mm});
            skLineSegment(sketch, "E1280", {"start": v(-20.26, 12.99) * mm, "end": v(-20.09, 13.04) * mm});
            skLineSegment(sketch, "E1281", {"start": v(-20.09, 13.04) * mm, "end": v(-19.91, 13.06) * mm});
            skLineSegment(sketch, "E1282", {"start": v(-19.91, 13.06) * mm, "end": v(-19.71, 13.09) * mm});
            skLineSegment(sketch, "E1283", {"start": v(-19.71, 13.09) * mm, "end": v(-19.52, 13.06) * mm});
            skLineSegment(sketch, "E1284", {"start": v(-19.52, 13.06) * mm, "end": v(-19.32, 13.04) * mm});
            skLineSegment(sketch, "E1285", {"start": v(-19.32, 13.04) * mm, "end": v(-19.14, 12.99) * mm});
            skLineSegment(sketch, "E1286", {"start": v(-19.14, 12.99) * mm, "end": v(-18.97, 12.94) * mm});
            skLineSegment(sketch, "E1287", {"start": v(-18.97, 12.94) * mm, "end": v(-18.8, 12.86) * mm});
            skLineSegment(sketch, "E1288", {"start": v(-18.8, 12.86) * mm, "end": v(-18.65, 12.76) * mm});
            skLineSegment(sketch, "E1289", {"start": v(-18.65, 12.76) * mm, "end": v(-18.5, 12.64) * mm});
            skLineSegment(sketch, "E1290", {"start": v(-18.5, 12.64) * mm, "end": v(-18.35, 12.52) * mm});
            skLineSegment(sketch, "E1291", {"start": v(-18.35, 12.52) * mm, "end": v(-18.23, 12.37) * mm});
            skLineSegment(sketch, "E1292", {"start": v(-18.23, 12.37) * mm, "end": v(-18.1, 12.22) * mm});
            skLineSegment(sketch, "E1293", {"start": v(-18.1, 12.22) * mm, "end": v(-18, 12.05) * mm});
            skLineSegment(sketch, "E1294", {"start": v(-18, 12.05) * mm, "end": v(-17.93, 11.87) * mm});
            skLineSegment(sketch, "E1295", {"start": v(-17.93, 11.87) * mm, "end": v(-17.85, 11.7) * mm});
            skLineSegment(sketch, "E1296", {"start": v(-17.85, 11.7) * mm, "end": v(-17.8, 11.52) * mm});
            skLineSegment(sketch, "E1297", {"start": v(-17.8, 11.52) * mm, "end": v(-17.78, 11.33) * mm});
            skLineSegment(sketch, "E1298", {"start": v(-17.78, 11.33) * mm, "end": v(-17.78, 11.15) * mm});
            skLineSegment(sketch, "E1299", {"start": v(-17.78, 11.15) * mm, "end": v(-17.78, 7.3) * mm});
            skLineSegment(sketch, "E1300", {"start": v(-17.78, 7.3) * mm, "end": v(-15.35, 7.3) * mm});
            skLineSegment(sketch, "E1301", {"start": v(-15.35, 7.3) * mm, "end": v(-15.18, 7.28) * mm});
            skLineSegment(sketch, "E1302", {"start": v(-15.18, 7.28) * mm, "end": v(-14.98, 7.26) * mm});
            skLineSegment(sketch, "E1303", {"start": v(-14.98, 7.26) * mm, "end": v(-14.8, 7.2) * mm});
            skLineSegment(sketch, "E1304", {"start": v(-14.8, 7.2) * mm, "end": v(-14.63, 7.16) * mm});
            skLineSegment(sketch, "E1305", {"start": v(-14.63, 7.16) * mm, "end": v(-14.46, 7.08) * mm});
            skLineSegment(sketch, "E1306", {"start": v(-14.46, 7.08) * mm, "end": v(-14.28, 6.99) * mm});
            skLineSegment(sketch, "E1307", {"start": v(-14.28, 6.99) * mm, "end": v(-14.13, 6.86) * mm});
            skLineSegment(sketch, "E1308", {"start": v(-14.13, 6.86) * mm, "end": v(-13.98, 6.74) * mm});
            skLineSegment(sketch, "E1309", {"start": v(-13.98, 6.74) * mm, "end": v(-13.86, 6.59) * mm});
            skLineSegment(sketch, "E1310", {"start": v(-13.86, 6.59) * mm, "end": v(-13.74, 6.44) * mm});
            skLineSegment(sketch, "E1311", {"start": v(-13.74, 6.44) * mm, "end": v(-13.64, 6.27) * mm});
            skLineSegment(sketch, "E1312", {"start": v(-13.64, 6.27) * mm, "end": v(-13.56, 6.1) * mm});
            skLineSegment(sketch, "E1313", {"start": v(-13.56, 6.1) * mm, "end": v(-13.51, 5.92) * mm});
            skLineSegment(sketch, "E1314", {"start": v(-13.51, 5.92) * mm, "end": v(-13.46, 5.74) * mm});
            skLineSegment(sketch, "E1315", {"start": v(-13.46, 5.74) * mm, "end": v(-13.44, 5.55) * mm});
            skLineSegment(sketch, "E1316", {"start": v(-13.44, 5.55) * mm, "end": v(-13.41, 5.37) * mm});
            skLineSegment(sketch, "E1317", {"start": v(-13.41, 5.37) * mm, "end": v(-13.44, 5.17) * mm});
            skLineSegment(sketch, "E1318", {"start": v(-13.44, 5.17) * mm, "end": v(-13.46, 4.98) * mm});
            skLineSegment(sketch, "E1319", {"start": v(-13.46, 4.98) * mm, "end": v(-13.51, 4.8) * mm});
            skLineSegment(sketch, "E1320", {"start": v(-13.51, 4.8) * mm, "end": v(-13.56, 4.63) * mm});
            skLineSegment(sketch, "E1321", {"start": v(-13.56, 4.63) * mm, "end": v(-13.64, 4.45) * mm});
            skLineSegment(sketch, "E1322", {"start": v(-13.64, 4.45) * mm, "end": v(-13.74, 4.28) * mm});
            skLineSegment(sketch, "E1323", {"start": v(-13.74, 4.28) * mm, "end": v(-13.86, 4.13) * mm});
            skLineSegment(sketch, "E1324", {"start": v(-13.86, 4.13) * mm, "end": v(-13.98, 3.98) * mm});
            skLineSegment(sketch, "E1325", {"start": v(-13.98, 3.98) * mm, "end": v(-14.13, 3.86) * mm});
            skLineSegment(sketch, "E1326", {"start": v(-14.13, 3.86) * mm, "end": v(-14.28, 3.74) * mm});
            skLineSegment(sketch, "E1327", {"start": v(-14.28, 3.74) * mm, "end": v(-14.46, 3.64) * mm});
            skLineSegment(sketch, "E1328", {"start": v(-14.46, 3.64) * mm, "end": v(-14.63, 3.56) * mm});
            skLineSegment(sketch, "E1329", {"start": v(-14.63, 3.56) * mm, "end": v(-14.8, 3.51) * mm});
            skLineSegment(sketch, "E1330", {"start": v(-14.8, 3.51) * mm, "end": v(-14.98, 3.46) * mm});
            skLineSegment(sketch, "E1331", {"start": v(-14.98, 3.46) * mm, "end": v(-15.18, 3.44) * mm});
            skLineSegment(sketch, "E1332", {"start": v(-15.18, 3.44) * mm, "end": v(-15.35, 3.44) * mm});
            skLineSegment(sketch, "E1333", {"start": v(-15.35, 3.44) * mm, "end": v(-17.78, 3.44) * mm});
            skLineSegment(sketch, "E1334", {"start": v(-17.78, 3.44) * mm, "end": v(-17.78, -10.6) * mm});
            skLineSegment(sketch, "E1335", {"start": v(-17.78, -10.6) * mm, "end": v(-17.78, -10.85) * mm});
            skLineSegment(sketch, "E1336", {"start": v(-17.78, -10.85) * mm, "end": v(-17.73, -11.1) * mm});
            skLineSegment(sketch, "E1337", {"start": v(-17.73, -11.1) * mm, "end": v(-17.68, -11.32) * mm});
            skLineSegment(sketch, "E1338", {"start": v(-17.68, -11.32) * mm, "end": v(-17.6, -11.54) * mm});
            skLineSegment(sketch, "E1339", {"start": v(-17.6, -11.54) * mm, "end": v(-17.5, -11.74) * mm});
            skLineSegment(sketch, "E1340", {"start": v(-17.5, -11.74) * mm, "end": v(-17.38, -11.94) * mm});
            skLineSegment(sketch, "E1341", {"start": v(-17.38, -11.94) * mm, "end": v(-17.23, -12.14) * mm});
            skLineSegment(sketch, "E1342", {"start": v(-17.23, -12.14) * mm, "end": v(-17.09, -12.31) * mm});
            skLineSegment(sketch, "E1343", {"start": v(-17.09, -12.31) * mm, "end": v(-16.89, -12.49) * mm});
            skLineSegment(sketch, "E1344", {"start": v(-16.89, -12.49) * mm, "end": v(-16.71, -12.64) * mm});
            skLineSegment(sketch, "E1345", {"start": v(-16.71, -12.64) * mm, "end": v(-16.51, -12.73) * mm});
            skLineSegment(sketch, "E1346", {"start": v(-16.51, -12.73) * mm, "end": v(-16.3, -12.83) * mm});
            skLineSegment(sketch, "E1347", {"start": v(-16.3, -12.83) * mm, "end": v(-16.07, -12.93) * mm});
            skLineSegment(sketch, "E1348", {"start": v(-16.07, -12.93) * mm, "end": v(-15.85, -12.98) * mm});
            skLineSegment(sketch, "E1349", {"start": v(-15.85, -12.98) * mm, "end": v(-15.62, -13) * mm});
            skLineSegment(sketch, "E1350", {"start": v(-15.62, -13) * mm, "end": v(-15.35, -13.03) * mm});
            skLineSegment(sketch, "E1351", {"start": v(-15.35, -13.03) * mm, "end": v(-15.15, -13.03) * mm});
            skLineSegment(sketch, "E1352", {"start": v(-15.15, -13.03) * mm, "end": v(-14.98, -13.06) * mm});
            skLineSegment(sketch, "E1353", {"start": v(-14.98, -13.06) * mm, "end": v(-14.78, -13.1) * mm});
            skLineSegment(sketch, "E1354", {"start": v(-14.78, -13.1) * mm, "end": v(-14.6, -13.16) * mm});
            skLineSegment(sketch, "E1355", {"start": v(-14.6, -13.16) * mm, "end": v(-14.43, -13.26) * mm});
            skLineSegment(sketch, "E1356", {"start": v(-14.43, -13.26) * mm, "end": v(-14.28, -13.35) * mm});
            skLineSegment(sketch, "E1357", {"start": v(-14.28, -13.35) * mm, "end": v(-14.1, -13.45) * mm});
            skLineSegment(sketch, "E1358", {"start": v(-14.1, -13.45) * mm, "end": v(-13.96, -13.6) * mm});
            skLineSegment(sketch, "E1359", {"start": v(-13.96, -13.6) * mm, "end": v(-13.84, -13.75) * mm});
            skLineSegment(sketch, "E1360", {"start": v(-13.84, -13.75) * mm, "end": v(-13.71, -13.9) * mm});
            skLineSegment(sketch, "E1361", {"start": v(-13.71, -13.9) * mm, "end": v(-13.61, -14.07) * mm});
            skLineSegment(sketch, "E1362", {"start": v(-13.61, -14.07) * mm, "end": v(-13.54, -14.22) * mm});
            skLineSegment(sketch, "E1363", {"start": v(-13.54, -14.22) * mm, "end": v(-13.49, -14.4) * mm});
            skLineSegment(sketch, "E1364", {"start": v(-13.49, -14.4) * mm, "end": v(-13.44, -14.57) * mm});
            skLineSegment(sketch, "E1365", {"start": v(-13.44, -14.57) * mm, "end": v(-13.41, -14.77) * mm});
            skLineSegment(sketch, "E1366", {"start": v(-13.41, -14.77) * mm, "end": v(-13.41, -14.97) * mm});
            skLineSegment(sketch, "E1367", {"start": v(-13.41, -14.97) * mm, "end": v(-13.41, -15.14) * mm});
            skLineSegment(sketch, "E1368", {"start": v(-13.41, -15.14) * mm, "end": v(-13.44, -15.34) * mm});
            skLineSegment(sketch, "E1369", {"start": v(-13.44, -15.34) * mm, "end": v(-13.49, -15.51) * mm});
            skLineSegment(sketch, "E1370", {"start": v(-13.49, -15.51) * mm, "end": v(-13.54, -15.69) * mm});
            skLineSegment(sketch, "E1371", {"start": v(-13.54, -15.69) * mm, "end": v(-13.61, -15.86) * mm});
            skLineSegment(sketch, "E1372", {"start": v(-13.61, -15.86) * mm, "end": v(-13.71, -16.03) * mm});
            skLineSegment(sketch, "E1373", {"start": v(-13.71, -16.03) * mm, "end": v(-13.84, -16.18) * mm});
            skLineSegment(sketch, "E1374", {"start": v(-13.84, -16.18) * mm, "end": v(-13.96, -16.33) * mm});
            skLineSegment(sketch, "E1375", {"start": v(-13.96, -16.33) * mm, "end": v(-14.1, -16.46) * mm});
            skLineSegment(sketch, "E1376", {"start": v(-14.1, -16.46) * mm, "end": v(-14.28, -16.58) * mm});
            skLineSegment(sketch, "E1377", {"start": v(-14.28, -16.58) * mm, "end": v(-14.43, -16.68) * mm});
            skLineSegment(sketch, "E1378", {"start": v(-14.43, -16.68) * mm, "end": v(-14.6, -16.75) * mm});
            skLineSegment(sketch, "E1379", {"start": v(-14.6, -16.75) * mm, "end": v(-14.78, -16.8) * mm});
            skLineSegment(sketch, "E1380", {"start": v(-14.78, -16.8) * mm, "end": v(-14.98, -16.85) * mm});
            skLineSegment(sketch, "E1381", {"start": v(-14.98, -16.85) * mm, "end": v(-15.15, -16.88) * mm});
            skLineSegment(sketch, "E1382", {"start": v(-15.15, -16.88) * mm, "end": v(-15.35, -16.9) * mm});
            skLineSegment(sketch, "E1383", {"start": v(-15.35, -16.9) * mm, "end": v(-16, -16.85) * mm});
            skLineSegment(sketch, "E1384", {"start": v(-16, -16.85) * mm, "end": v(-16.61, -16.78) * mm});
            skLineSegment(sketch, "E1385", {"start": v(-16.61, -16.78) * mm, "end": v(-17.2, -16.63) * mm});
            skLineSegment(sketch, "E1386", {"start": v(-17.2, -16.63) * mm, "end": v(-17.76, -16.43) * mm});
            skLineSegment(sketch, "E1387", {"start": v(-17.76, -16.43) * mm, "end": v(-18.3, -16.16) * mm});
            skLineSegment(sketch, "E1388", {"start": v(-18.3, -16.16) * mm, "end": v(-18.82, -15.86) * mm});
            skLineSegment(sketch, "E1389", {"start": v(-18.82, -15.86) * mm, "end": v(-19.32, -15.46) * mm});
            skLineSegment(sketch, "E1390", {"start": v(-19.32, -15.46) * mm, "end": v(-19.79, -15.04) * mm});
            skLineSegment(sketch, "E1391", {"start": v(-19.79, -15.04) * mm, "end": v(-20.24, -14.57) * mm});
            skLineSegment(sketch, "E1392", {"start": v(-20.24, -14.57) * mm, "end": v(-20.6, -14.07) * mm});
            skLineSegment(sketch, "E1393", {"start": v(-20.6, -14.07) * mm, "end": v(-20.93, -13.55) * mm});
            skLineSegment(sketch, "E1394", {"start": v(-20.93, -13.55) * mm, "end": v(-21.18, -13) * mm});
            skLineSegment(sketch, "E1395", {"start": v(-21.18, -13) * mm, "end": v(-21.4, -12.44) * mm});
            skLineSegment(sketch, "E1396", {"start": v(-21.4, -12.44) * mm, "end": v(-21.53, -11.84) * mm});
            skLineSegment(sketch, "E1397", {"start": v(-21.53, -11.84) * mm, "end": v(-21.62, -11.25) * mm});
            skLineSegment(sketch, "E1398", {"start": v(-21.62, -11.25) * mm, "end": v(-21.65, -10.6) * mm});
            skLineSegment(sketch, "E1399", {"start": v(-21.65, -10.6) * mm, "end": v(-21.65, 3.46) * mm});
            skLineSegment(sketch, "E1400", {"start": v(-21.65, 3.46) * mm, "end": v(-21.77, 3.51) * mm});
            skLineSegment(sketch, "E1401", {"start": v(-21.77, 3.51) * mm, "end": v(-21.9, 3.56) * mm});
            skLineSegment(sketch, "E1402", {"start": v(-21.9, 3.56) * mm, "end": v(-22.02, 3.61) * mm});
            skLineSegment(sketch, "E1403", {"start": v(-22.02, 3.61) * mm, "end": v(-22.12, 3.66) * mm});
            skLineSegment(sketch, "E1404", {"start": v(-22.12, 3.66) * mm, "end": v(-22.24, 3.74) * mm});
            skLineSegment(sketch, "E1405", {"start": v(-22.24, 3.74) * mm, "end": v(-22.34, 3.81) * mm});
            skLineSegment(sketch, "E1406", {"start": v(-22.34, 3.81) * mm, "end": v(-22.44, 3.9) * mm});
            skLineSegment(sketch, "E1407", {"start": v(-127, 457.2) * mm, "end": v(127, 457.2) * mm});
            skLineSegment(sketch, "E1408", {"start": v(-127, -457.2) * mm, "end": v(127, -457.2) * mm});
            skLineSegment(sketch, "E1409", {"start": v(-127, 457.2) * mm, "end": v(-127, -457.2) * mm});
            skLineSegment(sketch, "E1410", {"start": v(127, 457.2) * mm, "end": v(127, -457.2) * mm});
            skLineSegment(sketch, "E1411", {"start": v(-86.78, 431.8) * mm, "end": v(86.78, 431.8) * mm});
            skLineSegment(sketch, "E1412", {"start": v(-86.78, 146.05) * mm, "end": v(86.78, 146.05) * mm});
            skLineSegment(sketch, "E1413", {"start": v(-86.78, 431.8) * mm, "end": v(-86.78, 368.76) * mm});
            skLineSegment(sketch, "E1414", {"start": v(86.78, 431.8) * mm, "end": v(86.78, 368.76) * mm});
            skLineSegment(sketch, "E1415", {"start": v(-86.78, -146.05) * mm, "end": v(86.78, -146.05) * mm});
            skLineSegment(sketch, "E1416", {"start": v(-86.78, -431.8) * mm, "end": v(86.78, -431.8) * mm});
            skLineSegment(sketch, "E1417", {"start": v(-86.78, -146.05) * mm, "end": v(-86.78, -209.09) * mm});
            skLineSegment(sketch, "E1418", {"start": v(86.78, -146.05) * mm, "end": v(86.78, -209.09) * mm});
            skCircle(sketch, "E1419", {"center": v(-120.65, 450.85) * mm, "radius": 1.58 * mm});
            skCircle(sketch, "E1420", {"center": v(-120.65, -450.85) * mm, "radius": 1.58 * mm});
            skCircle(sketch, "E1421", {"center": v(120.65, -450.85) * mm, "radius": 1.58 * mm});
            skCircle(sketch, "E1422", {"center": v(120.65, 450.85) * mm, "radius": 1.58 * mm});
            skCircle(sketch, "E1423", {"center": v(0, 450.85) * mm, "radius": 1.58 * mm});
            skCircle(sketch, "E1424", {"center": v(0, -450.85) * mm, "radius": 1.58 * mm});
            skCircle(sketch, "E1425", {"center": v(-120.65, 0) * mm, "radius": 1.58 * mm});
            skCircle(sketch, "E1426", {"center": v(120.65, 0) * mm, "radius": 1.58 * mm});
            skCircle(sketch, "E1427", {"center": v(-120.65, 300.57) * mm, "radius": 1.58 * mm});
            skCircle(sketch, "E1428", {"center": v(-120.65, 150.28) * mm, "radius": 1.58 * mm});
            skCircle(sketch, "E1429", {"center": v(120.65, 300.57) * mm, "radius": 1.58 * mm});
            skCircle(sketch, "E1430", {"center": v(120.65, 150.28) * mm, "radius": 1.58 * mm});
            skCircle(sketch, "E1431", {"center": v(-120.65, -150.28) * mm, "radius": 1.58 * mm});
            skCircle(sketch, "E1432", {"center": v(120.65, -150.28) * mm, "radius": 1.58 * mm});
            skCircle(sketch, "E1433", {"center": v(120.65, -300.57) * mm, "radius": 1.58 * mm});
            skCircle(sketch, "E1434", {"center": v(-120.65, -300.57) * mm, "radius": 1.58 * mm});
            skArc(sketch, "E1435", {"start": v(-86.78, 368.76) * mm, "mid": v(-109, 360.36) * mm, "end": v(-86.78, 351.96) * mm});
            skArc(sketch, "E1436", {"start": v(86.78, 351.96) * mm, "mid": v(109, 360.36) * mm, "end": v(86.78, 368.76) * mm});
            skArc(sketch, "E1437", {"start": v(-86.78, 209.09) * mm, "mid": v(-109, 217.49) * mm, "end": v(-86.78, 225.89) * mm});
            skArc(sketch, "E1438", {"start": v(86.78, 225.89) * mm, "mid": v(109, 217.49) * mm, "end": v(86.78, 209.09) * mm});
            skLineSegment(sketch, "E1439", {"start": v(86.78, 351.96) * mm, "end": v(86.78, 225.89) * mm});
            skLineSegment(sketch, "E1440", {"start": v(-86.78, 351.96) * mm, "end": v(-86.78, 225.89) * mm});
            skLineSegment(sketch, "E1441", {"start": v(-86.78, 209.09) * mm, "end": v(-86.78, 146.05) * mm});
            skLineSegment(sketch, "E1442", {"start": v(86.78, 209.09) * mm, "end": v(86.78, 146.05) * mm});
            skArc(sketch, "E1443", {"start": v(-86.78, -209.09) * mm, "mid": v(-109, -217.49) * mm, "end": v(-86.78, -225.89) * mm});
            skArc(sketch, "E1444", {"start": v(-86.78, -368.76) * mm, "mid": v(-109, -360.36) * mm, "end": v(-86.78, -351.96) * mm});
            skArc(sketch, "E1445", {"start": v(86.78, -351.96) * mm, "mid": v(109, -360.36) * mm, "end": v(86.78, -368.76) * mm});
            skArc(sketch, "E1446", {"start": v(86.78, -225.89) * mm, "mid": v(109, -217.49) * mm, "end": v(86.78, -209.09) * mm});
            skLineSegment(sketch, "E1447", {"start": v(86.78, -225.89) * mm, "end": v(86.78, -351.96) * mm});
            skLineSegment(sketch, "E1448", {"start": v(86.78, -368.76) * mm, "end": v(86.78, -431.8) * mm});
            skLineSegment(sketch, "E1449", {"start": v(-86.78, -368.76) * mm, "end": v(-86.78, -431.8) * mm});
            skLineSegment(sketch, "E1450", {"start": v(-86.78, -225.89) * mm, "end": v(-86.78, -351.96) * mm});
            skLineSegment(sketch, "E1451", {"start": v(-102.44, 9.96) * mm, "end": v(-102.34, 10.68) * mm});
            skLineSegment(sketch, "E1452", {"start": v(-102.34, 10.68) * mm, "end": v(-102.17, 11.35) * mm});
            skLineSegment(sketch, "E1453", {"start": v(-102.17, 11.35) * mm, "end": v(-101.94, 12.02) * mm});
            skLineSegment(sketch, "E1454", {"start": v(-101.94, 12.02) * mm, "end": v(-101.62, 12.64) * mm});
            skLineSegment(sketch, "E1455", {"start": v(-101.62, 12.64) * mm, "end": v(-101.27, 13.24) * mm});
            skLineSegment(sketch, "E1456", {"start": v(-101.27, 13.24) * mm, "end": v(-100.83, 13.8) * mm});
            skLineSegment(sketch, "E1457", {"start": v(-100.83, 13.8) * mm, "end": v(-100.33, 14.35) * mm});
            skLineSegment(sketch, "E1458", {"start": v(-100.33, 14.35) * mm, "end": v(-99.78, 14.85) * mm});
            skLineSegment(sketch, "E1459", {"start": v(-99.78, 14.85) * mm, "end": v(-99.21, 15.3) * mm});
            skLineSegment(sketch, "E1460", {"start": v(-99.21, 15.3) * mm, "end": v(-98.62, 15.64) * mm});
            skLineSegment(sketch, "E1461", {"start": v(-98.62, 15.64) * mm, "end": v(-98, 15.96) * mm});
            skLineSegment(sketch, "E1462", {"start": v(-98, 15.96) * mm, "end": v(-97.33, 16.19) * mm});
            skLineSegment(sketch, "E1463", {"start": v(-97.33, 16.19) * mm, "end": v(-96.66, 16.36) * mm});
            skLineSegment(sketch, "E1464", {"start": v(-96.66, 16.36) * mm, "end": v(-95.94, 16.46) * mm});
            skLineSegment(sketch, "E1465", {"start": v(-95.94, 16.46) * mm, "end": v(-95.2, 16.49) * mm});
            skLineSegment(sketch, "E1466", {"start": v(-95.2, 16.49) * mm, "end": v(-94.48, 16.46) * mm});
            skLineSegment(sketch, "E1467", {"start": v(-94.48, 16.46) * mm, "end": v(-93.76, 16.36) * mm});
            skLineSegment(sketch, "E1468", {"start": v(-93.76, 16.36) * mm, "end": v(-93.09, 16.19) * mm});
            skLineSegment(sketch, "E1469", {"start": v(-93.09, 16.19) * mm, "end": v(-92.42, 15.96) * mm});
            skLineSegment(sketch, "E1470", {"start": v(-92.42, 15.96) * mm, "end": v(-91.8, 15.64) * mm});
            skLineSegment(sketch, "E1471", {"start": v(-91.8, 15.64) * mm, "end": v(-91.2, 15.3) * mm});
            skLineSegment(sketch, "E1472", {"start": v(-91.2, 15.3) * mm, "end": v(-90.63, 14.85) * mm});
            skLineSegment(sketch, "E1473", {"start": v(-90.63, 14.85) * mm, "end": v(-90.09, 14.35) * mm});
            skLineSegment(sketch, "E1474", {"start": v(-90.09, 14.35) * mm, "end": v(-89.59, 13.8) * mm});
            skLineSegment(sketch, "E1475", {"start": v(-89.59, 13.8) * mm, "end": v(-89.14, 13.24) * mm});
            skLineSegment(sketch, "E1476", {"start": v(-89.14, 13.24) * mm, "end": v(-88.8, 12.64) * mm});
            skLineSegment(sketch, "E1477", {"start": v(-88.8, 12.64) * mm, "end": v(-88.47, 12.02) * mm});
            skLineSegment(sketch, "E1478", {"start": v(-88.47, 12.02) * mm, "end": v(-88.25, 11.35) * mm});
            skLineSegment(sketch, "E1479", {"start": v(-88.25, 11.35) * mm, "end": v(-88.08, 10.68) * mm});
            skLineSegment(sketch, "E1480", {"start": v(-88.08, 10.68) * mm, "end": v(-87.98, 9.96) * mm});
            skLineSegment(sketch, "E1481", {"start": v(-87.98, 9.96) * mm, "end": v(-87.95, 9.24) * mm});
            skLineSegment(sketch, "E1482", {"start": v(-87.95, 9.24) * mm, "end": v(-87.95, -10.1) * mm});
            skLineSegment(sketch, "E1483", {"start": v(-87.95, -10.1) * mm, "end": v(-87.95, -10.33) * mm});
            skLineSegment(sketch, "E1484", {"start": v(-87.95, -10.33) * mm, "end": v(-87.95, -10.55) * mm});
            skLineSegment(sketch, "E1485", {"start": v(-87.95, -10.55) * mm, "end": v(-87.98, -10.78) * mm});
            skLineSegment(sketch, "E1486", {"start": v(-87.98, -10.78) * mm, "end": v(-88, -11) * mm});
            skLineSegment(sketch, "E1487", {"start": v(-88, -11) * mm, "end": v(-88.03, -11.2) * mm});
            skLineSegment(sketch, "E1488", {"start": v(-88.03, -11.2) * mm, "end": v(-88.05, -11.42) * mm});
            skLineSegment(sketch, "E1489", {"start": v(-88.05, -11.42) * mm, "end": v(-88.08, -11.62) * mm});
            skLineSegment(sketch, "E1490", {"start": v(-88.08, -11.62) * mm, "end": v(-88.13, -11.84) * mm});
            skLineSegment(sketch, "E1491", {"start": v(-88.13, -11.84) * mm, "end": v(-88.15, -11.97) * mm});
            skLineSegment(sketch, "E1492", {"start": v(-88.15, -11.97) * mm, "end": v(-88.2, -12.11) * mm});
            skLineSegment(sketch, "E1493", {"start": v(-88.2, -12.11) * mm, "end": v(-88.25, -12.24) * mm});
            skLineSegment(sketch, "E1494", {"start": v(-88.25, -12.24) * mm, "end": v(-88.3, -12.36) * mm});
            skLineSegment(sketch, "E1495", {"start": v(-88.3, -12.36) * mm, "end": v(-88.37, -12.46) * mm});
            skLineSegment(sketch, "E1496", {"start": v(-88.37, -12.46) * mm, "end": v(-88.45, -12.59) * mm});
            skLineSegment(sketch, "E1497", {"start": v(-88.45, -12.59) * mm, "end": v(-88.55, -12.69) * mm});
            skLineSegment(sketch, "E1498", {"start": v(-88.55, -12.69) * mm, "end": v(-88.65, -12.8) * mm});
            skLineSegment(sketch, "E1499", {"start": v(-88.65, -12.8) * mm, "end": v(-88.8, -12.93) * mm});
            skLineSegment(sketch, "E1500", {"start": v(-88.8, -12.93) * mm, "end": v(-88.97, -13.06) * mm});
            skLineSegment(sketch, "E1501", {"start": v(-88.97, -13.06) * mm, "end": v(-89.12, -13.16) * mm});
            skLineSegment(sketch, "E1502", {"start": v(-89.12, -13.16) * mm, "end": v(-89.3, -13.23) * mm});
            skLineSegment(sketch, "E1503", {"start": v(-89.3, -13.23) * mm, "end": v(-89.47, -13.3) * mm});
            skLineSegment(sketch, "E1504", {"start": v(-89.47, -13.3) * mm, "end": v(-89.64, -13.35) * mm});
            skLineSegment(sketch, "E1505", {"start": v(-89.64, -13.35) * mm, "end": v(-89.84, -13.38) * mm});
            skLineSegment(sketch, "E1506", {"start": v(-89.84, -13.38) * mm, "end": v(-90.04, -13.38) * mm});
            skLineSegment(sketch, "E1507", {"start": v(-90.04, -13.38) * mm, "end": v(-90.23, -13.38) * mm});
            skLineSegment(sketch, "E1508", {"start": v(-90.23, -13.38) * mm, "end": v(-90.4, -13.35) * mm});
            skLineSegment(sketch, "E1509", {"start": v(-90.4, -13.35) * mm, "end": v(-90.6, -13.3) * mm});
            skLineSegment(sketch, "E1510", {"start": v(-90.6, -13.3) * mm, "end": v(-90.78, -13.23) * mm});
            skLineSegment(sketch, "E1511", {"start": v(-90.78, -13.23) * mm, "end": v(-90.93, -13.16) * mm});
            skLineSegment(sketch, "E1512", {"start": v(-90.93, -13.16) * mm, "end": v(-91.1, -13.06) * mm});
            skLineSegment(sketch, "E1513", {"start": v(-91.1, -13.06) * mm, "end": v(-91.25, -12.96) * mm});
            skLineSegment(sketch, "E1514", {"start": v(-91.25, -12.96) * mm, "end": v(-91.4, -12.8) * mm});
            skLineSegment(sketch, "E1515", {"start": v(-91.4, -12.8) * mm, "end": v(-91.52, -12.66) * mm});
            skLineSegment(sketch, "E1516", {"start": v(-91.52, -12.66) * mm, "end": v(-91.65, -12.51) * mm});
            skLineSegment(sketch, "E1517", {"start": v(-91.65, -12.51) * mm, "end": v(-91.75, -12.36) * mm});
            skLineSegment(sketch, "E1518", {"start": v(-91.75, -12.36) * mm, "end": v(-91.82, -12.19) * mm});
            skLineSegment(sketch, "E1519", {"start": v(-91.82, -12.19) * mm, "end": v(-91.9, -12.02) * mm});
            skLineSegment(sketch, "E1520", {"start": v(-91.9, -12.02) * mm, "end": v(-91.92, -11.84) * mm});
            skLineSegment(sketch, "E1521", {"start": v(-91.92, -11.84) * mm, "end": v(-91.95, -11.64) * mm});
            skLineSegment(sketch, "E1522", {"start": v(-91.95, -11.64) * mm, "end": v(-91.97, -11.44) * mm});
            skLineSegment(sketch, "E1523", {"start": v(-91.97, -11.44) * mm, "end": v(-91.97, -11.4) * mm});
            skLineSegment(sketch, "E1524", {"start": v(-91.97, -11.4) * mm, "end": v(-91.97, -11.35) * mm});
            skLineSegment(sketch, "E1525", {"start": v(-91.97, -11.35) * mm, "end": v(-91.97, -11.3) * mm});
            skLineSegment(sketch, "E1526", {"start": v(-91.97, -11.3) * mm, "end": v(-91.97, -11.25) * mm});
            skLineSegment(sketch, "E1527", {"start": v(-91.97, -11.25) * mm, "end": v(-91.95, -11.2) * mm});
            skLineSegment(sketch, "E1528", {"start": v(-91.95, -11.2) * mm, "end": v(-91.95, -11.12) * mm});
            skLineSegment(sketch, "E1529", {"start": v(-91.95, -11.12) * mm, "end": v(-91.95, -11.07) * mm});
            skLineSegment(sketch, "E1530", {"start": v(-91.95, -11.07) * mm, "end": v(-91.95, -11.02) * mm});
            skLineSegment(sketch, "E1531", {"start": v(-91.95, -11.02) * mm, "end": v(-91.92, -10.9) * mm});
            skLineSegment(sketch, "E1532", {"start": v(-91.92, -10.9) * mm, "end": v(-91.9, -10.8) * mm});
            skLineSegment(sketch, "E1533", {"start": v(-91.9, -10.8) * mm, "end": v(-91.87, -10.68) * mm});
            skLineSegment(sketch, "E1534", {"start": v(-91.87, -10.68) * mm, "end": v(-91.85, -10.58) * mm});
            skLineSegment(sketch, "E1535", {"start": v(-91.85, -10.58) * mm, "end": v(-91.85, -10.45) * mm});
            skLineSegment(sketch, "E1536", {"start": v(-91.85, -10.45) * mm, "end": v(-91.82, -10.35) * mm});
            skLineSegment(sketch, "E1537", {"start": v(-91.82, -10.35) * mm, "end": v(-91.82, -10.23) * mm});
            skLineSegment(sketch, "E1538", {"start": v(-91.82, -10.23) * mm, "end": v(-91.82, -10.1) * mm});
            skLineSegment(sketch, "E1539", {"start": v(-91.82, -10.1) * mm, "end": v(-91.82, 9.24) * mm});
            skLineSegment(sketch, "E1540", {"start": v(-91.82, 9.24) * mm, "end": v(-91.85, 9.56) * mm});
            skLineSegment(sketch, "E1541", {"start": v(-91.85, 9.56) * mm, "end": v(-91.87, 9.91) * mm});
            skLineSegment(sketch, "E1542", {"start": v(-91.87, 9.91) * mm, "end": v(-91.97, 10.23) * mm});
            skLineSegment(sketch, "E1543", {"start": v(-91.97, 10.23) * mm, "end": v(-92.07, 10.53) * mm});
            skLineSegment(sketch, "E1544", {"start": v(-92.07, 10.53) * mm, "end": v(-92.22, 10.83) * mm});
            skLineSegment(sketch, "E1545", {"start": v(-92.22, 10.83) * mm, "end": v(-92.37, 11.1) * mm});
            skLineSegment(sketch, "E1546", {"start": v(-92.37, 11.1) * mm, "end": v(-92.6, 11.38) * mm});
            skLineSegment(sketch, "E1547", {"start": v(-92.6, 11.38) * mm, "end": v(-92.81, 11.62) * mm});
            skLineSegment(sketch, "E1548", {"start": v(-92.81, 11.62) * mm, "end": v(-93.06, 11.85) * mm});
            skLineSegment(sketch, "E1549", {"start": v(-93.06, 11.85) * mm, "end": v(-93.34, 12.07) * mm});
            skLineSegment(sketch, "E1550", {"start": v(-93.34, 12.07) * mm, "end": v(-93.6, 12.22) * mm});
            skLineSegment(sketch, "E1551", {"start": v(-93.6, 12.22) * mm, "end": v(-93.9, 12.37) * mm});
            skLineSegment(sketch, "E1552", {"start": v(-93.9, 12.37) * mm, "end": v(-94.2, 12.47) * mm});
            skLineSegment(sketch, "E1553", {"start": v(-94.2, 12.47) * mm, "end": v(-94.53, 12.57) * mm});
            skLineSegment(sketch, "E1554", {"start": v(-94.53, 12.57) * mm, "end": v(-94.87, 12.6) * mm});
            skLineSegment(sketch, "E1555", {"start": v(-94.87, 12.6) * mm, "end": v(-95.2, 12.62) * mm});
            skLineSegment(sketch, "E1556", {"start": v(-95.2, 12.62) * mm, "end": v(-95.54, 12.6) * mm});
            skLineSegment(sketch, "E1557", {"start": v(-95.54, 12.6) * mm, "end": v(-95.89, 12.57) * mm});
            skLineSegment(sketch, "E1558", {"start": v(-95.89, 12.57) * mm, "end": v(-96.21, 12.47) * mm});
            skLineSegment(sketch, "E1559", {"start": v(-96.21, 12.47) * mm, "end": v(-96.51, 12.37) * mm});
            skLineSegment(sketch, "E1560", {"start": v(-96.51, 12.37) * mm, "end": v(-96.8, 12.22) * mm});
            skLineSegment(sketch, "E1561", {"start": v(-96.8, 12.22) * mm, "end": v(-97.08, 12.07) * mm});
            skLineSegment(sketch, "E1562", {"start": v(-97.08, 12.07) * mm, "end": v(-97.35, 11.85) * mm});
            skLineSegment(sketch, "E1563", {"start": v(-97.35, 11.85) * mm, "end": v(-97.6, 11.62) * mm});
            skLineSegment(sketch, "E1564", {"start": v(-97.6, 11.62) * mm, "end": v(-97.82, 11.38) * mm});
            skLineSegment(sketch, "E1565", {"start": v(-97.82, 11.38) * mm, "end": v(-98.05, 11.1) * mm});
            skLineSegment(sketch, "E1566", {"start": v(-98.05, 11.1) * mm, "end": v(-98.2, 10.83) * mm});
            skLineSegment(sketch, "E1567", {"start": v(-98.2, 10.83) * mm, "end": v(-98.35, 10.53) * mm});
            skLineSegment(sketch, "E1568", {"start": v(-98.35, 10.53) * mm, "end": v(-98.44, 10.23) * mm});
            skLineSegment(sketch, "E1569", {"start": v(-98.44, 10.23) * mm, "end": v(-98.54, 9.91) * mm});
            skLineSegment(sketch, "E1570", {"start": v(-98.54, 9.91) * mm, "end": v(-98.57, 9.56) * mm});
            skLineSegment(sketch, "E1571", {"start": v(-98.57, 9.56) * mm, "end": v(-98.6, 9.24) * mm});
            skLineSegment(sketch, "E1572", {"start": v(-98.6, 9.24) * mm, "end": v(-98.6, -10.1) * mm});
            skLineSegment(sketch, "E1573", {"start": v(-98.6, -10.1) * mm, "end": v(-98.57, -10.45) * mm});
            skLineSegment(sketch, "E1574", {"start": v(-98.57, -10.45) * mm, "end": v(-98.54, -10.78) * mm});
            skLineSegment(sketch, "E1575", {"start": v(-98.54, -10.78) * mm, "end": v(-98.47, -11.07) * mm});
            skLineSegment(sketch, "E1576", {"start": v(-98.47, -11.07) * mm, "end": v(-98.37, -11.37) * mm});
            skLineSegment(sketch, "E1577", {"start": v(-98.37, -11.37) * mm, "end": v(-98.22, -11.64) * mm});
            skLineSegment(sketch, "E1578", {"start": v(-98.22, -11.64) * mm, "end": v(-98.07, -11.9) * mm});
            skLineSegment(sketch, "E1579", {"start": v(-98.07, -11.9) * mm, "end": v(-97.87, -12.14) * mm});
            skLineSegment(sketch, "E1580", {"start": v(-97.87, -12.14) * mm, "end": v(-97.65, -12.36) * mm});
            skLineSegment(sketch, "E1581", {"start": v(-97.65, -12.36) * mm, "end": v(-97.43, -12.56) * mm});
            skLineSegment(sketch, "E1582", {"start": v(-97.43, -12.56) * mm, "end": v(-97.18, -12.76) * mm});
            skLineSegment(sketch, "E1583", {"start": v(-97.18, -12.76) * mm, "end": v(-96.93, -12.93) * mm});
            skLineSegment(sketch, "E1584", {"start": v(-96.93, -12.93) * mm, "end": v(-96.66, -13.08) * mm});
            skLineSegment(sketch, "E1585", {"start": v(-96.66, -13.08) * mm, "end": v(-96.41, -13.2) * mm});
            skLineSegment(sketch, "E1586", {"start": v(-96.41, -13.2) * mm, "end": v(-96.11, -13.33) * mm});
            skLineSegment(sketch, "E1587", {"start": v(-96.11, -13.33) * mm, "end": v(-95.84, -13.43) * mm});
            skLineSegment(sketch, "E1588", {"start": v(-95.84, -13.43) * mm, "end": v(-95.54, -13.53) * mm});
            skLineSegment(sketch, "E1589", {"start": v(-95.54, -13.53) * mm, "end": v(-88.13, -16.1) * mm});
            skLineSegment(sketch, "E1590", {"start": v(-88.13, -16.1) * mm, "end": v(-87.93, -16.18) * mm});
            skLineSegment(sketch, "E1591", {"start": v(-87.93, -16.18) * mm, "end": v(-87.75, -16.28) * mm});
            skLineSegment(sketch, "E1592", {"start": v(-87.75, -16.28) * mm, "end": v(-87.6, -16.38) * mm});
            skLineSegment(sketch, "E1593", {"start": v(-87.6, -16.38) * mm, "end": v(-87.46, -16.5) * mm});
            skLineSegment(sketch, "E1594", {"start": v(-87.46, -16.5) * mm, "end": v(-87.3, -16.63) * mm});
            skLineSegment(sketch, "E1595", {"start": v(-87.3, -16.63) * mm, "end": v(-87.18, -16.78) * mm});
            skLineSegment(sketch, "E1596", {"start": v(-87.18, -16.78) * mm, "end": v(-87.08, -16.93) * mm});
            skLineSegment(sketch, "E1597", {"start": v(-87.08, -16.93) * mm, "end": v(-86.99, -17.1) * mm});
            skLineSegment(sketch, "E1598", {"start": v(-86.99, -17.1) * mm, "end": v(-86.94, -17.22) * mm});
            skLineSegment(sketch, "E1599", {"start": v(-86.94, -17.22) * mm, "end": v(-86.91, -17.32) * mm});
            skLineSegment(sketch, "E1600", {"start": v(-86.91, -17.32) * mm, "end": v(-86.86, -17.42) * mm});
            skLineSegment(sketch, "E1601", {"start": v(-86.86, -17.42) * mm, "end": v(-86.84, -17.55) * mm});
            skLineSegment(sketch, "E1602", {"start": v(-86.84, -17.55) * mm, "end": v(-86.81, -17.65) * mm});
            skLineSegment(sketch, "E1603", {"start": v(-86.81, -17.65) * mm, "end": v(-86.81, -17.75) * mm});
            skLineSegment(sketch, "E1604", {"start": v(-86.81, -17.75) * mm, "end": v(-86.79, -17.84) * mm});
            skLineSegment(sketch, "E1605", {"start": v(-86.79, -17.84) * mm, "end": v(-86.79, -17.94) * mm});
            skLineSegment(sketch, "E1606", {"start": v(-86.79, -17.94) * mm, "end": v(-86.79, -18.02) * mm});
            skLineSegment(sketch, "E1607", {"start": v(-86.79, -18.02) * mm, "end": v(-86.79, -18.1) * mm});
            skLineSegment(sketch, "E1608", {"start": v(-86.79, -18.1) * mm, "end": v(-86.81, -18.17) * mm});
            skLineSegment(sketch, "E1609", {"start": v(-86.81, -18.17) * mm, "end": v(-86.81, -18.24) * mm});
            skLineSegment(sketch, "E1610", {"start": v(-86.81, -18.24) * mm, "end": v(-86.84, -18.32) * mm});
            skLineSegment(sketch, "E1611", {"start": v(-86.84, -18.32) * mm, "end": v(-86.84, -18.4) * mm});
            skLineSegment(sketch, "E1612", {"start": v(-86.84, -18.4) * mm, "end": v(-86.86, -18.49) * mm});
            skLineSegment(sketch, "E1613", {"start": v(-86.86, -18.49) * mm, "end": v(-86.89, -18.56) * mm});
            skLineSegment(sketch, "E1614", {"start": v(-86.89, -18.56) * mm, "end": v(-86.96, -18.74) * mm});
            skLineSegment(sketch, "E1615", {"start": v(-86.96, -18.74) * mm, "end": v(-87.06, -18.91) * mm});
            skLineSegment(sketch, "E1616", {"start": v(-87.06, -18.91) * mm, "end": v(-87.16, -19.08) * mm});
            skLineSegment(sketch, "E1617", {"start": v(-87.16, -19.08) * mm, "end": v(-87.26, -19.23) * mm});
            skLineSegment(sketch, "E1618", {"start": v(-87.26, -19.23) * mm, "end": v(-87.4, -19.36) * mm});
            skLineSegment(sketch, "E1619", {"start": v(-87.4, -19.36) * mm, "end": v(-87.56, -19.48) * mm});
            skLineSegment(sketch, "E1620", {"start": v(-87.56, -19.48) * mm, "end": v(-87.7, -19.6) * mm});
            skLineSegment(sketch, "E1621", {"start": v(-87.7, -19.6) * mm, "end": v(-87.88, -19.7) * mm});
            skLineSegment(sketch, "E1622", {"start": v(-87.88, -19.7) * mm, "end": v(-87.98, -19.73) * mm});
            skLineSegment(sketch, "E1623", {"start": v(-87.98, -19.73) * mm, "end": v(-88.1, -19.78) * mm});
            skLineSegment(sketch, "E1624", {"start": v(-88.1, -19.78) * mm, "end": v(-88.2, -19.8) * mm});
            skLineSegment(sketch, "E1625", {"start": v(-88.2, -19.8) * mm, "end": v(-88.3, -19.83) * mm});
            skLineSegment(sketch, "E1626", {"start": v(-58.41, -9.98) * mm, "end": v(-58.39, -10.3) * mm});
            skLineSegment(sketch, "E1627", {"start": v(-58.39, -10.3) * mm, "end": v(-58.29, -10.63) * mm});
            skLineSegment(sketch, "E1628", {"start": v(-58.29, -10.63) * mm, "end": v(-58.19, -10.92) * mm});
            skLineSegment(sketch, "E1629", {"start": v(-58.19, -10.92) * mm, "end": v(-58.04, -11.22) * mm});
            skLineSegment(sketch, "E1630", {"start": v(-58.04, -11.22) * mm, "end": v(-57.89, -11.5) * mm});
            skLineSegment(sketch, "E1631", {"start": v(-57.89, -11.5) * mm, "end": v(-57.67, -11.77) * mm});
            skLineSegment(sketch, "E1632", {"start": v(-57.67, -11.77) * mm, "end": v(-57.44, -12.04) * mm});
            skLineSegment(sketch, "E1633", {"start": v(-57.44, -12.04) * mm, "end": v(-57.2, -12.26) * mm});
            skLineSegment(sketch, "E1634", {"start": v(-57.2, -12.26) * mm, "end": v(-56.92, -12.46) * mm});
            skLineSegment(sketch, "E1635", {"start": v(-56.92, -12.46) * mm, "end": v(-56.65, -12.64) * mm});
            skLineSegment(sketch, "E1636", {"start": v(-56.65, -12.64) * mm, "end": v(-56.35, -12.78) * mm});
            skLineSegment(sketch, "E1637", {"start": v(-56.35, -12.78) * mm, "end": v(-56.05, -12.88) * mm});
            skLineSegment(sketch, "E1638", {"start": v(-56.05, -12.88) * mm, "end": v(-55.73, -12.96) * mm});
            skLineSegment(sketch, "E1639", {"start": v(-55.73, -12.96) * mm, "end": v(-55.38, -13) * mm});
            skLineSegment(sketch, "E1640", {"start": v(-55.38, -13) * mm, "end": v(-55.04, -13.03) * mm});
            skLineSegment(sketch, "E1641", {"start": v(-55.04, -13.03) * mm, "end": v(-51.66, -13.03) * mm});
            skLineSegment(sketch, "E1642", {"start": v(-51.66, -13.03) * mm, "end": v(-51.66, 0.51) * mm});
            skLineSegment(sketch, "E1643", {"start": v(-51.66, 0.51) * mm, "end": v(-51.69, 0.83) * mm});
            skLineSegment(sketch, "E1644", {"start": v(-51.69, 0.83) * mm, "end": v(-51.74, 1.18) * mm});
            skLineSegment(sketch, "E1645", {"start": v(-51.74, 1.18) * mm, "end": v(-51.81, 1.5) * mm});
            skLineSegment(sketch, "E1646", {"start": v(-51.81, 1.5) * mm, "end": v(-51.94, 1.8) * mm});
            skLineSegment(sketch, "E1647", {"start": v(-51.94, 1.8) * mm, "end": v(-52.06, 2.1) * mm});
            skLineSegment(sketch, "E1648", {"start": v(-52.06, 2.1) * mm, "end": v(-52.23, 2.37) * mm});
            skLineSegment(sketch, "E1649", {"start": v(-52.23, 2.37) * mm, "end": v(-52.43, 2.64) * mm});
            skLineSegment(sketch, "E1650", {"start": v(-52.43, 2.64) * mm, "end": v(-52.66, 2.9) * mm});
            skLineSegment(sketch, "E1651", {"start": v(-52.66, 2.9) * mm, "end": v(-52.93, 3.12) * mm});
            skLineSegment(sketch, "E1652", {"start": v(-52.93, 3.12) * mm, "end": v(-53.18, 3.34) * mm});
            skLineSegment(sketch, "E1653", {"start": v(-53.18, 3.34) * mm, "end": v(-53.47, 3.49) * mm});
            skLineSegment(sketch, "E1654", {"start": v(-53.47, 3.49) * mm, "end": v(-53.75, 3.64) * mm});
            skLineSegment(sketch, "E1655", {"start": v(-53.75, 3.64) * mm, "end": v(-54.07, 3.74) * mm});
            skLineSegment(sketch, "E1656", {"start": v(-54.07, 3.74) * mm, "end": v(-54.4, 3.83) * mm});
            skLineSegment(sketch, "E1657", {"start": v(-54.4, 3.83) * mm, "end": v(-54.71, 3.86) * mm});
            skLineSegment(sketch, "E1658", {"start": v(-54.71, 3.86) * mm, "end": v(-55.06, 3.88) * mm});
            skLineSegment(sketch, "E1659", {"start": v(-55.06, 3.88) * mm, "end": v(-55.4, 3.86) * mm});
            skLineSegment(sketch, "E1660", {"start": v(-55.4, 3.86) * mm, "end": v(-55.76, 3.81) * mm});
            skLineSegment(sketch, "E1661", {"start": v(-55.76, 3.81) * mm, "end": v(-56.08, 3.74) * mm});
            skLineSegment(sketch, "E1662", {"start": v(-56.08, 3.74) * mm, "end": v(-56.38, 3.64) * mm});
            skLineSegment(sketch, "E1663", {"start": v(-56.38, 3.64) * mm, "end": v(-56.67, 3.49) * mm});
            skLineSegment(sketch, "E1664", {"start": v(-56.67, 3.49) * mm, "end": v(-56.97, 3.31) * mm});
            skLineSegment(sketch, "E1665", {"start": v(-56.97, 3.31) * mm, "end": v(-57.24, 3.12) * mm});
            skLineSegment(sketch, "E1666", {"start": v(-57.24, 3.12) * mm, "end": v(-57.52, 2.87) * mm});
            skLineSegment(sketch, "E1667", {"start": v(-57.52, 2.87) * mm, "end": v(-57.64, 2.74) * mm});
            skLineSegment(sketch, "E1668", {"start": v(-57.64, 2.74) * mm, "end": v(-57.79, 2.62) * mm});
            skLineSegment(sketch, "E1669", {"start": v(-57.79, 2.62) * mm, "end": v(-57.96, 2.52) * mm});
            skLineSegment(sketch, "E1670", {"start": v(-57.96, 2.52) * mm, "end": v(-58.11, 2.45) * mm});
            skLineSegment(sketch, "E1671", {"start": v(-58.11, 2.45) * mm, "end": v(-58.29, 2.37) * mm});
            skLineSegment(sketch, "E1672", {"start": v(-58.29, 2.37) * mm, "end": v(-58.48, 2.32) * mm});
            skLineSegment(sketch, "E1673", {"start": v(-58.48, 2.32) * mm, "end": v(-58.66, 2.3) * mm});
            skLineSegment(sketch, "E1674", {"start": v(-58.66, 2.3) * mm, "end": v(-58.88, 2.3) * mm});
            skLineSegment(sketch, "E1675", {"start": v(-58.88, 2.3) * mm, "end": v(-59.06, 2.3) * mm});
            skLineSegment(sketch, "E1676", {"start": v(-59.06, 2.3) * mm, "end": v(-59.25, 2.32) * mm});
            skLineSegment(sketch, "E1677", {"start": v(-59.25, 2.32) * mm, "end": v(-59.43, 2.37) * mm});
            skLineSegment(sketch, "E1678", {"start": v(-59.43, 2.37) * mm, "end": v(-59.6, 2.42) * mm});
            skLineSegment(sketch, "E1679", {"start": v(-59.6, 2.42) * mm, "end": v(-59.77, 2.52) * mm});
            skLineSegment(sketch, "E1680", {"start": v(-59.77, 2.52) * mm, "end": v(-59.95, 2.62) * mm});
            skLineSegment(sketch, "E1681", {"start": v(-59.95, 2.62) * mm, "end": v(-60.1, 2.72) * mm});
            skLineSegment(sketch, "E1682", {"start": v(-60.1, 2.72) * mm, "end": v(-60.25, 2.87) * mm});
            skLineSegment(sketch, "E1683", {"start": v(-60.25, 2.87) * mm, "end": v(-60.37, 3) * mm});
            skLineSegment(sketch, "E1684", {"start": v(-60.37, 3) * mm, "end": v(-60.5, 3.17) * mm});
            skLineSegment(sketch, "E1685", {"start": v(-60.5, 3.17) * mm, "end": v(-60.6, 3.31) * mm});
            skLineSegment(sketch, "E1686", {"start": v(-60.6, 3.31) * mm, "end": v(-60.67, 3.49) * mm});
            skLineSegment(sketch, "E1687", {"start": v(-60.67, 3.49) * mm, "end": v(-60.72, 3.66) * mm});
            skLineSegment(sketch, "E1688", {"start": v(-60.72, 3.66) * mm, "end": v(-60.77, 3.83) * mm});
            skLineSegment(sketch, "E1689", {"start": v(-60.77, 3.83) * mm, "end": v(-60.8, 4.03) * mm});
            skLineSegment(sketch, "E1690", {"start": v(-60.8, 4.03) * mm, "end": v(-60.82, 4.23) * mm});
            skLineSegment(sketch, "E1691", {"start": v(-60.82, 4.23) * mm, "end": v(-60.8, 4.4) * mm});
            skLineSegment(sketch, "E1692", {"start": v(-60.8, 4.4) * mm, "end": v(-60.77, 4.6) * mm});
            skLineSegment(sketch, "E1693", {"start": v(-60.77, 4.6) * mm, "end": v(-60.72, 4.78) * mm});
            skLineSegment(sketch, "E1694", {"start": v(-60.72, 4.78) * mm, "end": v(-60.67, 4.95) * mm});
            skLineSegment(sketch, "E1695", {"start": v(-60.67, 4.95) * mm, "end": v(-60.6, 5.12) * mm});
            skLineSegment(sketch, "E1696", {"start": v(-60.6, 5.12) * mm, "end": v(-60.5, 5.27) * mm});
            skLineSegment(sketch, "E1697", {"start": v(-60.5, 5.27) * mm, "end": v(-60.37, 5.42) * mm});
            skLineSegment(sketch, "E1698", {"start": v(-60.37, 5.42) * mm, "end": v(-60.25, 5.57) * mm});
            skLineSegment(sketch, "E1699", {"start": v(-60.25, 5.57) * mm, "end": v(-59.7, 6.1) * mm});
            skLineSegment(sketch, "E1700", {"start": v(-59.7, 6.1) * mm, "end": v(-59.1, 6.54) * mm});
            skLineSegment(sketch, "E1701", {"start": v(-59.1, 6.54) * mm, "end": v(-58.5, 6.91) * mm});
            skLineSegment(sketch, "E1702", {"start": v(-58.5, 6.91) * mm, "end": v(-57.86, 7.23) * mm});
            skLineSegment(sketch, "E1703", {"start": v(-57.86, 7.23) * mm, "end": v(-57.2, 7.48) * mm});
            skLineSegment(sketch, "E1704", {"start": v(-57.2, 7.48) * mm, "end": v(-56.52, 7.63) * mm});
            skLineSegment(sketch, "E1705", {"start": v(-56.52, 7.63) * mm, "end": v(-55.8, 7.75) * mm});
            skLineSegment(sketch, "E1706", {"start": v(-55.8, 7.75) * mm, "end": v(-55.06, 7.78) * mm});
            skLineSegment(sketch, "E1707", {"start": v(-55.06, 7.78) * mm, "end": v(-54.34, 7.75) * mm});
            skLineSegment(sketch, "E1708", {"start": v(-54.34, 7.75) * mm, "end": v(-53.62, 7.65) * mm});
            skLineSegment(sketch, "E1709", {"start": v(-53.62, 7.65) * mm, "end": v(-52.95, 7.48) * mm});
            skLineSegment(sketch, "E1710", {"start": v(-52.95, 7.48) * mm, "end": v(-52.28, 7.26) * mm});
            skLineSegment(sketch, "E1711", {"start": v(-52.28, 7.26) * mm, "end": v(-51.66, 6.94) * mm});
            skLineSegment(sketch, "E1712", {"start": v(-51.66, 6.94) * mm, "end": v(-51.07, 6.59) * mm});
            skLineSegment(sketch, "E1713", {"start": v(-51.07, 6.59) * mm, "end": v(-50.5, 6.14) * mm});
            skLineSegment(sketch, "E1714", {"start": v(-50.5, 6.14) * mm, "end": v(-49.95, 5.65) * mm});
            skLineSegment(sketch, "E1715", {"start": v(-49.95, 5.65) * mm, "end": v(-49.46, 5.1) * mm});
            skLineSegment(sketch, "E1716", {"start": v(-49.46, 5.1) * mm, "end": v(-49, 4.53) * mm});
            skLineSegment(sketch, "E1717", {"start": v(-49, 4.53) * mm, "end": v(-48.64, 3.93) * mm});
            skLineSegment(sketch, "E1718", {"start": v(-48.64, 3.93) * mm, "end": v(-48.34, 3.29) * mm});
            skLineSegment(sketch, "E1719", {"start": v(-48.34, 3.29) * mm, "end": v(-48.12, 2.64) * mm});
            skLineSegment(sketch, "E1720", {"start": v(-48.12, 2.64) * mm, "end": v(-47.94, 1.95) * mm});
            skLineSegment(sketch, "E1721", {"start": v(-47.94, 1.95) * mm, "end": v(-47.84, 1.23) * mm});
            skLineSegment(sketch, "E1722", {"start": v(-47.84, 1.23) * mm, "end": v(-47.8, 0.51) * mm});
            skLineSegment(sketch, "E1723", {"start": v(-47.8, 0.51) * mm, "end": v(-47.8, -14.97) * mm});
            skLineSegment(sketch, "E1724", {"start": v(-47.8, -14.97) * mm, "end": v(-47.8, -15.14) * mm});
            skLineSegment(sketch, "E1725", {"start": v(-47.8, -15.14) * mm, "end": v(-47.82, -15.34) * mm});
            skLineSegment(sketch, "E1726", {"start": v(-47.82, -15.34) * mm, "end": v(-47.87, -15.51) * mm});
            skLineSegment(sketch, "E1727", {"start": v(-47.87, -15.51) * mm, "end": v(-47.94, -15.69) * mm});
            skLineSegment(sketch, "E1728", {"start": v(-47.94, -15.69) * mm, "end": v(-48.02, -15.86) * mm});
            skLineSegment(sketch, "E1729", {"start": v(-48.02, -15.86) * mm, "end": v(-48.12, -16.03) * mm});
            skLineSegment(sketch, "E1730", {"start": v(-48.12, -16.03) * mm, "end": v(-48.24, -16.18) * mm});
            skLineSegment(sketch, "E1731", {"start": v(-48.24, -16.18) * mm, "end": v(-48.36, -16.33) * mm});
            skLineSegment(sketch, "E1732", {"start": v(-48.36, -16.33) * mm, "end": v(-48.51, -16.46) * mm});
            skLineSegment(sketch, "E1733", {"start": v(-48.51, -16.46) * mm, "end": v(-48.66, -16.58) * mm});
            skLineSegment(sketch, "E1734", {"start": v(-48.66, -16.58) * mm, "end": v(-48.81, -16.68) * mm});
            skLineSegment(sketch, "E1735", {"start": v(-48.81, -16.68) * mm, "end": v(-48.98, -16.75) * mm});
            skLineSegment(sketch, "E1736", {"start": v(-48.98, -16.75) * mm, "end": v(-49.16, -16.8) * mm});
            skLineSegment(sketch, "E1737", {"start": v(-49.16, -16.8) * mm, "end": v(-49.33, -16.85) * mm});
            skLineSegment(sketch, "E1738", {"start": v(-49.33, -16.85) * mm, "end": v(-49.53, -16.88) * mm});
            skLineSegment(sketch, "E1739", {"start": v(-49.53, -16.88) * mm, "end": v(-49.73, -16.9) * mm});
            skLineSegment(sketch, "E1740", {"start": v(-49.73, -16.9) * mm, "end": v(-55.04, -16.9) * mm});
            skLineSegment(sketch, "E1741", {"start": v(-55.04, -16.9) * mm, "end": v(-55.78, -16.85) * mm});
            skLineSegment(sketch, "E1742", {"start": v(-55.78, -16.85) * mm, "end": v(-56.5, -16.75) * mm});
            skLineSegment(sketch, "E1743", {"start": v(-56.5, -16.75) * mm, "end": v(-57.17, -16.58) * mm});
            skLineSegment(sketch, "E1744", {"start": v(-57.17, -16.58) * mm, "end": v(-57.84, -16.36) * mm});
            skLineSegment(sketch, "E1745", {"start": v(-57.84, -16.36) * mm, "end": v(-58.46, -16.06) * mm});
            skLineSegment(sketch, "E1746", {"start": v(-58.46, -16.06) * mm, "end": v(-59.06, -15.69) * mm});
            skLineSegment(sketch, "E1747", {"start": v(-59.06, -15.69) * mm, "end": v(-59.63, -15.26) * mm});
            skLineSegment(sketch, "E1748", {"start": v(-59.63, -15.26) * mm, "end": v(-60.17, -14.77) * mm});
            skLineSegment(sketch, "E1749", {"start": v(-60.17, -14.77) * mm, "end": v(-60.67, -14.22) * mm});
            skLineSegment(sketch, "E1750", {"start": v(-60.67, -14.22) * mm, "end": v(-61.11, -13.65) * mm});
            skLineSegment(sketch, "E1751", {"start": v(-61.11, -13.65) * mm, "end": v(-61.46, -13.03) * mm});
            skLineSegment(sketch, "E1752", {"start": v(-61.46, -13.03) * mm, "end": v(-61.78, -12.41) * mm});
            skLineSegment(sketch, "E1753", {"start": v(-61.78, -12.41) * mm, "end": v(-62, -11.77) * mm});
            skLineSegment(sketch, "E1754", {"start": v(-62, -11.77) * mm, "end": v(-62.18, -11.07) * mm});
            skLineSegment(sketch, "E1755", {"start": v(-62.18, -11.07) * mm, "end": v(-62.28, -10.38) * mm});
            skLineSegment(sketch, "E1756", {"start": v(-62.28, -10.38) * mm, "end": v(-62.3, -9.63) * mm});
            skLineSegment(sketch, "E1757", {"start": v(-62.3, -9.63) * mm, "end": v(-62.3, -7.67) * mm});
            skLineSegment(sketch, "E1758", {"start": v(-62.3, -7.67) * mm, "end": v(-62.28, -6.93) * mm});
            skLineSegment(sketch, "E1759", {"start": v(-42.44, -15.34) * mm, "end": v(-42.46, -15.14) * mm});
            skLineSegment(sketch, "E1760", {"start": v(-42.46, -15.14) * mm, "end": v(-42.46, -14.97) * mm});
            skLineSegment(sketch, "E1761", {"start": v(-42.46, -14.97) * mm, "end": v(-42.46, 5.37) * mm});
            skLineSegment(sketch, "E1762", {"start": v(-42.46, 5.37) * mm, "end": v(-42.46, 5.55) * mm});
            skLineSegment(sketch, "E1763", {"start": v(-42.46, 5.55) * mm, "end": v(-42.44, 5.74) * mm});
            skLineSegment(sketch, "E1764", {"start": v(-42.44, 5.74) * mm, "end": v(-42.39, 5.92) * mm});
            skLineSegment(sketch, "E1765", {"start": v(-42.39, 5.92) * mm, "end": v(-42.31, 6.1) * mm});
            skSolve(sketch);
        }
        {
            var Q0;
            Q0=makeQuery(id+"F0.imprint","IMPRINT",FACE,{"disambiguationData":[TD([[makeQuery(id+"F0.imprint","IMPRINT",EDGE,{"derivedFrom":sQuery(id+"F0.wireOp",EDGE,"E0")}),1.0]])]});
            extrude(context, id + "F1", {"entities" : qUnion([Q0]), "depth" : 2.03 * mm, "offsetDistance" : 25.4 * mm});
        }
    });
